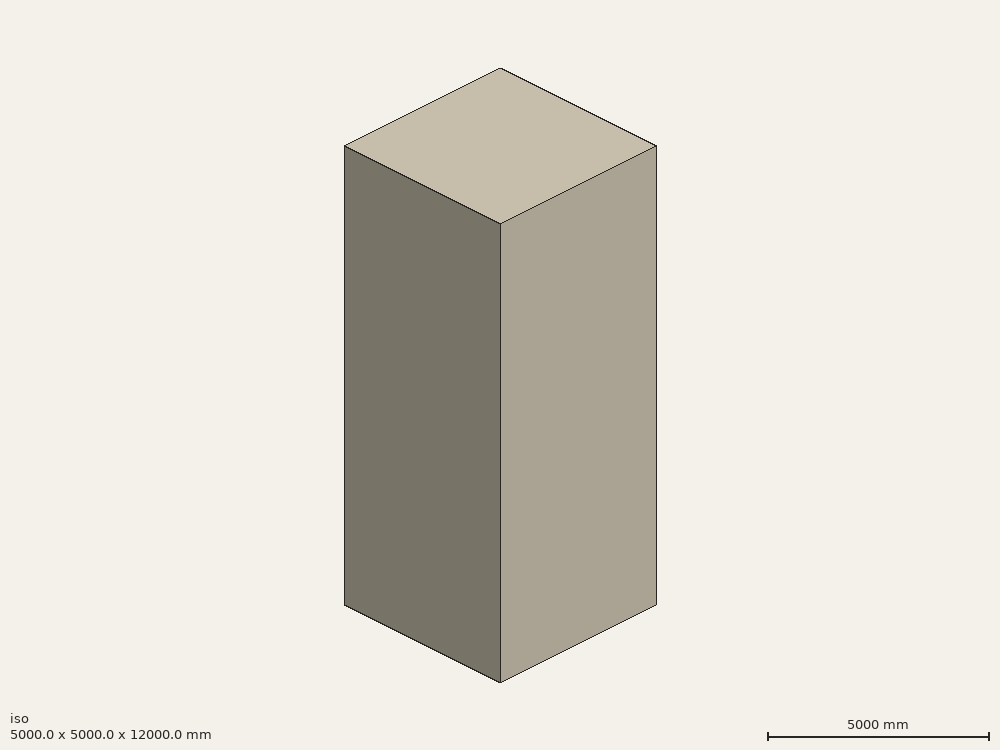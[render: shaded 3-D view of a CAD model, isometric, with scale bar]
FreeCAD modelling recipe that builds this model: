
FCSTD DOCUMENT  (FreeCAD 1.0R39109 (Git))
Label: revolveTester-7_scaled
License: All rights reserved
LicenseURL: http://en.wikipedia.org/wiki/All_rights_reserved
objects: App::DocumentObjectGroupPython×1248, Part::FeaturePython×2, App::Part×2, Sketcher::SketchObject×1, Part::Revolution×1, Part::Cylinder×1, Part::Cut×1
note: 7 computed .brp shape members not serialized (recipe doc carries the construction recipe); baked Part::Feature solids carry a one-line shape summary decoded from their .brp

FEATURE [App::DocumentObjectGroupPython] HALFPI  # scripted group (container) (typed FeaturePython)
  name = HALFPI
  value = pi/2.
FEATURE [App::DocumentObjectGroupPython] PI  # scripted group (container) (typed FeaturePython)
  name = PI
  value = 1.*pi
FEATURE [App::DocumentObjectGroupPython] TWOPI  # scripted group (container) (typed FeaturePython)
  name = TWOPI
  value = 2.*pi
FEATURE [App::DocumentObjectGroupPython] Constants  # scripted group (container) (typed FeaturePython)
  Group = -> [HALFPI,PI,TWOPI]
FEATURE [App::DocumentObjectGroupPython] Variables  # scripted group (container) (typed FeaturePython)
FEATURE [App::DocumentObjectGroupPython] Quantities  # scripted group (container) (typed FeaturePython)
FEATURE [App::DocumentObjectGroupPython] Isotopes  # scripted group (container) (typed FeaturePython)
FEATURE [App::DocumentObjectGroupPython] Elements  # scripted group (container) (typed FeaturePython)
FEATURE [App::DocumentObjectGroupPython] G4Isotopes  # scripted group (container) (typed FeaturePython)
FEATURE [App::DocumentObjectGroupPython] H_element  # scripted group (container) (typed FeaturePython)
  Z = 1
  atom_value = 1.008
  formula = H
  name = H_element
FEATURE [App::DocumentObjectGroupPython] He_element  # scripted group (container) (typed FeaturePython)
  Z = 2
  atom_value = 4.0026
  formula = He
  name = He_element
FEATURE [App::DocumentObjectGroupPython] Li_element  # scripted group (container) (typed FeaturePython)
  Z = 3
  atom_value = 6.94
  formula = Li
  name = Li_element
FEATURE [App::DocumentObjectGroupPython] Be_element  # scripted group (container) (typed FeaturePython)
  Z = 4
  atom_value = 9.01218
  formula = Be
  name = Be_element
FEATURE [App::DocumentObjectGroupPython] B_element  # scripted group (container) (typed FeaturePython)
  Z = 5
  atom_value = 10.81
  formula = B
  name = B_element
FEATURE [App::DocumentObjectGroupPython] C_element  # scripted group (container) (typed FeaturePython)
  Z = 6
  atom_value = 12.011
  formula = C
  name = C_element
FEATURE [App::DocumentObjectGroupPython] N_element  # scripted group (container) (typed FeaturePython)
  Z = 7
  atom_value = 14.007
  formula = N
  name = N_element
FEATURE [App::DocumentObjectGroupPython] O_element  # scripted group (container) (typed FeaturePython)
  Z = 8
  atom_value = 15.999
  formula = O
  name = O_element
FEATURE [App::DocumentObjectGroupPython] F_element  # scripted group (container) (typed FeaturePython)
  Z = 9
  atom_value = 18.9984
  formula = F
  name = F_element
FEATURE [App::DocumentObjectGroupPython] Ne_element  # scripted group (container) (typed FeaturePython)
  Z = 10
  atom_value = 20.1797
  formula = Ne
  name = Ne_element
FEATURE [App::DocumentObjectGroupPython] Na_element  # scripted group (container) (typed FeaturePython)
  Z = 11
  atom_value = 22.9898
  formula = Na
  name = Na_element
FEATURE [App::DocumentObjectGroupPython] Mg_element  # scripted group (container) (typed FeaturePython)
  Z = 12
  atom_value = 24.305
  formula = Mg
  name = Mg_element
FEATURE [App::DocumentObjectGroupPython] Al_element  # scripted group (container) (typed FeaturePython)
  Z = 13
  atom_value = 26.9815
  formula = Al
  name = Al_element
FEATURE [App::DocumentObjectGroupPython] Si_element  # scripted group (container) (typed FeaturePython)
  Z = 14
  atom_value = 28.085
  formula = Si
  name = Si_element
FEATURE [App::DocumentObjectGroupPython] P_element  # scripted group (container) (typed FeaturePython)
  Z = 15
  atom_value = 30.9738
  formula = P
  name = P_element
FEATURE [App::DocumentObjectGroupPython] S_element  # scripted group (container) (typed FeaturePython)
  Z = 16
  atom_value = 32.06
  formula = S
  name = S_element
FEATURE [App::DocumentObjectGroupPython] Cl_element  # scripted group (container) (typed FeaturePython)
  Z = 17
  atom_value = 35.45
  formula = Cl
  name = Cl_element
FEATURE [App::DocumentObjectGroupPython] Ar_element  # scripted group (container) (typed FeaturePython)
  Z = 18
  atom_value = 39.95
  formula = Ar
  name = Ar_element
FEATURE [App::DocumentObjectGroupPython] K_element  # scripted group (container) (typed FeaturePython)
  Z = 19
  atom_value = 39.0983
  formula = K
  name = K_element
FEATURE [App::DocumentObjectGroupPython] Ca_element  # scripted group (container) (typed FeaturePython)
  Z = 20
  atom_value = 40.078
  formula = Ca
  name = Ca_element
FEATURE [App::DocumentObjectGroupPython] Sc_element  # scripted group (container) (typed FeaturePython)
  Z = 21
  atom_value = 44.9559
  formula = Sc
  name = Sc_element
FEATURE [App::DocumentObjectGroupPython] Ti_element  # scripted group (container) (typed FeaturePython)
  Z = 22
  atom_value = 47.867
  formula = Ti
  name = Ti_element
FEATURE [App::DocumentObjectGroupPython] V_element  # scripted group (container) (typed FeaturePython)
  Z = 23
  atom_value = 50.9415
  formula = V
  name = V_element
FEATURE [App::DocumentObjectGroupPython] Cr_element  # scripted group (container) (typed FeaturePython)
  Z = 24
  atom_value = 51.9961
  formula = Cr
  name = Cr_element
FEATURE [App::DocumentObjectGroupPython] Mn_element  # scripted group (container) (typed FeaturePython)
  Z = 25
  atom_value = 54.938
  formula = Mn
  name = Mn_element
FEATURE [App::DocumentObjectGroupPython] Fe_element  # scripted group (container) (typed FeaturePython)
  Z = 26
  atom_value = 55.845
  formula = Fe
  name = Fe_element
FEATURE [App::DocumentObjectGroupPython] Co_element  # scripted group (container) (typed FeaturePython)
  Z = 27
  atom_value = 58.9332
  formula = Co
  name = Co_element
FEATURE [App::DocumentObjectGroupPython] Ni_element  # scripted group (container) (typed FeaturePython)
  Z = 28
  atom_value = 58.6934
  formula = Ni
  name = Ni_element
FEATURE [App::DocumentObjectGroupPython] Cu_element  # scripted group (container) (typed FeaturePython)
  Z = 29
  atom_value = 63.546
  formula = Cu
  name = Cu_element
FEATURE [App::DocumentObjectGroupPython] Zn_element  # scripted group (container) (typed FeaturePython)
  Z = 30
  atom_value = 65.38
  formula = Zn
  name = Zn_element
FEATURE [App::DocumentObjectGroupPython] Ga_element  # scripted group (container) (typed FeaturePython)
  Z = 31
  atom_value = 69.723
  formula = Ga
  name = Ga_element
FEATURE [App::DocumentObjectGroupPython] Ge_element  # scripted group (container) (typed FeaturePython)
  Z = 32
  atom_value = 72.63
  formula = Ge
  name = Ge_element
FEATURE [App::DocumentObjectGroupPython] As_element  # scripted group (container) (typed FeaturePython)
  Z = 33
  atom_value = 74.9216
  formula = As
  name = As_element
FEATURE [App::DocumentObjectGroupPython] Se_element  # scripted group (container) (typed FeaturePython)
  Z = 34
  atom_value = 78.971
  formula = Se
  name = Se_element
FEATURE [App::DocumentObjectGroupPython] Br_element  # scripted group (container) (typed FeaturePython)
  Z = 35
  atom_value = 79.904
  formula = Br
  name = Br_element
FEATURE [App::DocumentObjectGroupPython] Kr_element  # scripted group (container) (typed FeaturePython)
  Z = 36
  atom_value = 83.798
  formula = Kr
  name = Kr_element
FEATURE [App::DocumentObjectGroupPython] Rb_element  # scripted group (container) (typed FeaturePython)
  Z = 37
  atom_value = 85.4678
  formula = Rb
  name = Rb_element
FEATURE [App::DocumentObjectGroupPython] Sr_element  # scripted group (container) (typed FeaturePython)
  Z = 38
  atom_value = 87.62
  formula = Sr
  name = Sr_element
FEATURE [App::DocumentObjectGroupPython] Y_element  # scripted group (container) (typed FeaturePython)
  Z = 39
  atom_value = 88.9058
  formula = Y
  name = Y_element
FEATURE [App::DocumentObjectGroupPython] Zr_element  # scripted group (container) (typed FeaturePython)
  Z = 40
  atom_value = 91.224
  formula = Zr
  name = Zr_element
FEATURE [App::DocumentObjectGroupPython] Nb_element  # scripted group (container) (typed FeaturePython)
  Z = 41
  atom_value = 92.9064
  formula = Nb
  name = Nb_element
FEATURE [App::DocumentObjectGroupPython] Mo_element  # scripted group (container) (typed FeaturePython)
  Z = 42
  atom_value = 95.95
  formula = Mo
  name = Mo_element
FEATURE [App::DocumentObjectGroupPython] Tc_element  # scripted group (container) (typed FeaturePython)
  Z = 43
  atom_value = 97
  formula = Tc
  name = Tc_element
FEATURE [App::DocumentObjectGroupPython] Ru_element  # scripted group (container) (typed FeaturePython)
  Z = 44
  atom_value = 101.07
  formula = Ru
  name = Ru_element
FEATURE [App::DocumentObjectGroupPython] Rh_element  # scripted group (container) (typed FeaturePython)
  Z = 45
  atom_value = 102.905
  formula = Rh
  name = Rh_element
FEATURE [App::DocumentObjectGroupPython] Pd_element  # scripted group (container) (typed FeaturePython)
  Z = 46
  atom_value = 106.42
  formula = Pd
  name = Pd_element
FEATURE [App::DocumentObjectGroupPython] Ag_element  # scripted group (container) (typed FeaturePython)
  Z = 47
  atom_value = 107.868
  formula = Ag
  name = Ag_element
FEATURE [App::DocumentObjectGroupPython] Cd_element  # scripted group (container) (typed FeaturePython)
  Z = 48
  atom_value = 112.414
  formula = Cd
  name = Cd_element
FEATURE [App::DocumentObjectGroupPython] In_element  # scripted group (container) (typed FeaturePython)
  Z = 49
  atom_value = 114.818
  formula = In
  name = In_element
FEATURE [App::DocumentObjectGroupPython] Sn_element  # scripted group (container) (typed FeaturePython)
  Z = 50
  atom_value = 118.71
  formula = Sn
  name = Sn_element
FEATURE [App::DocumentObjectGroupPython] Sb_element  # scripted group (container) (typed FeaturePython)
  Z = 51
  atom_value = 121.76
  formula = Sb
  name = Sb_element
FEATURE [App::DocumentObjectGroupPython] Te_element  # scripted group (container) (typed FeaturePython)
  Z = 52
  atom_value = 127.6
  formula = Te
  name = Te_element
FEATURE [App::DocumentObjectGroupPython] I_element  # scripted group (container) (typed FeaturePython)
  Z = 53
  atom_value = 126.904
  formula = I
  name = I_element
FEATURE [App::DocumentObjectGroupPython] Xe_element  # scripted group (container) (typed FeaturePython)
  Z = 54
  atom_value = 131.293
  formula = Xe
  name = Xe_element
FEATURE [App::DocumentObjectGroupPython] Cs_element  # scripted group (container) (typed FeaturePython)
  Z = 55
  atom_value = 132.905
  formula = Cs
  name = Cs_element
FEATURE [App::DocumentObjectGroupPython] Ba_element  # scripted group (container) (typed FeaturePython)
  Z = 56
  atom_value = 137.327
  formula = Ba
  name = Ba_element
FEATURE [App::DocumentObjectGroupPython] La_element  # scripted group (container) (typed FeaturePython)
  Z = 57
  atom_value = 138.905
  formula = La
  name = La_element
FEATURE [App::DocumentObjectGroupPython] Ce_element  # scripted group (container) (typed FeaturePython)
  Z = 58
  atom_value = 140.116
  formula = Ce
  name = Ce_element
FEATURE [App::DocumentObjectGroupPython] Pr_element  # scripted group (container) (typed FeaturePython)
  Z = 59
  atom_value = 140.908
  formula = Pr
  name = Pr_element
FEATURE [App::DocumentObjectGroupPython] Nd_element  # scripted group (container) (typed FeaturePython)
  Z = 60
  atom_value = 144.242
  formula = Nd
  name = Nd_element
FEATURE [App::DocumentObjectGroupPython] Pm_element  # scripted group (container) (typed FeaturePython)
  Z = 61
  atom_value = 145
  formula = Pm
  name = Pm_element
FEATURE [App::DocumentObjectGroupPython] Sm_element  # scripted group (container) (typed FeaturePython)
  Z = 62
  atom_value = 150.36
  formula = Sm
  name = Sm_element
FEATURE [App::DocumentObjectGroupPython] Eu_element  # scripted group (container) (typed FeaturePython)
  Z = 63
  atom_value = 151.964
  formula = Eu
  name = Eu_element
FEATURE [App::DocumentObjectGroupPython] Gd_element  # scripted group (container) (typed FeaturePython)
  Z = 64
  atom_value = 157.25
  formula = Gd
  name = Gd_element
FEATURE [App::DocumentObjectGroupPython] Tb_element  # scripted group (container) (typed FeaturePython)
  Z = 65
  atom_value = 158.925
  formula = Tb
  name = Tb_element
FEATURE [App::DocumentObjectGroupPython] Dy_element  # scripted group (container) (typed FeaturePython)
  Z = 66
  atom_value = 162.5
  formula = Dy
  name = Dy_element
FEATURE [App::DocumentObjectGroupPython] Ho_element  # scripted group (container) (typed FeaturePython)
  Z = 67
  atom_value = 164.93
  formula = Ho
  name = Ho_element
FEATURE [App::DocumentObjectGroupPython] Er_element  # scripted group (container) (typed FeaturePython)
  Z = 68
  atom_value = 167.259
  formula = Er
  name = Er_element
FEATURE [App::DocumentObjectGroupPython] Tm_element  # scripted group (container) (typed FeaturePython)
  Z = 69
  atom_value = 168.934
  formula = Tm
  name = Tm_element
FEATURE [App::DocumentObjectGroupPython] Yb_element  # scripted group (container) (typed FeaturePython)
  Z = 70
  atom_value = 173.045
  formula = Yb
  name = Yb_element
FEATURE [App::DocumentObjectGroupPython] Lu_element  # scripted group (container) (typed FeaturePython)
  Z = 71
  atom_value = 174.967
  formula = Lu
  name = Lu_element
FEATURE [App::DocumentObjectGroupPython] Hf_element  # scripted group (container) (typed FeaturePython)
  Z = 72
  atom_value = 178.49
  formula = Hf
  name = Hf_element
FEATURE [App::DocumentObjectGroupPython] Ta_element  # scripted group (container) (typed FeaturePython)
  Z = 73
  atom_value = 180.948
  formula = Ta
  name = Ta_element
FEATURE [App::DocumentObjectGroupPython] W_element  # scripted group (container) (typed FeaturePython)
  Z = 74
  atom_value = 183.84
  formula = W
  name = W_element
FEATURE [App::DocumentObjectGroupPython] Re_element  # scripted group (container) (typed FeaturePython)
  Z = 75
  atom_value = 186.207
  formula = Re
  name = Re_element
FEATURE [App::DocumentObjectGroupPython] Os_element  # scripted group (container) (typed FeaturePython)
  Z = 76
  atom_value = 190.23
  formula = Os
  name = Os_element
FEATURE [App::DocumentObjectGroupPython] Ir_element  # scripted group (container) (typed FeaturePython)
  Z = 77
  atom_value = 192.217
  formula = Ir
  name = Ir_element
FEATURE [App::DocumentObjectGroupPython] Pt_element  # scripted group (container) (typed FeaturePython)
  Z = 78
  atom_value = 195.084
  formula = Pt
  name = Pt_element
FEATURE [App::DocumentObjectGroupPython] Au_element  # scripted group (container) (typed FeaturePython)
  Z = 79
  atom_value = 196.967
  formula = Au
  name = Au_element
FEATURE [App::DocumentObjectGroupPython] Hg_element  # scripted group (container) (typed FeaturePython)
  Z = 80
  atom_value = 200.592
  formula = Hg
  name = Hg_element
FEATURE [App::DocumentObjectGroupPython] Tl_element  # scripted group (container) (typed FeaturePython)
  Z = 81
  atom_value = 204.38
  formula = Tl
  name = Tl_element
FEATURE [App::DocumentObjectGroupPython] Pb_element  # scripted group (container) (typed FeaturePython)
  Z = 82
  atom_value = 207.2
  formula = Pb
  name = Pb_element
FEATURE [App::DocumentObjectGroupPython] Bi_element  # scripted group (container) (typed FeaturePython)
  Z = 83
  atom_value = 208.98
  formula = Bi
  name = Bi_element
FEATURE [App::DocumentObjectGroupPython] Po_element  # scripted group (container) (typed FeaturePython)
  Z = 84
  atom_value = 209
  formula = Po
  name = Po_element
FEATURE [App::DocumentObjectGroupPython] At_element  # scripted group (container) (typed FeaturePython)
  Z = 85
  atom_value = 210
  formula = At
  name = At_element
FEATURE [App::DocumentObjectGroupPython] Rn_element  # scripted group (container) (typed FeaturePython)
  Z = 86
  atom_value = 222
  formula = Rn
  name = Rn_element
FEATURE [App::DocumentObjectGroupPython] Fr_element  # scripted group (container) (typed FeaturePython)
  Z = 87
  atom_value = 223
  formula = Fr
  name = Fr_element
FEATURE [App::DocumentObjectGroupPython] Ra_element  # scripted group (container) (typed FeaturePython)
  Z = 88
  atom_value = 226
  formula = Ra
  name = Ra_element
FEATURE [App::DocumentObjectGroupPython] Ac_element  # scripted group (container) (typed FeaturePython)
  Z = 89
  atom_value = 227
  formula = Ac
  name = Ac_element
FEATURE [App::DocumentObjectGroupPython] Th_element  # scripted group (container) (typed FeaturePython)
  Z = 90
  atom_value = 232.038
  formula = Th
  name = Th_element
FEATURE [App::DocumentObjectGroupPython] Pa_element  # scripted group (container) (typed FeaturePython)
  Z = 91
  atom_value = 231.036
  formula = Pa
  name = Pa_element
FEATURE [App::DocumentObjectGroupPython] U_element  # scripted group (container) (typed FeaturePython)
  Z = 92
  atom_value = 238.029
  formula = U
  name = U_element
FEATURE [App::DocumentObjectGroupPython] Np_element  # scripted group (container) (typed FeaturePython)
  Z = 93
  atom_value = 237
  formula = Np
  name = Np_element
FEATURE [App::DocumentObjectGroupPython] Pu_element  # scripted group (container) (typed FeaturePython)
  Z = 94
  atom_value = 244
  formula = Pu
  name = Pu_element
FEATURE [App::DocumentObjectGroupPython] Am_element  # scripted group (container) (typed FeaturePython)
  Z = 95
  atom_value = 243
  formula = Am
  name = Am_element
FEATURE [App::DocumentObjectGroupPython] Cm_element  # scripted group (container) (typed FeaturePython)
  Z = 96
  atom_value = 247
  formula = Cm
  name = Cm_element
FEATURE [App::DocumentObjectGroupPython] Bk_element  # scripted group (container) (typed FeaturePython)
  Z = 97
  atom_value = 247
  formula = Bk
  name = Bk_element
FEATURE [App::DocumentObjectGroupPython] Cf_element  # scripted group (container) (typed FeaturePython)
  Z = 98
  atom_value = 251
  formula = Cf
  name = Cf_element
FEATURE [App::DocumentObjectGroupPython] G4Elements  # scripted group (container) (typed FeaturePython)
  Group = -> [H_element,He_element,Li_element,Be_element,B_element,C_element,N_element,O_element,F_element,Ne_element,Na_element,Mg_element,Al_element,Si_element,P_element,S_element,Cl_element,Ar_element,K_element,Ca_element,Sc_element,Ti_element,V_element,Cr_element,Mn_element,Fe_element,Co_element,Ni_element,Cu_element,Zn_element,Ga_element,Ge_element,As_element,Se_element,Br_element,Kr_element,Rb_element,+61 more]
FEATURE [App::DocumentObjectGroupPython] H_element001  label="H_element : 0.101"  # scripted group (container) (typed FeaturePython)
  n = 0.101327
FEATURE [App::DocumentObjectGroupPython] C_element001  label="C_element : 0.775"  # scripted group (container) (typed FeaturePython)
  n = 0.7755
FEATURE [App::DocumentObjectGroupPython] N_element001  label="N_element : 0.035"  # scripted group (container) (typed FeaturePython)
  n = 0.035057
FEATURE [App::DocumentObjectGroupPython] O_element001  label="O_element : 0.052"  # scripted group (container) (typed FeaturePython)
  n = 0.0523159
FEATURE [App::DocumentObjectGroupPython] F_element001  label="F_element : 0.017"  # scripted group (container) (typed FeaturePython)
  n = 0.017422
FEATURE [App::DocumentObjectGroupPython] Ca_element001  label="Ca_element : 0.018"  # scripted group (container) (typed FeaturePython)
  n = 0.018378
FEATURE [App::DocumentObjectGroupPython] G4_A_150_TISSUE  label="G4_A-150_TISSUE"  # scripted group (container) (typed FeaturePython)
  Dunit = g/cm3
  Dvalue = 1.127
  Group = -> [H_element001,C_element001,N_element001,O_element001,F_element001,Ca_element001]
  conduct = 2
  density = 1
  expand = 3
  formula = G4_A-150_TISSUE
  name = G4_A-150_TISSUE
  specific = 4
FEATURE [App::DocumentObjectGroupPython] C_element002  label="C_element : 3"  # scripted group (container) (typed FeaturePython)
  n = 3
  ref = C_element
FEATURE [App::DocumentObjectGroupPython] H_element002  label="H_element : 6"  # scripted group (container) (typed FeaturePython)
  n = 6
  ref = H_element
FEATURE [App::DocumentObjectGroupPython] O_element002  label="O_element : 1"  # scripted group (container) (typed FeaturePython)
  n = 1
  ref = O_element
FEATURE [App::DocumentObjectGroupPython] G4_ACETONE  # scripted group (container) (typed FeaturePython)
  Dunit = g/cm3
  Dvalue = 0.7899
  Group = -> [C_element002,H_element002,O_element002]
  conduct = 2
  density = 1
  expand = 3
  formula = G4_ACETONE
  name = G4_ACETONE
  specific = 4
FEATURE [App::DocumentObjectGroupPython] C_element003  label="C_element : 2"  # scripted group (container) (typed FeaturePython)
  n = 2
  ref = C_element
FEATURE [App::DocumentObjectGroupPython] H_element003  label="H_element : 2"  # scripted group (container) (typed FeaturePython)
  n = 2
  ref = H_element
FEATURE [App::DocumentObjectGroupPython] G4_ACETYLENE  # scripted group (container) (typed FeaturePython)
  Dunit = g/cm3
  Dvalue = 0.0010967
  Group = -> [C_element003,H_element003]
  conduct = 2
  density = 1
  expand = 3
  formula = G4_ACETYLENE
  name = G4_ACETYLENE
  specific = 4
FEATURE [App::DocumentObjectGroupPython] C_element004  label="C_element : 5"  # scripted group (container) (typed FeaturePython)
  n = 5
  ref = C_element
FEATURE [App::DocumentObjectGroupPython] H_element004  label="H_element : 5"  # scripted group (container) (typed FeaturePython)
  n = 5
  ref = H_element
FEATURE [App::DocumentObjectGroupPython] N_element002  label="N_element : 5"  # scripted group (container) (typed FeaturePython)
  n = 5
  ref = N_element
FEATURE [App::DocumentObjectGroupPython] G4_ADENINE  # scripted group (container) (typed FeaturePython)
  Dunit = g/cm3
  Dvalue = 1.6
  Group = -> [C_element004,H_element004,N_element002]
  conduct = 2
  density = 1
  expand = 3
  formula = G4_ADENINE
  name = G4_ADENINE
  specific = 4
FEATURE [App::DocumentObjectGroupPython] H_element005  label="H_element : 0.114"  # scripted group (container) (typed FeaturePython)
  n = 0.114
FEATURE [App::DocumentObjectGroupPython] C_element005  label="C_element : 0.598"  # scripted group (container) (typed FeaturePython)
  n = 0.598
FEATURE [App::DocumentObjectGroupPython] N_element003  label="N_element : 0.007"  # scripted group (container) (typed FeaturePython)
  n = 0.007
FEATURE [App::DocumentObjectGroupPython] O_element003  label="O_element : 0.278"  # scripted group (container) (typed FeaturePython)
  n = 0.278
FEATURE [App::DocumentObjectGroupPython] Na_element001  label="Na_element : 0.001"  # scripted group (container) (typed FeaturePython)
  n = 0.001
FEATURE [App::DocumentObjectGroupPython] S_element001  label="S_element : 0.001"  # scripted group (container) (typed FeaturePython)
  n = 0.001
FEATURE [App::DocumentObjectGroupPython] Cl_element001  label="Cl_element : 0.001"  # scripted group (container) (typed FeaturePython)
  n = 0.001
FEATURE [App::DocumentObjectGroupPython] G4_ADIPOSE_TISSUE_ICRP  # scripted group (container) (typed FeaturePython)
  Dunit = g/cm3
  Dvalue = 0.95
  Group = -> [H_element005,C_element005,N_element003,O_element003,Na_element001,S_element001,Cl_element001]
  conduct = 2
  density = 1
  expand = 3
  formula = G4_ADIPOSE_TISSUE_ICRP
  name = G4_ADIPOSE_TISSUE_ICRP
  specific = 4
FEATURE [App::DocumentObjectGroupPython] C_element006  label="C_element : 0.000"  # scripted group (container) (typed FeaturePython)
  n = 0.000124
FEATURE [App::DocumentObjectGroupPython] N_element004  label="N_element : 0.755"  # scripted group (container) (typed FeaturePython)
  n = 0.755268
FEATURE [App::DocumentObjectGroupPython] O_element004  label="O_element : 0.232"  # scripted group (container) (typed FeaturePython)
  n = 0.231781
FEATURE [App::DocumentObjectGroupPython] Ar_element001  label="Ar_element : 0.013"  # scripted group (container) (typed FeaturePython)
  n = 0.012827
FEATURE [App::DocumentObjectGroupPython] G4_AIR  # scripted group (container) (typed FeaturePython)
  Dunit = g/cm3
  Dvalue = 0.00120479
  Group = -> [C_element006,N_element004,O_element004,Ar_element001]
  conduct = 2
  density = 1
  expand = 3
  formula = G4_AIR
  name = G4_AIR
  specific = 4
FEATURE [App::DocumentObjectGroupPython] C_element007  label="C_element : 006"  # scripted group (container) (typed FeaturePython)
  n = 3
  ref = C_element
FEATURE [App::DocumentObjectGroupPython] H_element006  label="H_element : 7"  # scripted group (container) (typed FeaturePython)
  n = 7
  ref = H_element
FEATURE [App::DocumentObjectGroupPython] N_element005  label="N_element : 1"  # scripted group (container) (typed FeaturePython)
  n = 1
  ref = N_element
FEATURE [App::DocumentObjectGroupPython] O_element005  label="O_element : 2"  # scripted group (container) (typed FeaturePython)
  n = 2
  ref = O_element
FEATURE [App::DocumentObjectGroupPython] G4_ALANINE  # scripted group (container) (typed FeaturePython)
  Dunit = g/cm3
  Dvalue = 1.42
  Group = -> [C_element007,H_element006,N_element005,O_element005]
  conduct = 2
  density = 1
  expand = 3
  formula = G4_ALANINE
  name = G4_ALANINE
  specific = 4
FEATURE [App::DocumentObjectGroupPython] Al_element001  label="Al_element : 2"  # scripted group (container) (typed FeaturePython)
  n = 2
  ref = Al_element
FEATURE [App::DocumentObjectGroupPython] O_element006  label="O_element : 3"  # scripted group (container) (typed FeaturePython)
  n = 3
  ref = O_element
FEATURE [App::DocumentObjectGroupPython] G4_ALUMINUM_OXIDE  # scripted group (container) (typed FeaturePython)
  Dunit = g/cm3
  Dvalue = 3.97
  Group = -> [Al_element001,O_element006]
  conduct = 2
  density = 1
  expand = 3
  formula = G4_ALUMINUM_OXIDE
  name = G4_ALUMINUM_OXIDE
  specific = 4
FEATURE [App::DocumentObjectGroupPython] H_element007  label="H_element : 0.106"  # scripted group (container) (typed FeaturePython)
  n = 0.10593
FEATURE [App::DocumentObjectGroupPython] C_element008  label="C_element : 0.789"  # scripted group (container) (typed FeaturePython)
  n = 0.788974
FEATURE [App::DocumentObjectGroupPython] O_element007  label="O_element : 0.105"  # scripted group (container) (typed FeaturePython)
  n = 0.105096
FEATURE [App::DocumentObjectGroupPython] G4_AMBER  # scripted group (container) (typed FeaturePython)
  Dunit = g/cm3
  Dvalue = 1.1
  Group = -> [H_element007,C_element008,O_element007]
  conduct = 2
  density = 1
  expand = 3
  formula = G4_AMBER
  name = G4_AMBER
  specific = 4
FEATURE [App::DocumentObjectGroupPython] N_element006  label="N_element : 006"  # scripted group (container) (typed FeaturePython)
  n = 1
  ref = N_element
FEATURE [App::DocumentObjectGroupPython] H_element008  label="H_element : 3"  # scripted group (container) (typed FeaturePython)
  n = 3
  ref = H_element
FEATURE [App::DocumentObjectGroupPython] G4_AMMONIA  # scripted group (container) (typed FeaturePython)
  Dunit = g/cm3
  Dvalue = 0.000826019
  Group = -> [N_element006,H_element008]
  conduct = 2
  density = 1
  expand = 3
  formula = G4_AMMONIA
  name = G4_AMMONIA
  specific = 4
FEATURE [App::DocumentObjectGroupPython] C_element009  label="C_element : 6"  # scripted group (container) (typed FeaturePython)
  n = 6
  ref = C_element
FEATURE [App::DocumentObjectGroupPython] H_element009  label="H_element : 008"  # scripted group (container) (typed FeaturePython)
  n = 7
  ref = H_element
FEATURE [App::DocumentObjectGroupPython] N_element007  label="N_element : 007"  # scripted group (container) (typed FeaturePython)
  n = 1
  ref = N_element
FEATURE [App::DocumentObjectGroupPython] G4_ANILINE  # scripted group (container) (typed FeaturePython)
  Dunit = g/cm3
  Dvalue = 1.0235
  Group = -> [C_element009,H_element009,N_element007]
  conduct = 2
  density = 1
  expand = 3
  formula = G4_ANILINE
  name = G4_ANILINE
  specific = 4
FEATURE [App::DocumentObjectGroupPython] C_element010  label="C_element : 14"  # scripted group (container) (typed FeaturePython)
  n = 14
  ref = C_element
FEATURE [App::DocumentObjectGroupPython] H_element010  label="H_element : 10"  # scripted group (container) (typed FeaturePython)
  n = 10
  ref = H_element
FEATURE [App::DocumentObjectGroupPython] G4_ANTHRACENE  # scripted group (container) (typed FeaturePython)
  Dunit = g/cm3
  Dvalue = 1.283
  Group = -> [C_element010,H_element010]
  conduct = 2
  density = 1
  expand = 3
  formula = G4_ANTHRACENE
  name = G4_ANTHRACENE
  specific = 4
FEATURE [App::DocumentObjectGroupPython] H_element011  label="H_element : 0.065"  # scripted group (container) (typed FeaturePython)
  n = 0.0654709
FEATURE [App::DocumentObjectGroupPython] C_element011  label="C_element : 0.537"  # scripted group (container) (typed FeaturePython)
  n = 0.536944
FEATURE [App::DocumentObjectGroupPython] N_element008  label="N_element : 0.021"  # scripted group (container) (typed FeaturePython)
  n = 0.0215
FEATURE [App::DocumentObjectGroupPython] O_element008  label="O_element : 0.032"  # scripted group (container) (typed FeaturePython)
  n = 0.032085
FEATURE [App::DocumentObjectGroupPython] F_element002  label="F_element : 0.167"  # scripted group (container) (typed FeaturePython)
  n = 0.167411
FEATURE [App::DocumentObjectGroupPython] Ca_element002  label="Ca_element : 0.177"  # scripted group (container) (typed FeaturePython)
  n = 0.176589
FEATURE [App::DocumentObjectGroupPython] G4_B_100_BONE  label="G4_B-100_BONE"  # scripted group (container) (typed FeaturePython)
  Dunit = g/cm3
  Dvalue = 1.45
  Group = -> [H_element011,C_element011,N_element008,O_element008,F_element002,Ca_element002]
  conduct = 2
  density = 1
  expand = 3
  formula = G4_B-100_BONE
  name = G4_B-100_BONE
  specific = 4
FEATURE [App::DocumentObjectGroupPython] H_element012  label="H_element : 0.057"  # scripted group (container) (typed FeaturePython)
  n = 0.057441
FEATURE [App::DocumentObjectGroupPython] C_element012  label="C_element : 0.790"  # scripted group (container) (typed FeaturePython)
  n = 0.774591
FEATURE [App::DocumentObjectGroupPython] O_element009  label="O_element : 0.168"  # scripted group (container) (typed FeaturePython)
  n = 0.167968
FEATURE [App::DocumentObjectGroupPython] G4_BAKELITE  # scripted group (container) (typed FeaturePython)
  Dunit = g/cm3
  Dvalue = 1.25
  Group = -> [H_element012,C_element012,O_element009]
  conduct = 2
  density = 1
  expand = 3
  formula = G4_BAKELITE
  name = G4_BAKELITE
  specific = 4
FEATURE [App::DocumentObjectGroupPython] Ba_element001  label="Ba_element : 1"  # scripted group (container) (typed FeaturePython)
  n = 1
  ref = Ba_element
FEATURE [App::DocumentObjectGroupPython] F_element003  label="F_element : 2"  # scripted group (container) (typed FeaturePython)
  n = 2
  ref = F_element
FEATURE [App::DocumentObjectGroupPython] G4_BARIUM_FLUORIDE  # scripted group (container) (typed FeaturePython)
  Dunit = g/cm3
  Dvalue = 4.89
  Group = -> [Ba_element001,F_element003]
  conduct = 2
  density = 1
  expand = 3
  formula = G4_BARIUM_FLUORIDE
  name = G4_BARIUM_FLUORIDE
  specific = 4
FEATURE [App::DocumentObjectGroupPython] Ba_element002  label="Ba_element : 002"  # scripted group (container) (typed FeaturePython)
  n = 1
  ref = Ba_element
FEATURE [App::DocumentObjectGroupPython] S_element002  label="S_element : 1"  # scripted group (container) (typed FeaturePython)
  n = 1
  ref = S_element
FEATURE [App::DocumentObjectGroupPython] O_element010  label="O_element : 4"  # scripted group (container) (typed FeaturePython)
  n = 4
  ref = O_element
FEATURE [App::DocumentObjectGroupPython] G4_BARIUM_SULFATE  # scripted group (container) (typed FeaturePython)
  Dunit = g/cm3
  Dvalue = 4.5
  Group = -> [Ba_element002,S_element002,O_element010]
  conduct = 2
  density = 1
  expand = 3
  formula = G4_BARIUM_SULFATE
  name = G4_BARIUM_SULFATE
  specific = 4
FEATURE [App::DocumentObjectGroupPython] C_element013  label="C_element : 007"  # scripted group (container) (typed FeaturePython)
  n = 6
  ref = C_element
FEATURE [App::DocumentObjectGroupPython] H_element013  label="H_element : 009"  # scripted group (container) (typed FeaturePython)
  n = 6
  ref = H_element
FEATURE [App::DocumentObjectGroupPython] G4_BENZENE  # scripted group (container) (typed FeaturePython)
  Dunit = g/cm3
  Dvalue = 0.87865
  Group = -> [C_element013,H_element013]
  conduct = 2
  density = 1
  expand = 3
  formula = G4_BENZENE
  name = G4_BENZENE
  specific = 4
FEATURE [App::DocumentObjectGroupPython] Be_element001  label="Be_element : 1"  # scripted group (container) (typed FeaturePython)
  n = 1
  ref = Be_element
FEATURE [App::DocumentObjectGroupPython] O_element011  label="O_element : 005"  # scripted group (container) (typed FeaturePython)
  n = 1
  ref = O_element
FEATURE [App::DocumentObjectGroupPython] G4_BERYLLIUM_OXIDE  # scripted group (container) (typed FeaturePython)
  Dunit = g/cm3
  Dvalue = 3.01
  Group = -> [Be_element001,O_element011]
  conduct = 2
  density = 1
  expand = 3
  formula = G4_BERYLLIUM_OXIDE
  name = G4_BERYLLIUM_OXIDE
  specific = 4
FEATURE [App::DocumentObjectGroupPython] Bi_element001  label="Bi_element : 4"  # scripted group (container) (typed FeaturePython)
  n = 4
  ref = Bi_element
FEATURE [App::DocumentObjectGroupPython] Ge_element001  label="Ge_element : 3"  # scripted group (container) (typed FeaturePython)
  n = 3
  ref = Ge_element
FEATURE [App::DocumentObjectGroupPython] O_element012  label="O_element : 12"  # scripted group (container) (typed FeaturePython)
  n = 12
  ref = O_element
FEATURE [App::DocumentObjectGroupPython] G4_BGO  # scripted group (container) (typed FeaturePython)
  Dunit = g/cm3
  Dvalue = 7.13
  Group = -> [Bi_element001,Ge_element001,O_element012]
  conduct = 2
  density = 1
  expand = 3
  formula = G4_BGO
  name = G4_BGO
  specific = 4
FEATURE [App::DocumentObjectGroupPython] H_element014  label="H_element : 0.102"  # scripted group (container) (typed FeaturePython)
  n = 0.102
FEATURE [App::DocumentObjectGroupPython] C_element014  label="C_element : 0.110"  # scripted group (container) (typed FeaturePython)
  n = 0.11
FEATURE [App::DocumentObjectGroupPython] N_element009  label="N_element : 0.033"  # scripted group (container) (typed FeaturePython)
  n = 0.033
FEATURE [App::DocumentObjectGroupPython] O_element013  label="O_element : 0.745"  # scripted group (container) (typed FeaturePython)
  n = 0.745
FEATURE [App::DocumentObjectGroupPython] Na_element002  label="Na_element : 0.002"  # scripted group (container) (typed FeaturePython)
  n = 0.001
FEATURE [App::DocumentObjectGroupPython] P_element001  label="P_element : 0.001"  # scripted group (container) (typed FeaturePython)
  n = 0.001
FEATURE [App::DocumentObjectGroupPython] S_element003  label="S_element : 0.002"  # scripted group (container) (typed FeaturePython)
  n = 0.002
FEATURE [App::DocumentObjectGroupPython] Cl_element002  label="Cl_element : 0.003"  # scripted group (container) (typed FeaturePython)
  n = 0.003
FEATURE [App::DocumentObjectGroupPython] K_element001  label="K_element : 0.002"  # scripted group (container) (typed FeaturePython)
  n = 0.002
FEATURE [App::DocumentObjectGroupPython] Fe_element001  label="Fe_element : 0.001"  # scripted group (container) (typed FeaturePython)
  n = 0.001
FEATURE [App::DocumentObjectGroupPython] G4_BLOOD_ICRP  # scripted group (container) (typed FeaturePython)
  Dunit = g/cm3
  Dvalue = 1.06
  Group = -> [H_element014,C_element014,N_element009,O_element013,Na_element002,P_element001,S_element003,Cl_element002,K_element001,Fe_element001]
  conduct = 2
  density = 1
  expand = 3
  formula = G4_BLOOD_ICRP
  name = G4_BLOOD_ICRP
  specific = 4
FEATURE [App::DocumentObjectGroupPython] H_element015  label="H_element : 0.064"  # scripted group (container) (typed FeaturePython)
  n = 0.064
FEATURE [App::DocumentObjectGroupPython] C_element015  label="C_element : 0.278"  # scripted group (container) (typed FeaturePython)
  n = 0.278
FEATURE [App::DocumentObjectGroupPython] N_element010  label="N_element : 0.027"  # scripted group (container) (typed FeaturePython)
  n = 0.027
FEATURE [App::DocumentObjectGroupPython] O_element014  label="O_element : 0.410"  # scripted group (container) (typed FeaturePython)
  n = 0.41
FEATURE [App::DocumentObjectGroupPython] Mg_element001  label="Mg_element : 0.002"  # scripted group (container) (typed FeaturePython)
  n = 0.002
FEATURE [App::DocumentObjectGroupPython] P_element002  label="P_element : 0.070"  # scripted group (container) (typed FeaturePython)
  n = 0.07
FEATURE [App::DocumentObjectGroupPython] S_element004  label="S_element : 0.003"  # scripted group (container) (typed FeaturePython)
  n = 0.002
FEATURE [App::DocumentObjectGroupPython] Ca_element003  label="Ca_element : 0.147"  # scripted group (container) (typed FeaturePython)
  n = 0.147
FEATURE [App::DocumentObjectGroupPython] G4_BONE_COMPACT_ICRU  # scripted group (container) (typed FeaturePython)
  Dunit = g/cm3
  Dvalue = 1.85
  Group = -> [H_element015,C_element015,N_element010,O_element014,Mg_element001,P_element002,S_element004,Ca_element003]
  conduct = 2
  density = 1
  expand = 3
  formula = G4_BONE_COMPACT_ICRU
  name = G4_BONE_COMPACT_ICRU
  specific = 4
FEATURE [App::DocumentObjectGroupPython] H_element016  label="H_element : 0.034"  # scripted group (container) (typed FeaturePython)
  n = 0.034
FEATURE [App::DocumentObjectGroupPython] C_element016  label="C_element : 0.155"  # scripted group (container) (typed FeaturePython)
  n = 0.155
FEATURE [App::DocumentObjectGroupPython] N_element011  label="N_element : 0.042"  # scripted group (container) (typed FeaturePython)
  n = 0.042
FEATURE [App::DocumentObjectGroupPython] O_element015  label="O_element : 0.435"  # scripted group (container) (typed FeaturePython)
  n = 0.435
FEATURE [App::DocumentObjectGroupPython] Na_element003  label="Na_element : 0.003"  # scripted group (container) (typed FeaturePython)
  n = 0.001
FEATURE [App::DocumentObjectGroupPython] Mg_element002  label="Mg_element : 0.003"  # scripted group (container) (typed FeaturePython)
  n = 0.002
FEATURE [App::DocumentObjectGroupPython] P_element003  label="P_element : 0.103"  # scripted group (container) (typed FeaturePython)
  n = 0.103
FEATURE [App::DocumentObjectGroupPython] S_element005  label="S_element : 0.004"  # scripted group (container) (typed FeaturePython)
  n = 0.003
FEATURE [App::DocumentObjectGroupPython] Ca_element004  label="Ca_element : 0.225"  # scripted group (container) (typed FeaturePython)
  n = 0.225
FEATURE [App::DocumentObjectGroupPython] G4_BONE_CORTICAL_ICRP  # scripted group (container) (typed FeaturePython)
  Dunit = g/cm3
  Dvalue = 1.92
  Group = -> [H_element016,C_element016,N_element011,O_element015,Na_element003,Mg_element002,P_element003,S_element005,Ca_element004]
  conduct = 2
  density = 1
  expand = 3
  formula = G4_BONE_CORTICAL_ICRP
  name = G4_BONE_CORTICAL_ICRP
  specific = 4
FEATURE [App::DocumentObjectGroupPython] B_element001  label="B_element : 4"  # scripted group (container) (typed FeaturePython)
  n = 4
  ref = B_element
FEATURE [App::DocumentObjectGroupPython] C_element017  label="C_element : 1"  # scripted group (container) (typed FeaturePython)
  n = 1
  ref = C_element
FEATURE [App::DocumentObjectGroupPython] G4_BORON_CARBIDE  # scripted group (container) (typed FeaturePython)
  Dunit = g/cm3
  Dvalue = 2.52
  Group = -> [B_element001,C_element017]
  conduct = 2
  density = 1
  expand = 3
  formula = G4_BORON_CARBIDE
  name = G4_BORON_CARBIDE
  specific = 4
FEATURE [App::DocumentObjectGroupPython] B_element002  label="B_element : 2"  # scripted group (container) (typed FeaturePython)
  n = 2
  ref = B_element
FEATURE [App::DocumentObjectGroupPython] O_element016  label="O_element : 006"  # scripted group (container) (typed FeaturePython)
  n = 3
  ref = O_element
FEATURE [App::DocumentObjectGroupPython] G4_BORON_OXIDE  # scripted group (container) (typed FeaturePython)
  Dunit = g/cm3
  Dvalue = 1.812
  Group = -> [B_element002,O_element016]
  conduct = 2
  density = 1
  expand = 3
  formula = G4_BORON_OXIDE
  name = G4_BORON_OXIDE
  specific = 4
FEATURE [App::DocumentObjectGroupPython] H_element017  label="H_element : 0.107"  # scripted group (container) (typed FeaturePython)
  n = 0.107
FEATURE [App::DocumentObjectGroupPython] C_element018  label="C_element : 0.145"  # scripted group (container) (typed FeaturePython)
  n = 0.145
FEATURE [App::DocumentObjectGroupPython] N_element012  label="N_element : 0.022"  # scripted group (container) (typed FeaturePython)
  n = 0.022
FEATURE [App::DocumentObjectGroupPython] O_element017  label="O_element : 0.712"  # scripted group (container) (typed FeaturePython)
  n = 0.712
FEATURE [App::DocumentObjectGroupPython] Na_element004  label="Na_element : 0.004"  # scripted group (container) (typed FeaturePython)
  n = 0.002
FEATURE [App::DocumentObjectGroupPython] P_element004  label="P_element : 0.004"  # scripted group (container) (typed FeaturePython)
  n = 0.004
FEATURE [App::DocumentObjectGroupPython] S_element006  label="S_element : 0.005"  # scripted group (container) (typed FeaturePython)
  n = 0.002
FEATURE [App::DocumentObjectGroupPython] Cl_element003  label="Cl_element : 0.004"  # scripted group (container) (typed FeaturePython)
  n = 0.003
FEATURE [App::DocumentObjectGroupPython] K_element002  label="K_element : 0.003"  # scripted group (container) (typed FeaturePython)
  n = 0.003
FEATURE [App::DocumentObjectGroupPython] G4_BRAIN_ICRP  # scripted group (container) (typed FeaturePython)
  Dunit = g/cm3
  Dvalue = 1.04
  Group = -> [H_element017,C_element018,N_element012,O_element017,Na_element004,P_element004,S_element006,Cl_element003,K_element002]
  conduct = 2
  density = 1
  expand = 3
  formula = G4_BRAIN_ICRP
  name = G4_BRAIN_ICRP
  specific = 4
FEATURE [App::DocumentObjectGroupPython] C_element019  label="C_element : 4"  # scripted group (container) (typed FeaturePython)
  n = 4
  ref = C_element
FEATURE [App::DocumentObjectGroupPython] H_element018  label="H_element : 010"  # scripted group (container) (typed FeaturePython)
  n = 10
  ref = H_element
FEATURE [App::DocumentObjectGroupPython] G4_BUTANE  # scripted group (container) (typed FeaturePython)
  Dunit = g/cm3
  Dvalue = 0.00249343
  Group = -> [C_element019,H_element018]
  conduct = 2
  density = 1
  expand = 3
  formula = G4_BUTANE
  name = G4_BUTANE
  specific = 4
FEATURE [App::DocumentObjectGroupPython] C_element020  label="C_element : 008"  # scripted group (container) (typed FeaturePython)
  n = 4
  ref = C_element
FEATURE [App::DocumentObjectGroupPython] H_element019  label="H_element : 011"  # scripted group (container) (typed FeaturePython)
  n = 10
  ref = H_element
FEATURE [App::DocumentObjectGroupPython] O_element018  label="O_element : 007"  # scripted group (container) (typed FeaturePython)
  n = 1
  ref = O_element
FEATURE [App::DocumentObjectGroupPython] G4_N_BUTYL_ALCOHOL  label="G4_N-BUTYL_ALCOHOL"  # scripted group (container) (typed FeaturePython)
  Dunit = g/cm3
  Dvalue = 0.8098
  Group = -> [C_element020,H_element019,O_element018]
  conduct = 2
  density = 1
  expand = 3
  formula = G4_N-BUTYL_ALCOHOL
  name = G4_N-BUTYL_ALCOHOL
  specific = 4
FEATURE [App::DocumentObjectGroupPython] H_element020  label="H_element : 0.025"  # scripted group (container) (typed FeaturePython)
  n = 0.02468
FEATURE [App::DocumentObjectGroupPython] C_element021  label="C_element : 0.502"  # scripted group (container) (typed FeaturePython)
  n = 0.501611
FEATURE [App::DocumentObjectGroupPython] O_element019  label="O_element : 0.005"  # scripted group (container) (typed FeaturePython)
  n = 0.004527
FEATURE [App::DocumentObjectGroupPython] F_element004  label="F_element : 0.465"  # scripted group (container) (typed FeaturePython)
  n = 0.465209
FEATURE [App::DocumentObjectGroupPython] Si_element001  label="Si_element : 0.004"  # scripted group (container) (typed FeaturePython)
  n = 0.003973
FEATURE [App::DocumentObjectGroupPython] G4_C_552  label="G4_C-552"  # scripted group (container) (typed FeaturePython)
  Dunit = g/cm3
  Dvalue = 1.76
  Group = -> [H_element020,C_element021,O_element019,F_element004,Si_element001]
  conduct = 2
  density = 1
  expand = 3
  formula = G4_C-552
  name = G4_C-552
  specific = 4
FEATURE [App::DocumentObjectGroupPython] Cd_element001  label="Cd_element : 1"  # scripted group (container) (typed FeaturePython)
  n = 1
  ref = Cd_element
FEATURE [App::DocumentObjectGroupPython] Te_element001  label="Te_element : 1"  # scripted group (container) (typed FeaturePython)
  n = 1
  ref = Te_element
FEATURE [App::DocumentObjectGroupPython] G4_CADMIUM_TELLURIDE  # scripted group (container) (typed FeaturePython)
  Dunit = g/cm3
  Dvalue = 6.2
  Group = -> [Cd_element001,Te_element001]
  conduct = 2
  density = 1
  expand = 3
  formula = G4_CADMIUM_TELLURIDE
  name = G4_CADMIUM_TELLURIDE
  specific = 4
FEATURE [App::DocumentObjectGroupPython] Cd_element002  label="Cd_element : 002"  # scripted group (container) (typed FeaturePython)
  n = 1
  ref = Cd_element
FEATURE [App::DocumentObjectGroupPython] W_element001  label="W_element : 1"  # scripted group (container) (typed FeaturePython)
  n = 1
  ref = W_element
FEATURE [App::DocumentObjectGroupPython] O_element020  label="O_element : 008"  # scripted group (container) (typed FeaturePython)
  n = 4
  ref = O_element
FEATURE [App::DocumentObjectGroupPython] G4_CADMIUM_TUNGSTATE  # scripted group (container) (typed FeaturePython)
  Dunit = g/cm3
  Dvalue = 7.9
  Group = -> [Cd_element002,W_element001,O_element020]
  conduct = 2
  density = 1
  expand = 3
  formula = G4_CADMIUM_TUNGSTATE
  name = G4_CADMIUM_TUNGSTATE
  specific = 4
FEATURE [App::DocumentObjectGroupPython] Ca_element005  label="Ca_element : 1"  # scripted group (container) (typed FeaturePython)
  n = 1
  ref = Ca_element
FEATURE [App::DocumentObjectGroupPython] C_element022  label="C_element : 009"  # scripted group (container) (typed FeaturePython)
  n = 1
  ref = C_element
FEATURE [App::DocumentObjectGroupPython] O_element021  label="O_element : 009"  # scripted group (container) (typed FeaturePython)
  n = 3
  ref = O_element
FEATURE [App::DocumentObjectGroupPython] G4_CALCIUM_CARBONATE  # scripted group (container) (typed FeaturePython)
  Dunit = g/cm3
  Dvalue = 2.8
  Group = -> [Ca_element005,C_element022,O_element021]
  conduct = 2
  density = 1
  expand = 3
  formula = G4_CALCIUM_CARBONATE
  name = G4_CALCIUM_CARBONATE
  specific = 4
FEATURE [App::DocumentObjectGroupPython] Ca_element006  label="Ca_element : 002"  # scripted group (container) (typed FeaturePython)
  n = 1
  ref = Ca_element
FEATURE [App::DocumentObjectGroupPython] F_element005  label="F_element : 003"  # scripted group (container) (typed FeaturePython)
  n = 2
  ref = F_element
FEATURE [App::DocumentObjectGroupPython] G4_CALCIUM_FLUORIDE  # scripted group (container) (typed FeaturePython)
  Dunit = g/cm3
  Dvalue = 3.18
  Group = -> [Ca_element006,F_element005]
  conduct = 2
  density = 1
  expand = 3
  formula = G4_CALCIUM_FLUORIDE
  name = G4_CALCIUM_FLUORIDE
  specific = 4
FEATURE [App::DocumentObjectGroupPython] Ca_element007  label="Ca_element : 003"  # scripted group (container) (typed FeaturePython)
  n = 1
  ref = Ca_element
FEATURE [App::DocumentObjectGroupPython] O_element022  label="O_element : 010"  # scripted group (container) (typed FeaturePython)
  n = 1
  ref = O_element
FEATURE [App::DocumentObjectGroupPython] G4_CALCIUM_OXIDE  # scripted group (container) (typed FeaturePython)
  Dunit = g/cm3
  Dvalue = 3.3
  Group = -> [Ca_element007,O_element022]
  conduct = 2
  density = 1
  expand = 3
  formula = G4_CALCIUM_OXIDE
  name = G4_CALCIUM_OXIDE
  specific = 4
FEATURE [App::DocumentObjectGroupPython] Ca_element008  label="Ca_element : 004"  # scripted group (container) (typed FeaturePython)
  n = 1
  ref = Ca_element
FEATURE [App::DocumentObjectGroupPython] S_element007  label="S_element : 002"  # scripted group (container) (typed FeaturePython)
  n = 1
  ref = S_element
FEATURE [App::DocumentObjectGroupPython] O_element023  label="O_element : 011"  # scripted group (container) (typed FeaturePython)
  n = 4
  ref = O_element
FEATURE [App::DocumentObjectGroupPython] G4_CALCIUM_SULFATE  # scripted group (container) (typed FeaturePython)
  Dunit = g/cm3
  Dvalue = 2.96
  Group = -> [Ca_element008,S_element007,O_element023]
  conduct = 2
  density = 1
  expand = 3
  formula = G4_CALCIUM_SULFATE
  name = G4_CALCIUM_SULFATE
  specific = 4
FEATURE [App::DocumentObjectGroupPython] Ca_element009  label="Ca_element : 005"  # scripted group (container) (typed FeaturePython)
  n = 1
  ref = Ca_element
FEATURE [App::DocumentObjectGroupPython] W_element002  label="W_element : 002"  # scripted group (container) (typed FeaturePython)
  n = 1
  ref = W_element
FEATURE [App::DocumentObjectGroupPython] O_element024  label="O_element : 012"  # scripted group (container) (typed FeaturePython)
  n = 4
  ref = O_element
FEATURE [App::DocumentObjectGroupPython] G4_CALCIUM_TUNGSTATE  # scripted group (container) (typed FeaturePython)
  Dunit = g/cm3
  Dvalue = 6.062
  Group = -> [Ca_element009,W_element002,O_element024]
  conduct = 2
  density = 1
  expand = 3
  formula = G4_CALCIUM_TUNGSTATE
  name = G4_CALCIUM_TUNGSTATE
  specific = 4
FEATURE [App::DocumentObjectGroupPython] C_element023  label="C_element : 010"  # scripted group (container) (typed FeaturePython)
  n = 1
  ref = C_element
FEATURE [App::DocumentObjectGroupPython] O_element025  label="O_element : 013"  # scripted group (container) (typed FeaturePython)
  n = 2
  ref = O_element
FEATURE [App::DocumentObjectGroupPython] G4_CARBON_DIOXIDE  # scripted group (container) (typed FeaturePython)
  Dunit = g/cm3
  Dvalue = 0.00184212
  Group = -> [C_element023,O_element025]
  conduct = 2
  density = 1
  expand = 3
  formula = G4_CARBON_DIOXIDE
  name = G4_CARBON_DIOXIDE
  specific = 4
FEATURE [App::DocumentObjectGroupPython] C_element024  label="C_element : 011"  # scripted group (container) (typed FeaturePython)
  n = 1
  ref = C_element
FEATURE [App::DocumentObjectGroupPython] Cl_element004  label="Cl_element : 4"  # scripted group (container) (typed FeaturePython)
  n = 4
  ref = Cl_element
FEATURE [App::DocumentObjectGroupPython] G4_CARBON_TETRACHLORIDE  # scripted group (container) (typed FeaturePython)
  Dunit = g/cm3
  Dvalue = 1.594
  Group = -> [C_element024,Cl_element004]
  conduct = 2
  density = 1
  expand = 3
  formula = G4_CARBON_TETRACHLORIDE
  name = G4_CARBON_TETRACHLORIDE
  specific = 4
FEATURE [App::DocumentObjectGroupPython] C_element025  label="C_element : 012"  # scripted group (container) (typed FeaturePython)
  n = 6
  ref = C_element
FEATURE [App::DocumentObjectGroupPython] H_element021  label="H_element : 012"  # scripted group (container) (typed FeaturePython)
  n = 10
  ref = H_element
FEATURE [App::DocumentObjectGroupPython] O_element026  label="O_element : 5"  # scripted group (container) (typed FeaturePython)
  n = 5
  ref = O_element
FEATURE [App::DocumentObjectGroupPython] G4_CELLULOSE_CELLOPHANE  # scripted group (container) (typed FeaturePython)
  Dunit = g/cm3
  Dvalue = 1.42
  Group = -> [C_element025,H_element021,O_element026]
  conduct = 2
  density = 1
  expand = 3
  formula = G4_CELLULOSE_CELLOPHANE
  name = G4_CELLULOSE_CELLOPHANE
  specific = 4
FEATURE [App::DocumentObjectGroupPython] H_element022  label="H_element : 0.067"  # scripted group (container) (typed FeaturePython)
  n = 0.067125
FEATURE [App::DocumentObjectGroupPython] C_element026  label="C_element : 0.545"  # scripted group (container) (typed FeaturePython)
  n = 0.545403
FEATURE [App::DocumentObjectGroupPython] O_element027  label="O_element : 0.387"  # scripted group (container) (typed FeaturePython)
  n = 0.387472
FEATURE [App::DocumentObjectGroupPython] G4_CELLULOSE_BUTYRATE  # scripted group (container) (typed FeaturePython)
  Dunit = g/cm3
  Dvalue = 1.2
  Group = -> [H_element022,C_element026,O_element027]
  conduct = 2
  density = 1
  expand = 3
  formula = G4_CELLULOSE_BUTYRATE
  name = G4_CELLULOSE_BUTYRATE
  specific = 4
FEATURE [App::DocumentObjectGroupPython] H_element023  label="H_element : 0.029"  # scripted group (container) (typed FeaturePython)
  n = 0.029216
FEATURE [App::DocumentObjectGroupPython] C_element027  label="C_element : 0.271"  # scripted group (container) (typed FeaturePython)
  n = 0.271296
FEATURE [App::DocumentObjectGroupPython] N_element013  label="N_element : 0.121"  # scripted group (container) (typed FeaturePython)
  n = 0.121276
FEATURE [App::DocumentObjectGroupPython] O_element028  label="O_element : 0.578"  # scripted group (container) (typed FeaturePython)
  n = 0.578212
FEATURE [App::DocumentObjectGroupPython] G4_CELLULOSE_NITRATE  # scripted group (container) (typed FeaturePython)
  Dunit = g/cm3
  Dvalue = 1.49
  Group = -> [H_element023,C_element027,N_element013,O_element028]
  conduct = 2
  density = 1
  expand = 3
  formula = G4_CELLULOSE_NITRATE
  name = G4_CELLULOSE_NITRATE
  specific = 4
FEATURE [App::DocumentObjectGroupPython] H_element024  label="H_element : 0.108"  # scripted group (container) (typed FeaturePython)
  n = 0.107596
FEATURE [App::DocumentObjectGroupPython] N_element014  label="N_element : 0.001"  # scripted group (container) (typed FeaturePython)
  n = 0.0008
FEATURE [App::DocumentObjectGroupPython] O_element029  label="O_element : 0.875"  # scripted group (container) (typed FeaturePython)
  n = 0.874976
FEATURE [App::DocumentObjectGroupPython] S_element008  label="S_element : 0.015"  # scripted group (container) (typed FeaturePython)
  n = 0.014627
FEATURE [App::DocumentObjectGroupPython] Ce_element001  label="Ce_element : 0.002"  # scripted group (container) (typed FeaturePython)
  n = 0.002001
FEATURE [App::DocumentObjectGroupPython] G4_CERIC_SULFATE  # scripted group (container) (typed FeaturePython)
  Dunit = g/cm3
  Dvalue = 1.03
  Group = -> [H_element024,N_element014,O_element029,S_element008,Ce_element001]
  conduct = 2
  density = 1
  expand = 3
  formula = G4_CERIC_SULFATE
  name = G4_CERIC_SULFATE
  specific = 4
FEATURE [App::DocumentObjectGroupPython] Cs_element001  label="Cs_element : 1"  # scripted group (container) (typed FeaturePython)
  n = 1
  ref = Cs_element
FEATURE [App::DocumentObjectGroupPython] F_element006  label="F_element : 1"  # scripted group (container) (typed FeaturePython)
  n = 1
  ref = F_element
FEATURE [App::DocumentObjectGroupPython] G4_CESIUM_FLUORIDE  # scripted group (container) (typed FeaturePython)
  Dunit = g/cm3
  Dvalue = 4.115
  Group = -> [Cs_element001,F_element006]
  conduct = 2
  density = 1
  expand = 3
  formula = G4_CESIUM_FLUORIDE
  name = G4_CESIUM_FLUORIDE
  specific = 4
FEATURE [App::DocumentObjectGroupPython] Cs_element002  label="Cs_element : 002"  # scripted group (container) (typed FeaturePython)
  n = 1
  ref = Cs_element
FEATURE [App::DocumentObjectGroupPython] I_element001  label="I_element : 1"  # scripted group (container) (typed FeaturePython)
  n = 1
  ref = I_element
FEATURE [App::DocumentObjectGroupPython] G4_CESIUM_IODIDE  # scripted group (container) (typed FeaturePython)
  Dunit = g/cm3
  Dvalue = 4.51
  Group = -> [Cs_element002,I_element001]
  conduct = 2
  density = 1
  expand = 3
  formula = G4_CESIUM_IODIDE
  name = G4_CESIUM_IODIDE
  specific = 4
FEATURE [App::DocumentObjectGroupPython] C_element028  label="C_element : 013"  # scripted group (container) (typed FeaturePython)
  n = 6
  ref = C_element
FEATURE [App::DocumentObjectGroupPython] H_element025  label="H_element : 013"  # scripted group (container) (typed FeaturePython)
  n = 5
  ref = H_element
FEATURE [App::DocumentObjectGroupPython] Cl_element005  label="Cl_element : 1"  # scripted group (container) (typed FeaturePython)
  n = 1
  ref = Cl_element
FEATURE [App::DocumentObjectGroupPython] G4_CHLOROBENZENE  # scripted group (container) (typed FeaturePython)
  Dunit = g/cm3
  Dvalue = 1.1058
  Group = -> [C_element028,H_element025,Cl_element005]
  conduct = 2
  density = 1
  expand = 3
  formula = G4_CHLOROBENZENE
  name = G4_CHLOROBENZENE
  specific = 4
FEATURE [App::DocumentObjectGroupPython] C_element029  label="C_element : 014"  # scripted group (container) (typed FeaturePython)
  n = 1
  ref = C_element
FEATURE [App::DocumentObjectGroupPython] H_element026  label="H_element : 1"  # scripted group (container) (typed FeaturePython)
  n = 1
  ref = H_element
FEATURE [App::DocumentObjectGroupPython] Cl_element006  label="Cl_element : 3"  # scripted group (container) (typed FeaturePython)
  n = 3
  ref = Cl_element
FEATURE [App::DocumentObjectGroupPython] G4_CHLOROFORM  # scripted group (container) (typed FeaturePython)
  Dunit = g/cm3
  Dvalue = 1.4832
  Group = -> [C_element029,H_element026,Cl_element006]
  conduct = 2
  density = 1
  expand = 3
  formula = G4_CHLOROFORM
  name = G4_CHLOROFORM
  specific = 4
FEATURE [App::DocumentObjectGroupPython] H_element027  label="H_element : 0.010"  # scripted group (container) (typed FeaturePython)
  n = 0.01
FEATURE [App::DocumentObjectGroupPython] C_element030  label="C_element : 0.001"  # scripted group (container) (typed FeaturePython)
  n = 0.001
FEATURE [App::DocumentObjectGroupPython] O_element030  label="O_element : 0.529"  # scripted group (container) (typed FeaturePython)
  n = 0.529107
FEATURE [App::DocumentObjectGroupPython] Na_element005  label="Na_element : 0.016"  # scripted group (container) (typed FeaturePython)
  n = 0.016
FEATURE [App::DocumentObjectGroupPython] Mg_element003  label="Mg_element : 0.004"  # scripted group (container) (typed FeaturePython)
  n = 0.002
FEATURE [App::DocumentObjectGroupPython] Al_element002  label="Al_element : 0.034"  # scripted group (container) (typed FeaturePython)
  n = 0.033872
FEATURE [App::DocumentObjectGroupPython] Si_element002  label="Si_element : 0.337"  # scripted group (container) (typed FeaturePython)
  n = 0.337021
FEATURE [App::DocumentObjectGroupPython] K_element003  label="K_element : 0.013"  # scripted group (container) (typed FeaturePython)
  n = 0.013
FEATURE [App::DocumentObjectGroupPython] Ca_element010  label="Ca_element : 0.044"  # scripted group (container) (typed FeaturePython)
  n = 0.044
FEATURE [App::DocumentObjectGroupPython] Fe_element002  label="Fe_element : 0.014"  # scripted group (container) (typed FeaturePython)
  n = 0.014
FEATURE [App::DocumentObjectGroupPython] G4_CONCRETE  # scripted group (container) (typed FeaturePython)
  Dunit = g/cm3
  Dvalue = 2.3
  Group = -> [H_element027,C_element030,O_element030,Na_element005,Mg_element003,Al_element002,Si_element002,K_element003,Ca_element010,Fe_element002]
  conduct = 2
  density = 1
  expand = 3
  formula = G4_CONCRETE
  name = G4_CONCRETE
  specific = 4
FEATURE [App::DocumentObjectGroupPython] C_element031  label="C_element : 015"  # scripted group (container) (typed FeaturePython)
  n = 6
  ref = C_element
FEATURE [App::DocumentObjectGroupPython] H_element028  label="H_element : 12"  # scripted group (container) (typed FeaturePython)
  n = 12
  ref = H_element
FEATURE [App::DocumentObjectGroupPython] G4_CYCLOHEXANE  # scripted group (container) (typed FeaturePython)
  Dunit = g/cm3
  Dvalue = 0.779
  Group = -> [C_element031,H_element028]
  conduct = 2
  density = 1
  expand = 3
  formula = G4_CYCLOHEXANE
  name = G4_CYCLOHEXANE
  specific = 4
FEATURE [App::DocumentObjectGroupPython] C_element032  label="C_element : 016"  # scripted group (container) (typed FeaturePython)
  n = 6
  ref = C_element
FEATURE [App::DocumentObjectGroupPython] H_element029  label="H_element : 4"  # scripted group (container) (typed FeaturePython)
  n = 4
  ref = H_element
FEATURE [App::DocumentObjectGroupPython] Cl_element007  label="Cl_element : 2"  # scripted group (container) (typed FeaturePython)
  n = 2
  ref = Cl_element
FEATURE [App::DocumentObjectGroupPython] G4_1_2_DICHLOROBENZENE  label="G4_1.2-DICHLOROBENZENE"  # scripted group (container) (typed FeaturePython)
  Dunit = g/cm3
  Dvalue = 1.3048
  Group = -> [C_element032,H_element029,Cl_element007]
  conduct = 2
  density = 1
  expand = 3
  formula = G4_1.2-DICHLOROBENZENE
  name = G4_1.2-DICHLOROBENZENE
  specific = 4
FEATURE [App::DocumentObjectGroupPython] C_element033  label="C_element : 017"  # scripted group (container) (typed FeaturePython)
  n = 4
  ref = C_element
FEATURE [App::DocumentObjectGroupPython] H_element030  label="H_element : 8"  # scripted group (container) (typed FeaturePython)
  n = 8
  ref = H_element
FEATURE [App::DocumentObjectGroupPython] O_element031  label="O_element : 014"  # scripted group (container) (typed FeaturePython)
  n = 1
  ref = O_element
FEATURE [App::DocumentObjectGroupPython] Cl_element008  label="Cl_element : 005"  # scripted group (container) (typed FeaturePython)
  n = 2
  ref = Cl_element
FEATURE [App::DocumentObjectGroupPython] G4_DICHLORODIETHYL_ETHER  # scripted group (container) (typed FeaturePython)
  Dunit = g/cm3
  Dvalue = 1.2199
  Group = -> [C_element033,H_element030,O_element031,Cl_element008]
  conduct = 2
  density = 1
  expand = 3
  formula = G4_DICHLORODIETHYL_ETHER
  name = G4_DICHLORODIETHYL_ETHER
  specific = 4
FEATURE [App::DocumentObjectGroupPython] C_element034  label="C_element : 018"  # scripted group (container) (typed FeaturePython)
  n = 2
  ref = C_element
FEATURE [App::DocumentObjectGroupPython] H_element031  label="H_element : 014"  # scripted group (container) (typed FeaturePython)
  n = 4
  ref = H_element
FEATURE [App::DocumentObjectGroupPython] Cl_element009  label="Cl_element : 006"  # scripted group (container) (typed FeaturePython)
  n = 2
  ref = Cl_element
FEATURE [App::DocumentObjectGroupPython] G4_1_2_DICHLOROETHANE  label="G4_1.2-DICHLOROETHANE"  # scripted group (container) (typed FeaturePython)
  Dunit = g/cm3
  Dvalue = 1.2351
  Group = -> [C_element034,H_element031,Cl_element009]
  conduct = 2
  density = 1
  expand = 3
  formula = G4_1.2-DICHLOROETHANE
  name = G4_1.2-DICHLOROETHANE
  specific = 4
FEATURE [App::DocumentObjectGroupPython] C_element035  label="C_element : 019"  # scripted group (container) (typed FeaturePython)
  n = 4
  ref = C_element
FEATURE [App::DocumentObjectGroupPython] H_element032  label="H_element : 015"  # scripted group (container) (typed FeaturePython)
  n = 10
  ref = H_element
FEATURE [App::DocumentObjectGroupPython] O_element032  label="O_element : 015"  # scripted group (container) (typed FeaturePython)
  n = 1
  ref = O_element
FEATURE [App::DocumentObjectGroupPython] G4_DIETHYL_ETHER  # scripted group (container) (typed FeaturePython)
  Dunit = g/cm3
  Dvalue = 0.71378
  Group = -> [C_element035,H_element032,O_element032]
  conduct = 2
  density = 1
  expand = 3
  formula = G4_DIETHYL_ETHER
  name = G4_DIETHYL_ETHER
  specific = 4
FEATURE [App::DocumentObjectGroupPython] C_element036  label="C_element : 020"  # scripted group (container) (typed FeaturePython)
  n = 3
  ref = C_element
FEATURE [App::DocumentObjectGroupPython] H_element033  label="H_element : 016"  # scripted group (container) (typed FeaturePython)
  n = 7
  ref = H_element
FEATURE [App::DocumentObjectGroupPython] N_element015  label="N_element : 008"  # scripted group (container) (typed FeaturePython)
  n = 1
  ref = N_element
FEATURE [App::DocumentObjectGroupPython] O_element033  label="O_element : 016"  # scripted group (container) (typed FeaturePython)
  n = 1
  ref = O_element
FEATURE [App::DocumentObjectGroupPython] G4_N_N_DIMETHYL_FORMAMIDE  label="G4_N.N-DIMETHYL_FORMAMIDE"  # scripted group (container) (typed FeaturePython)
  Dunit = g/cm3
  Dvalue = 0.9487
  Group = -> [C_element036,H_element033,N_element015,O_element033]
  conduct = 2
  density = 1
  expand = 3
  formula = G4_N.N-DIMETHYL_FORMAMIDE
  name = G4_N.N-DIMETHYL_FORMAMIDE
  specific = 4
FEATURE [App::DocumentObjectGroupPython] C_element037  label="C_element : 021"  # scripted group (container) (typed FeaturePython)
  n = 2
  ref = C_element
FEATURE [App::DocumentObjectGroupPython] H_element034  label="H_element : 017"  # scripted group (container) (typed FeaturePython)
  n = 6
  ref = H_element
FEATURE [App::DocumentObjectGroupPython] O_element034  label="O_element : 017"  # scripted group (container) (typed FeaturePython)
  n = 1
  ref = O_element
FEATURE [App::DocumentObjectGroupPython] S_element009  label="S_element : 003"  # scripted group (container) (typed FeaturePython)
  n = 1
  ref = S_element
FEATURE [App::DocumentObjectGroupPython] G4_DIMETHYL_SULFOXIDE  # scripted group (container) (typed FeaturePython)
  Dunit = g/cm3
  Dvalue = 1.1014
  Group = -> [C_element037,H_element034,O_element034,S_element009]
  conduct = 2
  density = 1
  expand = 3
  formula = G4_DIMETHYL_SULFOXIDE
  name = G4_DIMETHYL_SULFOXIDE
  specific = 4
FEATURE [App::DocumentObjectGroupPython] C_element038  label="C_element : 022"  # scripted group (container) (typed FeaturePython)
  n = 2
  ref = C_element
FEATURE [App::DocumentObjectGroupPython] H_element035  label="H_element : 018"  # scripted group (container) (typed FeaturePython)
  n = 6
  ref = H_element
FEATURE [App::DocumentObjectGroupPython] G4_ETHANE  # scripted group (container) (typed FeaturePython)
  Dunit = g/cm3
  Dvalue = 0.00125324
  Group = -> [C_element038,H_element035]
  conduct = 2
  density = 1
  expand = 3
  formula = G4_ETHANE
  name = G4_ETHANE
  specific = 4
FEATURE [App::DocumentObjectGroupPython] C_element039  label="C_element : 023"  # scripted group (container) (typed FeaturePython)
  n = 2
  ref = C_element
FEATURE [App::DocumentObjectGroupPython] H_element036  label="H_element : 019"  # scripted group (container) (typed FeaturePython)
  n = 6
  ref = H_element
FEATURE [App::DocumentObjectGroupPython] O_element035  label="O_element : 018"  # scripted group (container) (typed FeaturePython)
  n = 1
  ref = O_element
FEATURE [App::DocumentObjectGroupPython] G4_ETHYL_ALCOHOL  # scripted group (container) (typed FeaturePython)
  Dunit = g/cm3
  Dvalue = 0.7893
  Group = -> [C_element039,H_element036,O_element035]
  conduct = 2
  density = 1
  expand = 3
  formula = G4_ETHYL_ALCOHOL
  name = G4_ETHYL_ALCOHOL
  specific = 4
FEATURE [App::DocumentObjectGroupPython] H_element037  label="H_element : 0.090"  # scripted group (container) (typed FeaturePython)
  n = 0.090027
FEATURE [App::DocumentObjectGroupPython] C_element040  label="C_element : 0.585"  # scripted group (container) (typed FeaturePython)
  n = 0.585182
FEATURE [App::DocumentObjectGroupPython] O_element036  label="O_element : 0.325"  # scripted group (container) (typed FeaturePython)
  n = 0.324791
FEATURE [App::DocumentObjectGroupPython] G4_ETHYL_CELLULOSE  # scripted group (container) (typed FeaturePython)
  Dunit = g/cm3
  Dvalue = 1.13
  Group = -> [H_element037,C_element040,O_element036]
  conduct = 2
  density = 1
  expand = 3
  formula = G4_ETHYL_CELLULOSE
  name = G4_ETHYL_CELLULOSE
  specific = 4
FEATURE [App::DocumentObjectGroupPython] C_element041  label="C_element : 024"  # scripted group (container) (typed FeaturePython)
  n = 2
  ref = C_element
FEATURE [App::DocumentObjectGroupPython] H_element038  label="H_element : 020"  # scripted group (container) (typed FeaturePython)
  n = 4
  ref = H_element
FEATURE [App::DocumentObjectGroupPython] G4_ETHYLENE  # scripted group (container) (typed FeaturePython)
  Dunit = g/cm3
  Dvalue = 0.00117497
  Group = -> [C_element041,H_element038]
  conduct = 2
  density = 1
  expand = 3
  formula = G4_ETHYLENE
  name = G4_ETHYLENE
  specific = 4
FEATURE [App::DocumentObjectGroupPython] H_element039  label="H_element : 0.096"  # scripted group (container) (typed FeaturePython)
  n = 0.096
FEATURE [App::DocumentObjectGroupPython] C_element042  label="C_element : 0.195"  # scripted group (container) (typed FeaturePython)
  n = 0.195
FEATURE [App::DocumentObjectGroupPython] N_element016  label="N_element : 0.057"  # scripted group (container) (typed FeaturePython)
  n = 0.057
FEATURE [App::DocumentObjectGroupPython] O_element037  label="O_element : 0.646"  # scripted group (container) (typed FeaturePython)
  n = 0.646
FEATURE [App::DocumentObjectGroupPython] Na_element006  label="Na_element : 0.017"  # scripted group (container) (typed FeaturePython)
  n = 0.001
FEATURE [App::DocumentObjectGroupPython] P_element005  label="P_element : 0.104"  # scripted group (container) (typed FeaturePython)
  n = 0.001
FEATURE [App::DocumentObjectGroupPython] S_element010  label="S_element : 0.016"  # scripted group (container) (typed FeaturePython)
  n = 0.003
FEATURE [App::DocumentObjectGroupPython] Cl_element010  label="Cl_element : 0.005"  # scripted group (container) (typed FeaturePython)
  n = 0.001
FEATURE [App::DocumentObjectGroupPython] G4_EYE_LENS_ICRP  # scripted group (container) (typed FeaturePython)
  Dunit = g/cm3
  Dvalue = 1.07
  Group = -> [H_element039,C_element042,N_element016,O_element037,Na_element006,P_element005,S_element010,Cl_element010]
  conduct = 2
  density = 1
  expand = 3
  formula = G4_EYE_LENS_ICRP
  name = G4_EYE_LENS_ICRP
  specific = 4
FEATURE [App::DocumentObjectGroupPython] Fe_element003  label="Fe_element : 2"  # scripted group (container) (typed FeaturePython)
  n = 2
  ref = Fe_element
FEATURE [App::DocumentObjectGroupPython] O_element038  label="O_element : 019"  # scripted group (container) (typed FeaturePython)
  n = 3
  ref = O_element
FEATURE [App::DocumentObjectGroupPython] G4_FERRIC_OXIDE  # scripted group (container) (typed FeaturePython)
  Dunit = g/cm3
  Dvalue = 5.2
  Group = -> [Fe_element003,O_element038]
  conduct = 2
  density = 1
  expand = 3
  formula = G4_FERRIC_OXIDE
  name = G4_FERRIC_OXIDE
  specific = 4
FEATURE [App::DocumentObjectGroupPython] Fe_element004  label="Fe_element : 1"  # scripted group (container) (typed FeaturePython)
  n = 1
  ref = Fe_element
FEATURE [App::DocumentObjectGroupPython] B_element003  label="B_element : 1"  # scripted group (container) (typed FeaturePython)
  n = 1
  ref = B_element
FEATURE [App::DocumentObjectGroupPython] G4_FERROBORIDE  # scripted group (container) (typed FeaturePython)
  Dunit = g/cm3
  Dvalue = 7.15
  Group = -> [Fe_element004,B_element003]
  conduct = 2
  density = 1
  expand = 3
  formula = G4_FERROBORIDE
  name = G4_FERROBORIDE
  specific = 4
FEATURE [App::DocumentObjectGroupPython] Fe_element005  label="Fe_element : 003"  # scripted group (container) (typed FeaturePython)
  n = 1
  ref = Fe_element
FEATURE [App::DocumentObjectGroupPython] O_element039  label="O_element : 020"  # scripted group (container) (typed FeaturePython)
  n = 1
  ref = O_element
FEATURE [App::DocumentObjectGroupPython] G4_FERROUS_OXIDE  # scripted group (container) (typed FeaturePython)
  Dunit = g/cm3
  Dvalue = 5.7
  Group = -> [Fe_element005,O_element039]
  conduct = 2
  density = 1
  expand = 3
  formula = G4_FERROUS_OXIDE
  name = G4_FERROUS_OXIDE
  specific = 4
FEATURE [App::DocumentObjectGroupPython] H_element040  label="H_element : 0.115"  # scripted group (container) (typed FeaturePython)
  n = 0.108259
FEATURE [App::DocumentObjectGroupPython] N_element017  label="N_element : 0.000"  # scripted group (container) (typed FeaturePython)
  n = 2.7e-05
FEATURE [App::DocumentObjectGroupPython] O_element040  label="O_element : 0.879"  # scripted group (container) (typed FeaturePython)
  n = 0.878636
FEATURE [App::DocumentObjectGroupPython] Na_element007  label="Na_element : 0.000"  # scripted group (container) (typed FeaturePython)
  n = 2.2e-05
FEATURE [App::DocumentObjectGroupPython] S_element011  label="S_element : 0.013"  # scripted group (container) (typed FeaturePython)
  n = 0.012968
FEATURE [App::DocumentObjectGroupPython] Cl_element011  label="Cl_element : 0.000"  # scripted group (container) (typed FeaturePython)
  n = 3.4e-05
FEATURE [App::DocumentObjectGroupPython] Fe_element006  label="Fe_element : 0.000"  # scripted group (container) (typed FeaturePython)
  n = 5.4e-05
FEATURE [App::DocumentObjectGroupPython] G4_FERROUS_SULFATE  # scripted group (container) (typed FeaturePython)
  Dunit = g/cm3
  Dvalue = 1.024
  Group = -> [H_element040,N_element017,O_element040,Na_element007,S_element011,Cl_element011,Fe_element006]
  conduct = 2
  density = 1
  expand = 3
  formula = G4_FERROUS_SULFATE
  name = G4_FERROUS_SULFATE
  specific = 4
FEATURE [App::DocumentObjectGroupPython] C_element043  label="C_element : 0.099"  # scripted group (container) (typed FeaturePython)
  n = 0.099335
FEATURE [App::DocumentObjectGroupPython] F_element007  label="F_element : 0.314"  # scripted group (container) (typed FeaturePython)
  n = 0.314247
FEATURE [App::DocumentObjectGroupPython] Cl_element012  label="Cl_element : 0.586"  # scripted group (container) (typed FeaturePython)
  n = 0.586418
FEATURE [App::DocumentObjectGroupPython] G4_FREON_12  label="G4_FREON-12"  # scripted group (container) (typed FeaturePython)
  Dunit = g/cm3
  Dvalue = 1.12
  Group = -> [C_element043,F_element007,Cl_element012]
  conduct = 2
  density = 1
  expand = 3
  formula = G4_FREON-12
  name = G4_FREON-12
  specific = 4
FEATURE [App::DocumentObjectGroupPython] C_element044  label="C_element : 0.057"  # scripted group (container) (typed FeaturePython)
  n = 0.057245
FEATURE [App::DocumentObjectGroupPython] F_element008  label="F_element : 0.181"  # scripted group (container) (typed FeaturePython)
  n = 0.181096
FEATURE [App::DocumentObjectGroupPython] Br_element001  label="Br_element : 0.762"  # scripted group (container) (typed FeaturePython)
  n = 0.761659
FEATURE [App::DocumentObjectGroupPython] G4_FREON_12B2  label="G4_FREON-12B2"  # scripted group (container) (typed FeaturePython)
  Dunit = g/cm3
  Dvalue = 1.8
  Group = -> [C_element044,F_element008,Br_element001]
  conduct = 2
  density = 1
  expand = 3
  formula = G4_FREON-12B2
  name = G4_FREON-12B2
  specific = 4
FEATURE [App::DocumentObjectGroupPython] C_element045  label="C_element : 0.115"  # scripted group (container) (typed FeaturePython)
  n = 0.114983
FEATURE [App::DocumentObjectGroupPython] F_element009  label="F_element : 0.546"  # scripted group (container) (typed FeaturePython)
  n = 0.545621
FEATURE [App::DocumentObjectGroupPython] Cl_element013  label="Cl_element : 0.339"  # scripted group (container) (typed FeaturePython)
  n = 0.339396
FEATURE [App::DocumentObjectGroupPython] G4_FREON_13  label="G4_FREON-13"  # scripted group (container) (typed FeaturePython)
  Dunit = g/cm3
  Dvalue = 0.95
  Group = -> [C_element045,F_element009,Cl_element013]
  conduct = 2
  density = 1
  expand = 3
  formula = G4_FREON-13
  name = G4_FREON-13
  specific = 4
FEATURE [App::DocumentObjectGroupPython] C_element046  label="C_element : 025"  # scripted group (container) (typed FeaturePython)
  n = 1
  ref = C_element
FEATURE [App::DocumentObjectGroupPython] F_element010  label="F_element : 3"  # scripted group (container) (typed FeaturePython)
  n = 3
  ref = F_element
FEATURE [App::DocumentObjectGroupPython] Br_element002  label="Br_element : 1"  # scripted group (container) (typed FeaturePython)
  n = 1
  ref = Br_element
FEATURE [App::DocumentObjectGroupPython] G4_FREON_13B1  label="G4_FREON-13B1"  # scripted group (container) (typed FeaturePython)
  Dunit = g/cm3
  Dvalue = 1.5
  Group = -> [C_element046,F_element010,Br_element002]
  conduct = 2
  density = 1
  expand = 3
  formula = G4_FREON-13B1
  name = G4_FREON-13B1
  specific = 4
FEATURE [App::DocumentObjectGroupPython] C_element047  label="C_element : 0.061"  # scripted group (container) (typed FeaturePython)
  n = 0.061309
FEATURE [App::DocumentObjectGroupPython] F_element011  label="F_element : 0.291"  # scripted group (container) (typed FeaturePython)
  n = 0.290924
FEATURE [App::DocumentObjectGroupPython] I_element002  label="I_element : 0.648"  # scripted group (container) (typed FeaturePython)
  n = 0.647767
FEATURE [App::DocumentObjectGroupPython] G4_FREON_13I1  label="G4_FREON-13I1"  # scripted group (container) (typed FeaturePython)
  Dunit = g/cm3
  Dvalue = 1.8
  Group = -> [C_element047,F_element011,I_element002]
  conduct = 2
  density = 1
  expand = 3
  formula = G4_FREON-13I1
  name = G4_FREON-13I1
  specific = 4
FEATURE [App::DocumentObjectGroupPython] Gd_element001  label="Gd_element : 2"  # scripted group (container) (typed FeaturePython)
  n = 2
  ref = Gd_element
FEATURE [App::DocumentObjectGroupPython] O_element041  label="O_element : 021"  # scripted group (container) (typed FeaturePython)
  n = 2
  ref = O_element
FEATURE [App::DocumentObjectGroupPython] S_element012  label="S_element : 004"  # scripted group (container) (typed FeaturePython)
  n = 1
  ref = S_element
FEATURE [App::DocumentObjectGroupPython] G4_GADOLINIUM_OXYSULFIDE  # scripted group (container) (typed FeaturePython)
  Dunit = g/cm3
  Dvalue = 7.44
  Group = -> [Gd_element001,O_element041,S_element012]
  conduct = 2
  density = 1
  expand = 3
  formula = G4_GADOLINIUM_OXYSULFIDE
  name = G4_GADOLINIUM_OXYSULFIDE
  specific = 4
FEATURE [App::DocumentObjectGroupPython] Ga_element001  label="Ga_element : 1"  # scripted group (container) (typed FeaturePython)
  n = 1
  ref = Ga_element
FEATURE [App::DocumentObjectGroupPython] As_element001  label="As_element : 1"  # scripted group (container) (typed FeaturePython)
  n = 1
  ref = As_element
FEATURE [App::DocumentObjectGroupPython] G4_GALLIUM_ARSENIDE  # scripted group (container) (typed FeaturePython)
  Dunit = g/cm3
  Dvalue = 5.31
  Group = -> [Ga_element001,As_element001]
  conduct = 2
  density = 1
  expand = 3
  formula = G4_GALLIUM_ARSENIDE
  name = G4_GALLIUM_ARSENIDE
  specific = 4
FEATURE [App::DocumentObjectGroupPython] H_element041  label="H_element : 0.081"  # scripted group (container) (typed FeaturePython)
  n = 0.08118
FEATURE [App::DocumentObjectGroupPython] C_element048  label="C_element : 0.416"  # scripted group (container) (typed FeaturePython)
  n = 0.41606
FEATURE [App::DocumentObjectGroupPython] N_element018  label="N_element : 0.111"  # scripted group (container) (typed FeaturePython)
  n = 0.11124
FEATURE [App::DocumentObjectGroupPython] O_element042  label="O_element : 0.381"  # scripted group (container) (typed FeaturePython)
  n = 0.38064
FEATURE [App::DocumentObjectGroupPython] S_element013  label="S_element : 0.011"  # scripted group (container) (typed FeaturePython)
  n = 0.01088
FEATURE [App::DocumentObjectGroupPython] G4_GEL_PHOTO_EMULSION  # scripted group (container) (typed FeaturePython)
  Dunit = g/cm3
  Dvalue = 1.2914
  Group = -> [H_element041,C_element048,N_element018,O_element042,S_element013]
  conduct = 2
  density = 1
  expand = 3
  formula = G4_GEL_PHOTO_EMULSION
  name = G4_GEL_PHOTO_EMULSION
  specific = 4
FEATURE [App::DocumentObjectGroupPython] B_element004  label="B_element : 0.040"  # scripted group (container) (typed FeaturePython)
  n = 0.0400639
FEATURE [App::DocumentObjectGroupPython] O_element043  label="O_element : 0.540"  # scripted group (container) (typed FeaturePython)
  n = 0.539561
FEATURE [App::DocumentObjectGroupPython] Na_element008  label="Na_element : 0.028"  # scripted group (container) (typed FeaturePython)
  n = 0.0281909
FEATURE [App::DocumentObjectGroupPython] Al_element003  label="Al_element : 0.012"  # scripted group (container) (typed FeaturePython)
  n = 0.011644
FEATURE [App::DocumentObjectGroupPython] Si_element003  label="Si_element : 0.377"  # scripted group (container) (typed FeaturePython)
  n = 0.377219
FEATURE [App::DocumentObjectGroupPython] K_element004  label="K_element : 0.014"  # scripted group (container) (typed FeaturePython)
  n = 0.00332099
FEATURE [App::DocumentObjectGroupPython] G4_Pyrex_Glass  # scripted group (container) (typed FeaturePython)
  Dunit = g/cm3
  Dvalue = 2.23
  Group = -> [B_element004,O_element043,Na_element008,Al_element003,Si_element003,K_element004]
  conduct = 2
  density = 1
  expand = 3
  formula = G4_Pyrex_Glass
  name = G4_Pyrex_Glass
  specific = 4
FEATURE [App::DocumentObjectGroupPython] O_element044  label="O_element : 0.156"  # scripted group (container) (typed FeaturePython)
  n = 0.156453
FEATURE [App::DocumentObjectGroupPython] Si_element004  label="Si_element : 0.081"  # scripted group (container) (typed FeaturePython)
  n = 0.080866
FEATURE [App::DocumentObjectGroupPython] Ti_element001  label="Ti_element : 0.008"  # scripted group (container) (typed FeaturePython)
  n = 0.008092
FEATURE [App::DocumentObjectGroupPython] As_element002  label="As_element : 0.003"  # scripted group (container) (typed FeaturePython)
  n = 0.002651
FEATURE [App::DocumentObjectGroupPython] Pb_element001  label="Pb_element : 0.752"  # scripted group (container) (typed FeaturePython)
  n = 0.751938
FEATURE [App::DocumentObjectGroupPython] G4_GLASS_LEAD  # scripted group (container) (typed FeaturePython)
  Dunit = g/cm3
  Dvalue = 6.22
  Group = -> [O_element044,Si_element004,Ti_element001,As_element002,Pb_element001]
  conduct = 2
  density = 1
  expand = 3
  formula = G4_GLASS_LEAD
  name = G4_GLASS_LEAD
  specific = 4
FEATURE [App::DocumentObjectGroupPython] O_element045  label="O_element : 0.460"  # scripted group (container) (typed FeaturePython)
  n = 0.4598
FEATURE [App::DocumentObjectGroupPython] Na_element009  label="Na_element : 0.096"  # scripted group (container) (typed FeaturePython)
  n = 0.0964411
FEATURE [App::DocumentObjectGroupPython] Si_element005  label="Si_element : 0.378"  # scripted group (container) (typed FeaturePython)
  n = 0.336553
FEATURE [App::DocumentObjectGroupPython] Ca_element011  label="Ca_element : 0.107"  # scripted group (container) (typed FeaturePython)
  n = 0.107205
FEATURE [App::DocumentObjectGroupPython] G4_GLASS_PLATE  # scripted group (container) (typed FeaturePython)
  Dunit = g/cm3
  Dvalue = 2.4
  Group = -> [O_element045,Na_element009,Si_element005,Ca_element011]
  conduct = 2
  density = 1
  expand = 3
  formula = G4_GLASS_PLATE
  name = G4_GLASS_PLATE
  specific = 4
FEATURE [App::DocumentObjectGroupPython] C_element049  label="C_element : 026"  # scripted group (container) (typed FeaturePython)
  n = 5
  ref = C_element
FEATURE [App::DocumentObjectGroupPython] H_element042  label="H_element : 021"  # scripted group (container) (typed FeaturePython)
  n = 10
  ref = H_element
FEATURE [App::DocumentObjectGroupPython] N_element019  label="N_element : 2"  # scripted group (container) (typed FeaturePython)
  n = 2
  ref = N_element
FEATURE [App::DocumentObjectGroupPython] O_element046  label="O_element : 022"  # scripted group (container) (typed FeaturePython)
  n = 3
  ref = O_element
FEATURE [App::DocumentObjectGroupPython] G4_GLUTAMINE  # scripted group (container) (typed FeaturePython)
  Dunit = g/cm3
  Dvalue = 1.46
  Group = -> [C_element049,H_element042,N_element019,O_element046]
  conduct = 2
  density = 1
  expand = 3
  formula = G4_GLUTAMINE
  name = G4_GLUTAMINE
  specific = 4
FEATURE [App::DocumentObjectGroupPython] C_element050  label="C_element : 027"  # scripted group (container) (typed FeaturePython)
  n = 3
  ref = C_element
FEATURE [App::DocumentObjectGroupPython] H_element043  label="H_element : 022"  # scripted group (container) (typed FeaturePython)
  n = 8
  ref = H_element
FEATURE [App::DocumentObjectGroupPython] O_element047  label="O_element : 023"  # scripted group (container) (typed FeaturePython)
  n = 3
  ref = O_element
FEATURE [App::DocumentObjectGroupPython] G4_GLYCEROL  # scripted group (container) (typed FeaturePython)
  Dunit = g/cm3
  Dvalue = 1.2613
  Group = -> [C_element050,H_element043,O_element047]
  conduct = 2
  density = 1
  expand = 3
  formula = G4_GLYCEROL
  name = G4_GLYCEROL
  specific = 4
FEATURE [App::DocumentObjectGroupPython] C_element051  label="C_element : 028"  # scripted group (container) (typed FeaturePython)
  n = 5
  ref = C_element
FEATURE [App::DocumentObjectGroupPython] H_element044  label="H_element : 023"  # scripted group (container) (typed FeaturePython)
  n = 5
  ref = H_element
FEATURE [App::DocumentObjectGroupPython] N_element020  label="N_element : 009"  # scripted group (container) (typed FeaturePython)
  n = 5
  ref = N_element
FEATURE [App::DocumentObjectGroupPython] O_element048  label="O_element : 024"  # scripted group (container) (typed FeaturePython)
  n = 1
  ref = O_element
FEATURE [App::DocumentObjectGroupPython] G4_GUANINE  # scripted group (container) (typed FeaturePython)
  Dunit = g/cm3
  Dvalue = 2.2
  Group = -> [C_element051,H_element044,N_element020,O_element048]
  conduct = 2
  density = 1
  expand = 3
  formula = G4_GUANINE
  name = G4_GUANINE
  specific = 4
FEATURE [App::DocumentObjectGroupPython] Ca_element012  label="Ca_element : 006"  # scripted group (container) (typed FeaturePython)
  n = 1
  ref = Ca_element
FEATURE [App::DocumentObjectGroupPython] S_element014  label="S_element : 005"  # scripted group (container) (typed FeaturePython)
  n = 1
  ref = S_element
FEATURE [App::DocumentObjectGroupPython] O_element049  label="O_element : 6"  # scripted group (container) (typed FeaturePython)
  n = 6
  ref = O_element
FEATURE [App::DocumentObjectGroupPython] H_element045  label="H_element : 024"  # scripted group (container) (typed FeaturePython)
  n = 4
  ref = H_element
FEATURE [App::DocumentObjectGroupPython] G4_GYPSUM  # scripted group (container) (typed FeaturePython)
  Dunit = g/cm3
  Dvalue = 2.32
  Group = -> [Ca_element012,S_element014,O_element049,H_element045]
  conduct = 2
  density = 1
  expand = 3
  formula = G4_GYPSUM
  name = G4_GYPSUM
  specific = 4
FEATURE [App::DocumentObjectGroupPython] C_element052  label="C_element : 7"  # scripted group (container) (typed FeaturePython)
  n = 7
  ref = C_element
FEATURE [App::DocumentObjectGroupPython] H_element046  label="H_element : 16"  # scripted group (container) (typed FeaturePython)
  n = 16
  ref = H_element
FEATURE [App::DocumentObjectGroupPython] G4_N_HEPTANE  label="G4_N-HEPTANE"  # scripted group (container) (typed FeaturePython)
  Dunit = g/cm3
  Dvalue = 0.68376
  Group = -> [C_element052,H_element046]
  conduct = 2
  density = 1
  expand = 3
  formula = G4_N-HEPTANE
  name = G4_N-HEPTANE
  specific = 4
FEATURE [App::DocumentObjectGroupPython] C_element053  label="C_element : 029"  # scripted group (container) (typed FeaturePython)
  n = 6
  ref = C_element
FEATURE [App::DocumentObjectGroupPython] H_element047  label="H_element : 14"  # scripted group (container) (typed FeaturePython)
  n = 14
  ref = H_element
FEATURE [App::DocumentObjectGroupPython] G4_N_HEXANE  label="G4_N-HEXANE"  # scripted group (container) (typed FeaturePython)
  Dunit = g/cm3
  Dvalue = 0.6603
  Group = -> [C_element053,H_element047]
  conduct = 2
  density = 1
  expand = 3
  formula = G4_N-HEXANE
  name = G4_N-HEXANE
  specific = 4
FEATURE [App::DocumentObjectGroupPython] C_element054  label="C_element : 22"  # scripted group (container) (typed FeaturePython)
  n = 22
  ref = C_element
FEATURE [App::DocumentObjectGroupPython] H_element048  label="H_element : 025"  # scripted group (container) (typed FeaturePython)
  n = 10
  ref = H_element
FEATURE [App::DocumentObjectGroupPython] N_element021  label="N_element : 010"  # scripted group (container) (typed FeaturePython)
  n = 2
  ref = N_element
FEATURE [App::DocumentObjectGroupPython] O_element050  label="O_element : 025"  # scripted group (container) (typed FeaturePython)
  n = 5
  ref = O_element
FEATURE [App::DocumentObjectGroupPython] G4_KAPTON  # scripted group (container) (typed FeaturePython)
  Dunit = g/cm3
  Dvalue = 1.42
  Group = -> [C_element054,H_element048,N_element021,O_element050]
  conduct = 2
  density = 1
  expand = 3
  formula = G4_KAPTON
  name = G4_KAPTON
  specific = 4
FEATURE [App::DocumentObjectGroupPython] La_element001  label="La_element : 1"  # scripted group (container) (typed FeaturePython)
  n = 1
  ref = La_element
FEATURE [App::DocumentObjectGroupPython] Br_element003  label="Br_element : 002"  # scripted group (container) (typed FeaturePython)
  n = 1
  ref = Br_element
FEATURE [App::DocumentObjectGroupPython] O_element051  label="O_element : 026"  # scripted group (container) (typed FeaturePython)
  n = 1
  ref = O_element
FEATURE [App::DocumentObjectGroupPython] G4_LANTHANUM_OXYBROMIDE  # scripted group (container) (typed FeaturePython)
  Dunit = g/cm3
  Dvalue = 6.28
  Group = -> [La_element001,Br_element003,O_element051]
  conduct = 2
  density = 1
  expand = 3
  formula = G4_LANTHANUM_OXYBROMIDE
  name = G4_LANTHANUM_OXYBROMIDE
  specific = 4
FEATURE [App::DocumentObjectGroupPython] La_element002  label="La_element : 2"  # scripted group (container) (typed FeaturePython)
  n = 2
  ref = La_element
FEATURE [App::DocumentObjectGroupPython] O_element052  label="O_element : 027"  # scripted group (container) (typed FeaturePython)
  n = 2
  ref = O_element
FEATURE [App::DocumentObjectGroupPython] S_element015  label="S_element : 006"  # scripted group (container) (typed FeaturePython)
  n = 1
  ref = S_element
FEATURE [App::DocumentObjectGroupPython] G4_LANTHANUM_OXYSULFIDE  # scripted group (container) (typed FeaturePython)
  Dunit = g/cm3
  Dvalue = 5.86
  Group = -> [La_element002,O_element052,S_element015]
  conduct = 2
  density = 1
  expand = 3
  formula = G4_LANTHANUM_OXYSULFIDE
  name = G4_LANTHANUM_OXYSULFIDE
  specific = 4
FEATURE [App::DocumentObjectGroupPython] O_element053  label="O_element : 0.072"  # scripted group (container) (typed FeaturePython)
  n = 0.071682
FEATURE [App::DocumentObjectGroupPython] Pb_element002  label="Pb_element : 0.928"  # scripted group (container) (typed FeaturePython)
  n = 0.928318
FEATURE [App::DocumentObjectGroupPython] G4_LEAD_OXIDE  # scripted group (container) (typed FeaturePython)
  Dunit = g/cm3
  Dvalue = 9.53
  Group = -> [O_element053,Pb_element002]
  conduct = 2
  density = 1
  expand = 3
  formula = G4_LEAD_OXIDE
  name = G4_LEAD_OXIDE
  specific = 4
FEATURE [App::DocumentObjectGroupPython] Li_element001  label="Li_element : 1"  # scripted group (container) (typed FeaturePython)
  n = 1
  ref = Li_element
FEATURE [App::DocumentObjectGroupPython] N_element022  label="N_element : 011"  # scripted group (container) (typed FeaturePython)
  n = 1
  ref = N_element
FEATURE [App::DocumentObjectGroupPython] H_element049  label="H_element : 026"  # scripted group (container) (typed FeaturePython)
  n = 2
  ref = H_element
FEATURE [App::DocumentObjectGroupPython] G4_LITHIUM_AMIDE  # scripted group (container) (typed FeaturePython)
  Dunit = g/cm3
  Dvalue = 1.178
  Group = -> [Li_element001,N_element022,H_element049]
  conduct = 2
  density = 1
  expand = 3
  formula = G4_LITHIUM_AMIDE
  name = G4_LITHIUM_AMIDE
  specific = 4
FEATURE [App::DocumentObjectGroupPython] Li_element002  label="Li_element : 2"  # scripted group (container) (typed FeaturePython)
  n = 2
  ref = Li_element
FEATURE [App::DocumentObjectGroupPython] C_element055  label="C_element : 030"  # scripted group (container) (typed FeaturePython)
  n = 1
  ref = C_element
FEATURE [App::DocumentObjectGroupPython] O_element054  label="O_element : 028"  # scripted group (container) (typed FeaturePython)
  n = 3
  ref = O_element
FEATURE [App::DocumentObjectGroupPython] G4_LITHIUM_CARBONATE  # scripted group (container) (typed FeaturePython)
  Dunit = g/cm3
  Dvalue = 2.11
  Group = -> [Li_element002,C_element055,O_element054]
  conduct = 2
  density = 1
  expand = 3
  formula = G4_LITHIUM_CARBONATE
  name = G4_LITHIUM_CARBONATE
  specific = 4
FEATURE [App::DocumentObjectGroupPython] Li_element003  label="Li_element : 003"  # scripted group (container) (typed FeaturePython)
  n = 1
  ref = Li_element
FEATURE [App::DocumentObjectGroupPython] F_element012  label="F_element : 004"  # scripted group (container) (typed FeaturePython)
  n = 1
  ref = F_element
FEATURE [App::DocumentObjectGroupPython] G4_LITHIUM_FLUORIDE  # scripted group (container) (typed FeaturePython)
  Dunit = g/cm3
  Dvalue = 2.635
  Group = -> [Li_element003,F_element012]
  conduct = 2
  density = 1
  expand = 3
  formula = G4_LITHIUM_FLUORIDE
  name = G4_LITHIUM_FLUORIDE
  specific = 4
FEATURE [App::DocumentObjectGroupPython] Li_element004  label="Li_element : 004"  # scripted group (container) (typed FeaturePython)
  n = 1
  ref = Li_element
FEATURE [App::DocumentObjectGroupPython] H_element050  label="H_element : 027"  # scripted group (container) (typed FeaturePython)
  n = 1
  ref = H_element
FEATURE [App::DocumentObjectGroupPython] G4_LITHIUM_HYDRIDE  # scripted group (container) (typed FeaturePython)
  Dunit = g/cm3
  Dvalue = 0.82
  Group = -> [Li_element004,H_element050]
  conduct = 2
  density = 1
  expand = 3
  formula = G4_LITHIUM_HYDRIDE
  name = G4_LITHIUM_HYDRIDE
  specific = 4
FEATURE [App::DocumentObjectGroupPython] Li_element005  label="Li_element : 005"  # scripted group (container) (typed FeaturePython)
  n = 1
  ref = Li_element
FEATURE [App::DocumentObjectGroupPython] I_element003  label="I_element : 002"  # scripted group (container) (typed FeaturePython)
  n = 1
  ref = I_element
FEATURE [App::DocumentObjectGroupPython] G4_LITHIUM_IODIDE  # scripted group (container) (typed FeaturePython)
  Dunit = g/cm3
  Dvalue = 3.494
  Group = -> [Li_element005,I_element003]
  conduct = 2
  density = 1
  expand = 3
  formula = G4_LITHIUM_IODIDE
  name = G4_LITHIUM_IODIDE
  specific = 4
FEATURE [App::DocumentObjectGroupPython] Li_element006  label="Li_element : 006"  # scripted group (container) (typed FeaturePython)
  n = 2
  ref = Li_element
FEATURE [App::DocumentObjectGroupPython] O_element055  label="O_element : 029"  # scripted group (container) (typed FeaturePython)
  n = 1
  ref = O_element
FEATURE [App::DocumentObjectGroupPython] G4_LITHIUM_OXIDE  # scripted group (container) (typed FeaturePython)
  Dunit = g/cm3
  Dvalue = 2.013
  Group = -> [Li_element006,O_element055]
  conduct = 2
  density = 1
  expand = 3
  formula = G4_LITHIUM_OXIDE
  name = G4_LITHIUM_OXIDE
  specific = 4
FEATURE [App::DocumentObjectGroupPython] Li_element007  label="Li_element : 007"  # scripted group (container) (typed FeaturePython)
  n = 2
  ref = Li_element
FEATURE [App::DocumentObjectGroupPython] B_element005  label="B_element : 005"  # scripted group (container) (typed FeaturePython)
  n = 4
  ref = B_element
FEATURE [App::DocumentObjectGroupPython] O_element056  label="O_element : 7"  # scripted group (container) (typed FeaturePython)
  n = 7
  ref = O_element
FEATURE [App::DocumentObjectGroupPython] G4_LITHIUM_TETRABORATE  # scripted group (container) (typed FeaturePython)
  Dunit = g/cm3
  Dvalue = 2.44
  Group = -> [Li_element007,B_element005,O_element056]
  conduct = 2
  density = 1
  expand = 3
  formula = G4_LITHIUM_TETRABORATE
  name = G4_LITHIUM_TETRABORATE
  specific = 4
FEATURE [App::DocumentObjectGroupPython] H_element051  label="H_element : 0.105"  # scripted group (container) (typed FeaturePython)
  n = 0.105
FEATURE [App::DocumentObjectGroupPython] C_element056  label="C_element : 0.083"  # scripted group (container) (typed FeaturePython)
  n = 0.083
FEATURE [App::DocumentObjectGroupPython] N_element023  label="N_element : 0.023"  # scripted group (container) (typed FeaturePython)
  n = 0.023
FEATURE [App::DocumentObjectGroupPython] O_element057  label="O_element : 0.779"  # scripted group (container) (typed FeaturePython)
  n = 0.779
FEATURE [App::DocumentObjectGroupPython] Na_element010  label="Na_element : 0.097"  # scripted group (container) (typed FeaturePython)
  n = 0.002
FEATURE [App::DocumentObjectGroupPython] P_element006  label="P_element : 0.105"  # scripted group (container) (typed FeaturePython)
  n = 0.001
FEATURE [App::DocumentObjectGroupPython] S_element016  label="S_element : 0.017"  # scripted group (container) (typed FeaturePython)
  n = 0.002
FEATURE [App::DocumentObjectGroupPython] Cl_element014  label="Cl_element : 0.587"  # scripted group (container) (typed FeaturePython)
  n = 0.003
FEATURE [App::DocumentObjectGroupPython] K_element005  label="K_element : 0.015"  # scripted group (container) (typed FeaturePython)
  n = 0.002
FEATURE [App::DocumentObjectGroupPython] G4_LUNG_ICRP  # scripted group (container) (typed FeaturePython)
  Dunit = g/cm3
  Dvalue = 1.04
  Group = -> [H_element051,C_element056,N_element023,O_element057,Na_element010,P_element006,S_element016,Cl_element014,K_element005]
  conduct = 2
  density = 1
  expand = 3
  formula = G4_LUNG_ICRP
  name = G4_LUNG_ICRP
  specific = 4
FEATURE [App::DocumentObjectGroupPython] H_element052  label="H_element : 0.116"  # scripted group (container) (typed FeaturePython)
  n = 0.114318
FEATURE [App::DocumentObjectGroupPython] C_element057  label="C_element : 0.656"  # scripted group (container) (typed FeaturePython)
  n = 0.655824
FEATURE [App::DocumentObjectGroupPython] O_element058  label="O_element : 0.092"  # scripted group (container) (typed FeaturePython)
  n = 0.0921831
FEATURE [App::DocumentObjectGroupPython] Mg_element004  label="Mg_element : 0.135"  # scripted group (container) (typed FeaturePython)
  n = 0.134792
FEATURE [App::DocumentObjectGroupPython] Ca_element013  label="Ca_element : 0.003"  # scripted group (container) (typed FeaturePython)
  n = 0.002883
FEATURE [App::DocumentObjectGroupPython] G4_M3_WAX  # scripted group (container) (typed FeaturePython)
  Dunit = g/cm3
  Dvalue = 1.05
  Group = -> [H_element052,C_element057,O_element058,Mg_element004,Ca_element013]
  conduct = 2
  density = 1
  expand = 3
  formula = G4_M3_WAX
  name = G4_M3_WAX
  specific = 4
FEATURE [App::DocumentObjectGroupPython] Mg_element005  label="Mg_element : 1"  # scripted group (container) (typed FeaturePython)
  n = 1
  ref = Mg_element
FEATURE [App::DocumentObjectGroupPython] C_element058  label="C_element : 031"  # scripted group (container) (typed FeaturePython)
  n = 1
  ref = C_element
FEATURE [App::DocumentObjectGroupPython] O_element059  label="O_element : 030"  # scripted group (container) (typed FeaturePython)
  n = 3
  ref = O_element
FEATURE [App::DocumentObjectGroupPython] G4_MAGNESIUM_CARBONATE  # scripted group (container) (typed FeaturePython)
  Dunit = g/cm3
  Dvalue = 2.958
  Group = -> [Mg_element005,C_element058,O_element059]
  conduct = 2
  density = 1
  expand = 3
  formula = G4_MAGNESIUM_CARBONATE
  name = G4_MAGNESIUM_CARBONATE
  specific = 4
FEATURE [App::DocumentObjectGroupPython] Mg_element006  label="Mg_element : 002"  # scripted group (container) (typed FeaturePython)
  n = 1
  ref = Mg_element
FEATURE [App::DocumentObjectGroupPython] F_element013  label="F_element : 005"  # scripted group (container) (typed FeaturePython)
  n = 2
  ref = F_element
FEATURE [App::DocumentObjectGroupPython] G4_MAGNESIUM_FLUORIDE  # scripted group (container) (typed FeaturePython)
  Dunit = g/cm3
  Dvalue = 3
  Group = -> [Mg_element006,F_element013]
  conduct = 2
  density = 1
  expand = 3
  formula = G4_MAGNESIUM_FLUORIDE
  name = G4_MAGNESIUM_FLUORIDE
  specific = 4
FEATURE [App::DocumentObjectGroupPython] Mg_element007  label="Mg_element : 003"  # scripted group (container) (typed FeaturePython)
  n = 1
  ref = Mg_element
FEATURE [App::DocumentObjectGroupPython] O_element060  label="O_element : 031"  # scripted group (container) (typed FeaturePython)
  n = 1
  ref = O_element
FEATURE [App::DocumentObjectGroupPython] G4_MAGNESIUM_OXIDE  # scripted group (container) (typed FeaturePython)
  Dunit = g/cm3
  Dvalue = 3.58
  Group = -> [Mg_element007,O_element060]
  conduct = 2
  density = 1
  expand = 3
  formula = G4_MAGNESIUM_OXIDE
  name = G4_MAGNESIUM_OXIDE
  specific = 4
FEATURE [App::DocumentObjectGroupPython] Mg_element008  label="Mg_element : 004"  # scripted group (container) (typed FeaturePython)
  n = 1
  ref = Mg_element
FEATURE [App::DocumentObjectGroupPython] B_element006  label="B_element : 006"  # scripted group (container) (typed FeaturePython)
  n = 4
  ref = B_element
FEATURE [App::DocumentObjectGroupPython] O_element061  label="O_element : 032"  # scripted group (container) (typed FeaturePython)
  n = 7
  ref = O_element
FEATURE [App::DocumentObjectGroupPython] G4_MAGNESIUM_TETRABORATE  # scripted group (container) (typed FeaturePython)
  Dunit = g/cm3
  Dvalue = 2.53
  Group = -> [Mg_element008,B_element006,O_element061]
  conduct = 2
  density = 1
  expand = 3
  formula = G4_MAGNESIUM_TETRABORATE
  name = G4_MAGNESIUM_TETRABORATE
  specific = 4
FEATURE [App::DocumentObjectGroupPython] Hg_element001  label="Hg_element : 1"  # scripted group (container) (typed FeaturePython)
  n = 1
  ref = Hg_element
FEATURE [App::DocumentObjectGroupPython] I_element004  label="I_element : 2"  # scripted group (container) (typed FeaturePython)
  n = 2
  ref = I_element
FEATURE [App::DocumentObjectGroupPython] G4_MERCURIC_IODIDE  # scripted group (container) (typed FeaturePython)
  Dunit = g/cm3
  Dvalue = 6.36
  Group = -> [Hg_element001,I_element004]
  conduct = 2
  density = 1
  expand = 3
  formula = G4_MERCURIC_IODIDE
  name = G4_MERCURIC_IODIDE
  specific = 4
FEATURE [App::DocumentObjectGroupPython] C_element059  label="C_element : 032"  # scripted group (container) (typed FeaturePython)
  n = 1
  ref = C_element
FEATURE [App::DocumentObjectGroupPython] H_element053  label="H_element : 028"  # scripted group (container) (typed FeaturePython)
  n = 4
  ref = H_element
FEATURE [App::DocumentObjectGroupPython] G4_METHANE  # scripted group (container) (typed FeaturePython)
  Dunit = g/cm3
  Dvalue = 0.000667151
  Group = -> [C_element059,H_element053]
  conduct = 2
  density = 1
  expand = 3
  formula = G4_METHANE
  name = G4_METHANE
  specific = 4
FEATURE [App::DocumentObjectGroupPython] C_element060  label="C_element : 033"  # scripted group (container) (typed FeaturePython)
  n = 1
  ref = C_element
FEATURE [App::DocumentObjectGroupPython] H_element054  label="H_element : 029"  # scripted group (container) (typed FeaturePython)
  n = 4
  ref = H_element
FEATURE [App::DocumentObjectGroupPython] O_element062  label="O_element : 033"  # scripted group (container) (typed FeaturePython)
  n = 1
  ref = O_element
FEATURE [App::DocumentObjectGroupPython] G4_METHANOL  # scripted group (container) (typed FeaturePython)
  Dunit = g/cm3
  Dvalue = 0.7914
  Group = -> [C_element060,H_element054,O_element062]
  conduct = 2
  density = 1
  expand = 3
  formula = G4_METHANOL
  name = G4_METHANOL
  specific = 4
FEATURE [App::DocumentObjectGroupPython] H_element055  label="H_element : 0.134"  # scripted group (container) (typed FeaturePython)
  n = 0.13404
FEATURE [App::DocumentObjectGroupPython] C_element061  label="C_element : 0.778"  # scripted group (container) (typed FeaturePython)
  n = 0.77796
FEATURE [App::DocumentObjectGroupPython] O_element063  label="O_element : 0.035"  # scripted group (container) (typed FeaturePython)
  n = 0.03502
FEATURE [App::DocumentObjectGroupPython] Mg_element009  label="Mg_element : 0.039"  # scripted group (container) (typed FeaturePython)
  n = 0.038594
FEATURE [App::DocumentObjectGroupPython] Ti_element002  label="Ti_element : 0.014"  # scripted group (container) (typed FeaturePython)
  n = 0.014386
FEATURE [App::DocumentObjectGroupPython] G4_MIX_D_WAX  # scripted group (container) (typed FeaturePython)
  Dunit = g/cm3
  Dvalue = 0.99
  Group = -> [H_element055,C_element061,O_element063,Mg_element009,Ti_element002]
  conduct = 2
  density = 1
  expand = 3
  formula = G4_MIX_D_WAX
  name = G4_MIX_D_WAX
  specific = 4
FEATURE [App::DocumentObjectGroupPython] H_element056  label="H_element : 0.135"  # scripted group (container) (typed FeaturePython)
  n = 0.081192
FEATURE [App::DocumentObjectGroupPython] C_element062  label="C_element : 0.583"  # scripted group (container) (typed FeaturePython)
  n = 0.583442
FEATURE [App::DocumentObjectGroupPython] N_element024  label="N_element : 0.018"  # scripted group (container) (typed FeaturePython)
  n = 0.017798
FEATURE [App::DocumentObjectGroupPython] O_element064  label="O_element : 0.186"  # scripted group (container) (typed FeaturePython)
  n = 0.186381
FEATURE [App::DocumentObjectGroupPython] Mg_element010  label="Mg_element : 0.130"  # scripted group (container) (typed FeaturePython)
  n = 0.130287
FEATURE [App::DocumentObjectGroupPython] Cl_element015  label="Cl_element : 0.588"  # scripted group (container) (typed FeaturePython)
  n = 0.0009
FEATURE [App::DocumentObjectGroupPython] G4_MS20_TISSUE  # scripted group (container) (typed FeaturePython)
  Dunit = g/cm3
  Dvalue = 1
  Group = -> [H_element056,C_element062,N_element024,O_element064,Mg_element010,Cl_element015]
  conduct = 2
  density = 1
  expand = 3
  formula = G4_MS20_TISSUE
  name = G4_MS20_TISSUE
  specific = 4
FEATURE [App::DocumentObjectGroupPython] H_element057  label="H_element : 0.136"  # scripted group (container) (typed FeaturePython)
  n = 0.102
FEATURE [App::DocumentObjectGroupPython] C_element063  label="C_element : 0.143"  # scripted group (container) (typed FeaturePython)
  n = 0.143
FEATURE [App::DocumentObjectGroupPython] N_element025  label="N_element : 0.034"  # scripted group (container) (typed FeaturePython)
  n = 0.034
FEATURE [App::DocumentObjectGroupPython] O_element065  label="O_element : 0.710"  # scripted group (container) (typed FeaturePython)
  n = 0.71
FEATURE [App::DocumentObjectGroupPython] Na_element011  label="Na_element : 0.098"  # scripted group (container) (typed FeaturePython)
  n = 0.001
FEATURE [App::DocumentObjectGroupPython] P_element007  label="P_element : 0.002"  # scripted group (container) (typed FeaturePython)
  n = 0.002
FEATURE [App::DocumentObjectGroupPython] S_element017  label="S_element : 0.018"  # scripted group (container) (typed FeaturePython)
  n = 0.003
FEATURE [App::DocumentObjectGroupPython] Cl_element016  label="Cl_element : 0.589"  # scripted group (container) (typed FeaturePython)
  n = 0.001
FEATURE [App::DocumentObjectGroupPython] K_element006  label="K_element : 0.004"  # scripted group (container) (typed FeaturePython)
  n = 0.004
FEATURE [App::DocumentObjectGroupPython] G4_MUSCLE_SKELETAL_ICRP  # scripted group (container) (typed FeaturePython)
  Dunit = g/cm3
  Dvalue = 1.05
  Group = -> [H_element057,C_element063,N_element025,O_element065,Na_element011,P_element007,S_element017,Cl_element016,K_element006]
  conduct = 2
  density = 1
  expand = 3
  formula = G4_MUSCLE_SKELETAL_ICRP
  name = G4_MUSCLE_SKELETAL_ICRP
  specific = 4
FEATURE [App::DocumentObjectGroupPython] H_element058  label="H_element : 0.137"  # scripted group (container) (typed FeaturePython)
  n = 0.102102
FEATURE [App::DocumentObjectGroupPython] C_element064  label="C_element : 0.123"  # scripted group (container) (typed FeaturePython)
  n = 0.123123
FEATURE [App::DocumentObjectGroupPython] N_element026  label="N_element : 0.756"  # scripted group (container) (typed FeaturePython)
  n = 0.035035
FEATURE [App::DocumentObjectGroupPython] O_element066  label="O_element : 0.730"  # scripted group (container) (typed FeaturePython)
  n = 0.72973
FEATURE [App::DocumentObjectGroupPython] Na_element012  label="Na_element : 0.099"  # scripted group (container) (typed FeaturePython)
  n = 0.001001
FEATURE [App::DocumentObjectGroupPython] P_element008  label="P_element : 0.106"  # scripted group (container) (typed FeaturePython)
  n = 0.002002
FEATURE [App::DocumentObjectGroupPython] S_element018  label="S_element : 0.019"  # scripted group (container) (typed FeaturePython)
  n = 0.004004
FEATURE [App::DocumentObjectGroupPython] K_element007  label="K_element : 0.016"  # scripted group (container) (typed FeaturePython)
  n = 0.003003
FEATURE [App::DocumentObjectGroupPython] G4_MUSCLE_STRIATED_ICRU  # scripted group (container) (typed FeaturePython)
  Dunit = g/cm3
  Dvalue = 1.04
  Group = -> [H_element058,C_element064,N_element026,O_element066,Na_element012,P_element008,S_element018,K_element007]
  conduct = 2
  density = 1
  expand = 3
  formula = G4_MUSCLE_STRIATED_ICRU
  name = G4_MUSCLE_STRIATED_ICRU
  specific = 4
FEATURE [App::DocumentObjectGroupPython] H_element059  label="H_element : 0.098"  # scripted group (container) (typed FeaturePython)
  n = 0.0982341
FEATURE [App::DocumentObjectGroupPython] C_element065  label="C_element : 0.156"  # scripted group (container) (typed FeaturePython)
  n = 0.156214
FEATURE [App::DocumentObjectGroupPython] N_element027  label="N_element : 0.757"  # scripted group (container) (typed FeaturePython)
  n = 0.035451
FEATURE [App::DocumentObjectGroupPython] O_element067  label="O_element : 0.880"  # scripted group (container) (typed FeaturePython)
  n = 0.710101
FEATURE [App::DocumentObjectGroupPython] G4_MUSCLE_WITH_SUCROSE  # scripted group (container) (typed FeaturePython)
  Dunit = g/cm3
  Dvalue = 1.11
  Group = -> [H_element059,C_element065,N_element027,O_element067]
  conduct = 2
  density = 1
  expand = 3
  formula = G4_MUSCLE_WITH_SUCROSE
  name = G4_MUSCLE_WITH_SUCROSE
  specific = 4
FEATURE [App::DocumentObjectGroupPython] H_element060  label="H_element : 0.138"  # scripted group (container) (typed FeaturePython)
  n = 0.101969
FEATURE [App::DocumentObjectGroupPython] C_element066  label="C_element : 0.120"  # scripted group (container) (typed FeaturePython)
  n = 0.120058
FEATURE [App::DocumentObjectGroupPython] N_element028  label="N_element : 0.758"  # scripted group (container) (typed FeaturePython)
  n = 0.035451
FEATURE [App::DocumentObjectGroupPython] O_element068  label="O_element : 0.743"  # scripted group (container) (typed FeaturePython)
  n = 0.742522
FEATURE [App::DocumentObjectGroupPython] G4_MUSCLE_WITHOUT_SUCROSE  # scripted group (container) (typed FeaturePython)
  Dunit = g/cm3
  Dvalue = 1.07
  Group = -> [H_element060,C_element066,N_element028,O_element068]
  conduct = 2
  density = 1
  expand = 3
  formula = G4_MUSCLE_WITHOUT_SUCROSE
  name = G4_MUSCLE_WITHOUT_SUCROSE
  specific = 4
FEATURE [App::DocumentObjectGroupPython] C_element067  label="C_element : 10"  # scripted group (container) (typed FeaturePython)
  n = 10
  ref = C_element
FEATURE [App::DocumentObjectGroupPython] H_element061  label="H_element : 030"  # scripted group (container) (typed FeaturePython)
  n = 8
  ref = H_element
FEATURE [App::DocumentObjectGroupPython] G4_NAPHTHALENE  # scripted group (container) (typed FeaturePython)
  Dunit = g/cm3
  Dvalue = 1.145
  Group = -> [C_element067,H_element061]
  conduct = 2
  density = 1
  expand = 3
  formula = G4_NAPHTHALENE
  name = G4_NAPHTHALENE
  specific = 4
FEATURE [App::DocumentObjectGroupPython] C_element068  label="C_element : 034"  # scripted group (container) (typed FeaturePython)
  n = 6
  ref = C_element
FEATURE [App::DocumentObjectGroupPython] H_element062  label="H_element : 031"  # scripted group (container) (typed FeaturePython)
  n = 5
  ref = H_element
FEATURE [App::DocumentObjectGroupPython] N_element029  label="N_element : 012"  # scripted group (container) (typed FeaturePython)
  n = 1
  ref = N_element
FEATURE [App::DocumentObjectGroupPython] O_element069  label="O_element : 034"  # scripted group (container) (typed FeaturePython)
  n = 2
  ref = O_element
FEATURE [App::DocumentObjectGroupPython] G4_NITROBENZENE  # scripted group (container) (typed FeaturePython)
  Dunit = g/cm3
  Dvalue = 1.19867
  Group = -> [C_element068,H_element062,N_element029,O_element069]
  conduct = 2
  density = 1
  expand = 3
  formula = G4_NITROBENZENE
  name = G4_NITROBENZENE
  specific = 4
FEATURE [App::DocumentObjectGroupPython] N_element030  label="N_element : 013"  # scripted group (container) (typed FeaturePython)
  n = 2
  ref = N_element
FEATURE [App::DocumentObjectGroupPython] O_element070  label="O_element : 035"  # scripted group (container) (typed FeaturePython)
  n = 1
  ref = O_element
FEATURE [App::DocumentObjectGroupPython] G4_NITROUS_OXIDE  # scripted group (container) (typed FeaturePython)
  Dunit = g/cm3
  Dvalue = 0.00183094
  Group = -> [N_element030,O_element070]
  conduct = 2
  density = 1
  expand = 3
  formula = G4_NITROUS_OXIDE
  name = G4_NITROUS_OXIDE
  specific = 4
FEATURE [App::DocumentObjectGroupPython] H_element063  label="H_element : 0.104"  # scripted group (container) (typed FeaturePython)
  n = 0.103509
FEATURE [App::DocumentObjectGroupPython] C_element069  label="C_element : 0.648"  # scripted group (container) (typed FeaturePython)
  n = 0.648416
FEATURE [App::DocumentObjectGroupPython] N_element031  label="N_element : 0.100"  # scripted group (container) (typed FeaturePython)
  n = 0.0995361
FEATURE [App::DocumentObjectGroupPython] O_element071  label="O_element : 0.149"  # scripted group (container) (typed FeaturePython)
  n = 0.148539
FEATURE [App::DocumentObjectGroupPython] G4_NYLON_8062  label="G4_NYLON-8062"  # scripted group (container) (typed FeaturePython)
  Dunit = g/cm3
  Dvalue = 1.08
  Group = -> [H_element063,C_element069,N_element031,O_element071]
  conduct = 2
  density = 1
  expand = 3
  formula = G4_NYLON-8062
  name = G4_NYLON-8062
  specific = 4
FEATURE [App::DocumentObjectGroupPython] C_element070  label="C_element : 035"  # scripted group (container) (typed FeaturePython)
  n = 6
  ref = C_element
FEATURE [App::DocumentObjectGroupPython] H_element064  label="H_element : 11"  # scripted group (container) (typed FeaturePython)
  n = 11
  ref = H_element
FEATURE [App::DocumentObjectGroupPython] N_element032  label="N_element : 014"  # scripted group (container) (typed FeaturePython)
  n = 1
  ref = N_element
FEATURE [App::DocumentObjectGroupPython] O_element072  label="O_element : 036"  # scripted group (container) (typed FeaturePython)
  n = 1
  ref = O_element
FEATURE [App::DocumentObjectGroupPython] G4_NYLON_6_6  label="G4_NYLON-6-6"  # scripted group (container) (typed FeaturePython)
  Dunit = g/cm3
  Dvalue = 1.14
  Group = -> [C_element070,H_element064,N_element032,O_element072]
  conduct = 2
  density = 1
  expand = 3
  formula = G4_NYLON-6-6
  name = G4_NYLON-6-6
  specific = 4
FEATURE [App::DocumentObjectGroupPython] H_element065  label="H_element : 0.139"  # scripted group (container) (typed FeaturePython)
  n = 0.107062
FEATURE [App::DocumentObjectGroupPython] C_element071  label="C_element : 0.680"  # scripted group (container) (typed FeaturePython)
  n = 0.680449
FEATURE [App::DocumentObjectGroupPython] N_element033  label="N_element : 0.099"  # scripted group (container) (typed FeaturePython)
  n = 0.099189
FEATURE [App::DocumentObjectGroupPython] O_element073  label="O_element : 0.113"  # scripted group (container) (typed FeaturePython)
  n = 0.1133
FEATURE [App::DocumentObjectGroupPython] G4_NYLON_6_10  label="G4_NYLON-6-10"  # scripted group (container) (typed FeaturePython)
  Dunit = g/cm3
  Dvalue = 1.14
  Group = -> [H_element065,C_element071,N_element033,O_element073]
  conduct = 2
  density = 1
  expand = 3
  formula = G4_NYLON-6-10
  name = G4_NYLON-6-10
  specific = 4
FEATURE [App::DocumentObjectGroupPython] H_element066  label="H_element : 0.140"  # scripted group (container) (typed FeaturePython)
  n = 0.115476
FEATURE [App::DocumentObjectGroupPython] C_element072  label="C_element : 0.721"  # scripted group (container) (typed FeaturePython)
  n = 0.720818
FEATURE [App::DocumentObjectGroupPython] N_element034  label="N_element : 0.076"  # scripted group (container) (typed FeaturePython)
  n = 0.0764169
FEATURE [App::DocumentObjectGroupPython] O_element074  label="O_element : 0.087"  # scripted group (container) (typed FeaturePython)
  n = 0.0872889
FEATURE [App::DocumentObjectGroupPython] G4_NYLON_11_RILSAN  label="G4_NYLON-11_RILSAN"  # scripted group (container) (typed FeaturePython)
  Dunit = g/cm3
  Dvalue = 1.425
  Group = -> [H_element066,C_element072,N_element034,O_element074]
  conduct = 2
  density = 1
  expand = 3
  formula = G4_NYLON-11_RILSAN
  name = G4_NYLON-11_RILSAN
  specific = 4
FEATURE [App::DocumentObjectGroupPython] C_element073  label="C_element : 8"  # scripted group (container) (typed FeaturePython)
  n = 8
  ref = C_element
FEATURE [App::DocumentObjectGroupPython] H_element067  label="H_element : 18"  # scripted group (container) (typed FeaturePython)
  n = 18
  ref = H_element
FEATURE [App::DocumentObjectGroupPython] G4_OCTANE  # scripted group (container) (typed FeaturePython)
  Dunit = g/cm3
  Dvalue = 0.7026
  Group = -> [C_element073,H_element067]
  conduct = 2
  density = 1
  expand = 3
  formula = G4_OCTANE
  name = G4_OCTANE
  specific = 4
FEATURE [App::DocumentObjectGroupPython] C_element074  label="C_element : 25"  # scripted group (container) (typed FeaturePython)
  n = 25
  ref = C_element
FEATURE [App::DocumentObjectGroupPython] H_element068  label="H_element : 52"  # scripted group (container) (typed FeaturePython)
  n = 52
  ref = H_element
FEATURE [App::DocumentObjectGroupPython] G4_PARAFFIN  # scripted group (container) (typed FeaturePython)
  Dunit = g/cm3
  Dvalue = 0.93
  Group = -> [C_element074,H_element068]
  conduct = 2
  density = 1
  expand = 3
  formula = G4_PARAFFIN
  name = G4_PARAFFIN
  specific = 4
FEATURE [App::DocumentObjectGroupPython] C_element075  label="C_element : 036"  # scripted group (container) (typed FeaturePython)
  n = 5
  ref = C_element
FEATURE [App::DocumentObjectGroupPython] H_element069  label="H_element : 032"  # scripted group (container) (typed FeaturePython)
  n = 12
  ref = H_element
FEATURE [App::DocumentObjectGroupPython] G4_N_PENTANE  label="G4_N-PENTANE"  # scripted group (container) (typed FeaturePython)
  Dunit = g/cm3
  Dvalue = 0.6262
  Group = -> [C_element075,H_element069]
  conduct = 2
  density = 1
  expand = 3
  formula = G4_N-PENTANE
  name = G4_N-PENTANE
  specific = 4
FEATURE [App::DocumentObjectGroupPython] H_element070  label="H_element : 0.014"  # scripted group (container) (typed FeaturePython)
  n = 0.0141
FEATURE [App::DocumentObjectGroupPython] C_element076  label="C_element : 0.072"  # scripted group (container) (typed FeaturePython)
  n = 0.072261
FEATURE [App::DocumentObjectGroupPython] N_element035  label="N_element : 0.019"  # scripted group (container) (typed FeaturePython)
  n = 0.01932
FEATURE [App::DocumentObjectGroupPython] O_element075  label="O_element : 0.066"  # scripted group (container) (typed FeaturePython)
  n = 0.066101
FEATURE [App::DocumentObjectGroupPython] S_element019  label="S_element : 0.020"  # scripted group (container) (typed FeaturePython)
  n = 0.00189
FEATURE [App::DocumentObjectGroupPython] Br_element004  label="Br_element : 0.349"  # scripted group (container) (typed FeaturePython)
  n = 0.349103
FEATURE [App::DocumentObjectGroupPython] Ag_element001  label="Ag_element : 0.474"  # scripted group (container) (typed FeaturePython)
  n = 0.474105
FEATURE [App::DocumentObjectGroupPython] I_element005  label="I_element : 0.003"  # scripted group (container) (typed FeaturePython)
  n = 0.00312
FEATURE [App::DocumentObjectGroupPython] G4_PHOTO_EMULSION  # scripted group (container) (typed FeaturePython)
  Dunit = g/cm3
  Dvalue = 3.815
  Group = -> [H_element070,C_element076,N_element035,O_element075,S_element019,Br_element004,Ag_element001,I_element005]
  conduct = 2
  density = 1
  expand = 3
  formula = G4_PHOTO_EMULSION
  name = G4_PHOTO_EMULSION
  specific = 4
FEATURE [App::DocumentObjectGroupPython] C_element077  label="C_element : 9"  # scripted group (container) (typed FeaturePython)
  n = 9
  ref = C_element
FEATURE [App::DocumentObjectGroupPython] H_element071  label="H_element : 033"  # scripted group (container) (typed FeaturePython)
  n = 10
  ref = H_element
FEATURE [App::DocumentObjectGroupPython] G4_PLASTIC_SC_VINYLTOLUENE  # scripted group (container) (typed FeaturePython)
  Dunit = g/cm3
  Dvalue = 1.032
  Group = -> [C_element077,H_element071]
  conduct = 2
  density = 1
  expand = 3
  formula = G4_PLASTIC_SC_VINYLTOLUENE
  name = G4_PLASTIC_SC_VINYLTOLUENE
  specific = 4
FEATURE [App::DocumentObjectGroupPython] Pu_element001  label="Pu_element : 1"  # scripted group (container) (typed FeaturePython)
  n = 1
  ref = Pu_element
FEATURE [App::DocumentObjectGroupPython] O_element076  label="O_element : 037"  # scripted group (container) (typed FeaturePython)
  n = 2
  ref = O_element
FEATURE [App::DocumentObjectGroupPython] G4_PLUTONIUM_DIOXIDE  # scripted group (container) (typed FeaturePython)
  Dunit = g/cm3
  Dvalue = 11.46
  Group = -> [Pu_element001,O_element076]
  conduct = 2
  density = 1
  expand = 3
  formula = G4_PLUTONIUM_DIOXIDE
  name = G4_PLUTONIUM_DIOXIDE
  specific = 4
FEATURE [App::DocumentObjectGroupPython] C_element078  label="C_element : 037"  # scripted group (container) (typed FeaturePython)
  n = 3
  ref = C_element
FEATURE [App::DocumentObjectGroupPython] H_element072  label="H_element : 034"  # scripted group (container) (typed FeaturePython)
  n = 3
  ref = H_element
FEATURE [App::DocumentObjectGroupPython] N_element036  label="N_element : 015"  # scripted group (container) (typed FeaturePython)
  n = 1
  ref = N_element
FEATURE [App::DocumentObjectGroupPython] G4_POLYACRYLONITRILE  # scripted group (container) (typed FeaturePython)
  Dunit = g/cm3
  Dvalue = 1.17
  Group = -> [C_element078,H_element072,N_element036]
  conduct = 2
  density = 1
  expand = 3
  formula = G4_POLYACRYLONITRILE
  name = G4_POLYACRYLONITRILE
  specific = 4
FEATURE [App::DocumentObjectGroupPython] C_element079  label="C_element : 16"  # scripted group (container) (typed FeaturePython)
  n = 16
  ref = C_element
FEATURE [App::DocumentObjectGroupPython] H_element073  label="H_element : 035"  # scripted group (container) (typed FeaturePython)
  n = 14
  ref = H_element
FEATURE [App::DocumentObjectGroupPython] O_element077  label="O_element : 038"  # scripted group (container) (typed FeaturePython)
  n = 3
  ref = O_element
FEATURE [App::DocumentObjectGroupPython] G4_POLYCARBONATE  # scripted group (container) (typed FeaturePython)
  Dunit = g/cm3
  Dvalue = 1.2
  Group = -> [C_element079,H_element073,O_element077]
  conduct = 2
  density = 1
  expand = 3
  formula = G4_POLYCARBONATE
  name = G4_POLYCARBONATE
  specific = 4
FEATURE [App::DocumentObjectGroupPython] C_element080  label="C_element : 038"  # scripted group (container) (typed FeaturePython)
  n = 8
  ref = C_element
FEATURE [App::DocumentObjectGroupPython] H_element074  label="H_element : 036"  # scripted group (container) (typed FeaturePython)
  n = 7
  ref = H_element
FEATURE [App::DocumentObjectGroupPython] Cl_element017  label="Cl_element : 007"  # scripted group (container) (typed FeaturePython)
  n = 1
  ref = Cl_element
FEATURE [App::DocumentObjectGroupPython] G4_POLYCHLOROSTYRENE  # scripted group (container) (typed FeaturePython)
  Dunit = g/cm3
  Dvalue = 1.3
  Group = -> [C_element080,H_element074,Cl_element017]
  conduct = 2
  density = 1
  expand = 3
  formula = G4_POLYCHLOROSTYRENE
  name = G4_POLYCHLOROSTYRENE
  specific = 4
FEATURE [App::DocumentObjectGroupPython] C_element081  label="C_element : 039"  # scripted group (container) (typed FeaturePython)
  n = 1
  ref = C_element
FEATURE [App::DocumentObjectGroupPython] H_element075  label="H_element : 037"  # scripted group (container) (typed FeaturePython)
  n = 2
  ref = H_element
FEATURE [App::DocumentObjectGroupPython] G4_POLYETHYLENE  # scripted group (container) (typed FeaturePython)
  Dunit = g/cm3
  Dvalue = 0.94
  Group = -> [C_element081,H_element075]
  conduct = 2
  density = 1
  expand = 3
  formula = G4_POLYETHYLENE
  name = G4_POLYETHYLENE
  specific = 4
FEATURE [App::DocumentObjectGroupPython] C_element082  label="C_element : 040"  # scripted group (container) (typed FeaturePython)
  n = 10
  ref = C_element
FEATURE [App::DocumentObjectGroupPython] H_element076  label="H_element : 038"  # scripted group (container) (typed FeaturePython)
  n = 8
  ref = H_element
FEATURE [App::DocumentObjectGroupPython] O_element078  label="O_element : 039"  # scripted group (container) (typed FeaturePython)
  n = 4
  ref = O_element
FEATURE [App::DocumentObjectGroupPython] G4_MYLAR  # scripted group (container) (typed FeaturePython)
  Dunit = g/cm3
  Dvalue = 1.4
  Group = -> [C_element082,H_element076,O_element078]
  conduct = 2
  density = 1
  expand = 3
  formula = G4_MYLAR
  name = G4_MYLAR
  specific = 4
FEATURE [App::DocumentObjectGroupPython] C_element083  label="C_element : 041"  # scripted group (container) (typed FeaturePython)
  n = 5
  ref = C_element
FEATURE [App::DocumentObjectGroupPython] H_element077  label="H_element : 039"  # scripted group (container) (typed FeaturePython)
  n = 8
  ref = H_element
FEATURE [App::DocumentObjectGroupPython] O_element079  label="O_element : 040"  # scripted group (container) (typed FeaturePython)
  n = 2
  ref = O_element
FEATURE [App::DocumentObjectGroupPython] G4_PLEXIGLASS  # scripted group (container) (typed FeaturePython)
  Dunit = g/cm3
  Dvalue = 1.19
  Group = -> [C_element083,H_element077,O_element079]
  conduct = 2
  density = 1
  expand = 3
  formula = G4_PLEXIGLASS
  name = G4_PLEXIGLASS
  specific = 4
FEATURE [App::DocumentObjectGroupPython] C_element084  label="C_element : 042"  # scripted group (container) (typed FeaturePython)
  n = 1
  ref = C_element
FEATURE [App::DocumentObjectGroupPython] H_element078  label="H_element : 040"  # scripted group (container) (typed FeaturePython)
  n = 2
  ref = H_element
FEATURE [App::DocumentObjectGroupPython] O_element080  label="O_element : 041"  # scripted group (container) (typed FeaturePython)
  n = 1
  ref = O_element
FEATURE [App::DocumentObjectGroupPython] G4_POLYOXYMETHYLENE  # scripted group (container) (typed FeaturePython)
  Dunit = g/cm3
  Dvalue = 1.425
  Group = -> [C_element084,H_element078,O_element080]
  conduct = 2
  density = 1
  expand = 3
  formula = G4_POLYOXYMETHYLENE
  name = G4_POLYOXYMETHYLENE
  specific = 4
FEATURE [App::DocumentObjectGroupPython] C_element085  label="C_element : 043"  # scripted group (container) (typed FeaturePython)
  n = 2
  ref = C_element
FEATURE [App::DocumentObjectGroupPython] H_element079  label="H_element : 041"  # scripted group (container) (typed FeaturePython)
  n = 4
  ref = H_element
FEATURE [App::DocumentObjectGroupPython] G4_POLYPROPYLENE  # scripted group (container) (typed FeaturePython)
  Dunit = g/cm3
  Dvalue = 0.9
  Group = -> [C_element085,H_element079]
  conduct = 2
  density = 1
  expand = 3
  formula = G4_POLYPROPYLENE
  name = G4_POLYPROPYLENE
  specific = 4
FEATURE [App::DocumentObjectGroupPython] C_element086  label="C_element : 044"  # scripted group (container) (typed FeaturePython)
  n = 8
  ref = C_element
FEATURE [App::DocumentObjectGroupPython] H_element080  label="H_element : 042"  # scripted group (container) (typed FeaturePython)
  n = 8
  ref = H_element
FEATURE [App::DocumentObjectGroupPython] G4_POLYSTYRENE  # scripted group (container) (typed FeaturePython)
  Dunit = g/cm3
  Dvalue = 1.06
  Group = -> [C_element086,H_element080]
  conduct = 2
  density = 1
  expand = 3
  formula = G4_POLYSTYRENE
  name = G4_POLYSTYRENE
  specific = 4
FEATURE [App::DocumentObjectGroupPython] C_element087  label="C_element : 045"  # scripted group (container) (typed FeaturePython)
  n = 2
  ref = C_element
FEATURE [App::DocumentObjectGroupPython] F_element014  label="F_element : 4"  # scripted group (container) (typed FeaturePython)
  n = 4
  ref = F_element
FEATURE [App::DocumentObjectGroupPython] G4_TEFLON  # scripted group (container) (typed FeaturePython)
  Dunit = g/cm3
  Dvalue = 2.2
  Group = -> [C_element087,F_element014]
  conduct = 2
  density = 1
  expand = 3
  formula = G4_TEFLON
  name = G4_TEFLON
  specific = 4
FEATURE [App::DocumentObjectGroupPython] C_element088  label="C_element : 046"  # scripted group (container) (typed FeaturePython)
  n = 2
  ref = C_element
FEATURE [App::DocumentObjectGroupPython] F_element015  label="F_element : 006"  # scripted group (container) (typed FeaturePython)
  n = 3
  ref = F_element
FEATURE [App::DocumentObjectGroupPython] Cl_element018  label="Cl_element : 008"  # scripted group (container) (typed FeaturePython)
  n = 1
  ref = Cl_element
FEATURE [App::DocumentObjectGroupPython] G4_POLYTRIFLUOROCHLOROETHYLENE  # scripted group (container) (typed FeaturePython)
  Dunit = g/cm3
  Dvalue = 2.1
  Group = -> [C_element088,F_element015,Cl_element018]
  conduct = 2
  density = 1
  expand = 3
  formula = G4_POLYTRIFLUOROCHLOROETHYLENE
  name = G4_POLYTRIFLUOROCHLOROETHYLENE
  specific = 4
FEATURE [App::DocumentObjectGroupPython] C_element089  label="C_element : 047"  # scripted group (container) (typed FeaturePython)
  n = 4
  ref = C_element
FEATURE [App::DocumentObjectGroupPython] H_element081  label="H_element : 043"  # scripted group (container) (typed FeaturePython)
  n = 6
  ref = H_element
FEATURE [App::DocumentObjectGroupPython] O_element081  label="O_element : 042"  # scripted group (container) (typed FeaturePython)
  n = 2
  ref = O_element
FEATURE [App::DocumentObjectGroupPython] G4_POLYVINYL_ACETATE  # scripted group (container) (typed FeaturePython)
  Dunit = g/cm3
  Dvalue = 1.19
  Group = -> [C_element089,H_element081,O_element081]
  conduct = 2
  density = 1
  expand = 3
  formula = G4_POLYVINYL_ACETATE
  name = G4_POLYVINYL_ACETATE
  specific = 4
FEATURE [App::DocumentObjectGroupPython] C_element090  label="C_element : 048"  # scripted group (container) (typed FeaturePython)
  n = 2
  ref = C_element
FEATURE [App::DocumentObjectGroupPython] H_element082  label="H_element : 044"  # scripted group (container) (typed FeaturePython)
  n = 4
  ref = H_element
FEATURE [App::DocumentObjectGroupPython] O_element082  label="O_element : 043"  # scripted group (container) (typed FeaturePython)
  n = 1
  ref = O_element
FEATURE [App::DocumentObjectGroupPython] G4_POLYVINYL_ALCOHOL  # scripted group (container) (typed FeaturePython)
  Dunit = g/cm3
  Dvalue = 1.3
  Group = -> [C_element090,H_element082,O_element082]
  conduct = 2
  density = 1
  expand = 3
  formula = G4_POLYVINYL_ALCOHOL
  name = G4_POLYVINYL_ALCOHOL
  specific = 4
FEATURE [App::DocumentObjectGroupPython] C_element091  label="C_element : 049"  # scripted group (container) (typed FeaturePython)
  n = 8
  ref = C_element
FEATURE [App::DocumentObjectGroupPython] H_element083  label="H_element : 045"  # scripted group (container) (typed FeaturePython)
  n = 14
  ref = H_element
FEATURE [App::DocumentObjectGroupPython] O_element083  label="O_element : 044"  # scripted group (container) (typed FeaturePython)
  n = 2
  ref = O_element
FEATURE [App::DocumentObjectGroupPython] G4_POLYVINYL_BUTYRAL  # scripted group (container) (typed FeaturePython)
  Dunit = g/cm3
  Dvalue = 1.12
  Group = -> [C_element091,H_element083,O_element083]
  conduct = 2
  density = 1
  expand = 3
  formula = G4_POLYVINYL_BUTYRAL
  name = G4_POLYVINYL_BUTYRAL
  specific = 4
FEATURE [App::DocumentObjectGroupPython] C_element092  label="C_element : 050"  # scripted group (container) (typed FeaturePython)
  n = 2
  ref = C_element
FEATURE [App::DocumentObjectGroupPython] H_element084  label="H_element : 046"  # scripted group (container) (typed FeaturePython)
  n = 3
  ref = H_element
FEATURE [App::DocumentObjectGroupPython] Cl_element019  label="Cl_element : 009"  # scripted group (container) (typed FeaturePython)
  n = 1
  ref = Cl_element
FEATURE [App::DocumentObjectGroupPython] G4_POLYVINYL_CHLORIDE  # scripted group (container) (typed FeaturePython)
  Dunit = g/cm3
  Dvalue = 1.3
  Group = -> [C_element092,H_element084,Cl_element019]
  conduct = 2
  density = 1
  expand = 3
  formula = G4_POLYVINYL_CHLORIDE
  name = G4_POLYVINYL_CHLORIDE
  specific = 4
FEATURE [App::DocumentObjectGroupPython] C_element093  label="C_element : 051"  # scripted group (container) (typed FeaturePython)
  n = 2
  ref = C_element
FEATURE [App::DocumentObjectGroupPython] H_element085  label="H_element : 047"  # scripted group (container) (typed FeaturePython)
  n = 2
  ref = H_element
FEATURE [App::DocumentObjectGroupPython] Cl_element020  label="Cl_element : 010"  # scripted group (container) (typed FeaturePython)
  n = 2
  ref = Cl_element
FEATURE [App::DocumentObjectGroupPython] G4_POLYVINYLIDENE_CHLORIDE  # scripted group (container) (typed FeaturePython)
  Dunit = g/cm3
  Dvalue = 1.7
  Group = -> [C_element093,H_element085,Cl_element020]
  conduct = 2
  density = 1
  expand = 3
  formula = G4_POLYVINYLIDENE_CHLORIDE
  name = G4_POLYVINYLIDENE_CHLORIDE
  specific = 4
FEATURE [App::DocumentObjectGroupPython] C_element094  label="C_element : 052"  # scripted group (container) (typed FeaturePython)
  n = 2
  ref = C_element
FEATURE [App::DocumentObjectGroupPython] H_element086  label="H_element : 048"  # scripted group (container) (typed FeaturePython)
  n = 2
  ref = H_element
FEATURE [App::DocumentObjectGroupPython] F_element016  label="F_element : 007"  # scripted group (container) (typed FeaturePython)
  n = 2
  ref = F_element
FEATURE [App::DocumentObjectGroupPython] G4_POLYVINYLIDENE_FLUORIDE  # scripted group (container) (typed FeaturePython)
  Dunit = g/cm3
  Dvalue = 1.76
  Group = -> [C_element094,H_element086,F_element016]
  conduct = 2
  density = 1
  expand = 3
  formula = G4_POLYVINYLIDENE_FLUORIDE
  name = G4_POLYVINYLIDENE_FLUORIDE
  specific = 4
FEATURE [App::DocumentObjectGroupPython] C_element095  label="C_element : 053"  # scripted group (container) (typed FeaturePython)
  n = 6
  ref = C_element
FEATURE [App::DocumentObjectGroupPython] H_element087  label="H_element : 9"  # scripted group (container) (typed FeaturePython)
  n = 9
  ref = H_element
FEATURE [App::DocumentObjectGroupPython] N_element037  label="N_element : 016"  # scripted group (container) (typed FeaturePython)
  n = 1
  ref = N_element
FEATURE [App::DocumentObjectGroupPython] O_element084  label="O_element : 045"  # scripted group (container) (typed FeaturePython)
  n = 1
  ref = O_element
FEATURE [App::DocumentObjectGroupPython] G4_POLYVINYL_PYRROLIDONE  # scripted group (container) (typed FeaturePython)
  Dunit = g/cm3
  Dvalue = 1.25
  Group = -> [C_element095,H_element087,N_element037,O_element084]
  conduct = 2
  density = 1
  expand = 3
  formula = G4_POLYVINYL_PYRROLIDONE
  name = G4_POLYVINYL_PYRROLIDONE
  specific = 4
FEATURE [App::DocumentObjectGroupPython] K_element008  label="K_element : 1"  # scripted group (container) (typed FeaturePython)
  n = 1
  ref = K_element
FEATURE [App::DocumentObjectGroupPython] I_element006  label="I_element : 003"  # scripted group (container) (typed FeaturePython)
  n = 1
  ref = I_element
FEATURE [App::DocumentObjectGroupPython] G4_POTASSIUM_IODIDE  # scripted group (container) (typed FeaturePython)
  Dunit = g/cm3
  Dvalue = 3.13
  Group = -> [K_element008,I_element006]
  conduct = 2
  density = 1
  expand = 3
  formula = G4_POTASSIUM_IODIDE
  name = G4_POTASSIUM_IODIDE
  specific = 4
FEATURE [App::DocumentObjectGroupPython] K_element009  label="K_element : 2"  # scripted group (container) (typed FeaturePython)
  n = 2
  ref = K_element
FEATURE [App::DocumentObjectGroupPython] O_element085  label="O_element : 046"  # scripted group (container) (typed FeaturePython)
  n = 1
  ref = O_element
FEATURE [App::DocumentObjectGroupPython] G4_POTASSIUM_OXIDE  # scripted group (container) (typed FeaturePython)
  Dunit = g/cm3
  Dvalue = 2.32
  Group = -> [K_element009,O_element085]
  conduct = 2
  density = 1
  expand = 3
  formula = G4_POTASSIUM_OXIDE
  name = G4_POTASSIUM_OXIDE
  specific = 4
FEATURE [App::DocumentObjectGroupPython] C_element096  label="C_element : 054"  # scripted group (container) (typed FeaturePython)
  n = 3
  ref = C_element
FEATURE [App::DocumentObjectGroupPython] H_element088  label="H_element : 049"  # scripted group (container) (typed FeaturePython)
  n = 8
  ref = H_element
FEATURE [App::DocumentObjectGroupPython] G4_PROPANE  # scripted group (container) (typed FeaturePython)
  Dunit = g/cm3
  Dvalue = 0.00187939
  Group = -> [C_element096,H_element088]
  conduct = 2
  density = 1
  expand = 3
  formula = G4_PROPANE
  name = G4_PROPANE
  specific = 4
FEATURE [App::DocumentObjectGroupPython] C_element097  label="C_element : 055"  # scripted group (container) (typed FeaturePython)
  n = 3
  ref = C_element
FEATURE [App::DocumentObjectGroupPython] H_element089  label="H_element : 050"  # scripted group (container) (typed FeaturePython)
  n = 8
  ref = H_element
FEATURE [App::DocumentObjectGroupPython] G4_lPROPANE  # scripted group (container) (typed FeaturePython)
  Dunit = g/cm3
  Dvalue = 0.43
  Group = -> [C_element097,H_element089]
  conduct = 2
  density = 1
  expand = 3
  formula = G4_lPROPANE
  name = G4_lPROPANE
  specific = 4
FEATURE [App::DocumentObjectGroupPython] C_element098  label="C_element : 056"  # scripted group (container) (typed FeaturePython)
  n = 3
  ref = C_element
FEATURE [App::DocumentObjectGroupPython] H_element090  label="H_element : 051"  # scripted group (container) (typed FeaturePython)
  n = 8
  ref = H_element
FEATURE [App::DocumentObjectGroupPython] O_element086  label="O_element : 047"  # scripted group (container) (typed FeaturePython)
  n = 1
  ref = O_element
FEATURE [App::DocumentObjectGroupPython] G4_N_PROPYL_ALCOHOL  label="G4_N-PROPYL_ALCOHOL"  # scripted group (container) (typed FeaturePython)
  Dunit = g/cm3
  Dvalue = 0.8035
  Group = -> [C_element098,H_element090,O_element086]
  conduct = 2
  density = 1
  expand = 3
  formula = G4_N-PROPYL_ALCOHOL
  name = G4_N-PROPYL_ALCOHOL
  specific = 4
FEATURE [App::DocumentObjectGroupPython] C_element099  label="C_element : 057"  # scripted group (container) (typed FeaturePython)
  n = 5
  ref = C_element
FEATURE [App::DocumentObjectGroupPython] H_element091  label="H_element : 052"  # scripted group (container) (typed FeaturePython)
  n = 5
  ref = H_element
FEATURE [App::DocumentObjectGroupPython] N_element038  label="N_element : 017"  # scripted group (container) (typed FeaturePython)
  n = 1
  ref = N_element
FEATURE [App::DocumentObjectGroupPython] G4_PYRIDINE  # scripted group (container) (typed FeaturePython)
  Dunit = g/cm3
  Dvalue = 0.9819
  Group = -> [C_element099,H_element091,N_element038]
  conduct = 2
  density = 1
  expand = 3
  formula = G4_PYRIDINE
  name = G4_PYRIDINE
  specific = 4
FEATURE [App::DocumentObjectGroupPython] H_element092  label="H_element : 0.144"  # scripted group (container) (typed FeaturePython)
  n = 0.143711
FEATURE [App::DocumentObjectGroupPython] C_element100  label="C_element : 0.856"  # scripted group (container) (typed FeaturePython)
  n = 0.856289
FEATURE [App::DocumentObjectGroupPython] G4_RUBBER_BUTYL  # scripted group (container) (typed FeaturePython)
  Dunit = g/cm3
  Dvalue = 0.92
  Group = -> [H_element092,C_element100]
  conduct = 2
  density = 1
  expand = 3
  formula = G4_RUBBER_BUTYL
  name = G4_RUBBER_BUTYL
  specific = 4
FEATURE [App::DocumentObjectGroupPython] H_element093  label="H_element : 0.118"  # scripted group (container) (typed FeaturePython)
  n = 0.118371
FEATURE [App::DocumentObjectGroupPython] C_element101  label="C_element : 0.882"  # scripted group (container) (typed FeaturePython)
  n = 0.881629
FEATURE [App::DocumentObjectGroupPython] G4_RUBBER_NATURAL  # scripted group (container) (typed FeaturePython)
  Dunit = g/cm3
  Dvalue = 0.92
  Group = -> [H_element093,C_element101]
  conduct = 2
  density = 1
  expand = 3
  formula = G4_RUBBER_NATURAL
  name = G4_RUBBER_NATURAL
  specific = 4
FEATURE [App::DocumentObjectGroupPython] H_element094  label="H_element : 0.145"  # scripted group (container) (typed FeaturePython)
  n = 0.05692
FEATURE [App::DocumentObjectGroupPython] C_element102  label="C_element : 0.543"  # scripted group (container) (typed FeaturePython)
  n = 0.542646
FEATURE [App::DocumentObjectGroupPython] Cl_element021  label="Cl_element : 0.400"  # scripted group (container) (typed FeaturePython)
  n = 0.400434
FEATURE [App::DocumentObjectGroupPython] G4_RUBBER_NEOPRENE  # scripted group (container) (typed FeaturePython)
  Dunit = g/cm3
  Dvalue = 1.23
  Group = -> [H_element094,C_element102,Cl_element021]
  conduct = 2
  density = 1
  expand = 3
  formula = G4_RUBBER_NEOPRENE
  name = G4_RUBBER_NEOPRENE
  specific = 4
FEATURE [App::DocumentObjectGroupPython] Si_element006  label="Si_element : 1"  # scripted group (container) (typed FeaturePython)
  n = 1
  ref = Si_element
FEATURE [App::DocumentObjectGroupPython] O_element087  label="O_element : 048"  # scripted group (container) (typed FeaturePython)
  n = 2
  ref = O_element
FEATURE [App::DocumentObjectGroupPython] G4_SILICON_DIOXIDE  # scripted group (container) (typed FeaturePython)
  Dunit = g/cm3
  Dvalue = 2.32
  Group = -> [Si_element006,O_element087]
  conduct = 2
  density = 1
  expand = 3
  formula = G4_SILICON_DIOXIDE
  name = G4_SILICON_DIOXIDE
  specific = 4
FEATURE [App::DocumentObjectGroupPython] Ag_element002  label="Ag_element : 1"  # scripted group (container) (typed FeaturePython)
  n = 1
  ref = Ag_element
FEATURE [App::DocumentObjectGroupPython] Br_element005  label="Br_element : 003"  # scripted group (container) (typed FeaturePython)
  n = 1
  ref = Br_element
FEATURE [App::DocumentObjectGroupPython] G4_SILVER_BROMIDE  # scripted group (container) (typed FeaturePython)
  Dunit = g/cm3
  Dvalue = 6.473
  Group = -> [Ag_element002,Br_element005]
  conduct = 2
  density = 1
  expand = 3
  formula = G4_SILVER_BROMIDE
  name = G4_SILVER_BROMIDE
  specific = 4
FEATURE [App::DocumentObjectGroupPython] Ag_element003  label="Ag_element : 002"  # scripted group (container) (typed FeaturePython)
  n = 1
  ref = Ag_element
FEATURE [App::DocumentObjectGroupPython] Cl_element022  label="Cl_element : 011"  # scripted group (container) (typed FeaturePython)
  n = 1
  ref = Cl_element
FEATURE [App::DocumentObjectGroupPython] G4_SILVER_CHLORIDE  # scripted group (container) (typed FeaturePython)
  Dunit = g/cm3
  Dvalue = 5.56
  Group = -> [Ag_element003,Cl_element022]
  conduct = 2
  density = 1
  expand = 3
  formula = G4_SILVER_CHLORIDE
  name = G4_SILVER_CHLORIDE
  specific = 4
FEATURE [App::DocumentObjectGroupPython] Br_element006  label="Br_element : 0.423"  # scripted group (container) (typed FeaturePython)
  n = 0.422895
FEATURE [App::DocumentObjectGroupPython] Ag_element004  label="Ag_element : 0.574"  # scripted group (container) (typed FeaturePython)
  n = 0.573748
FEATURE [App::DocumentObjectGroupPython] I_element007  label="I_element : 0.649"  # scripted group (container) (typed FeaturePython)
  n = 0.003357
FEATURE [App::DocumentObjectGroupPython] G4_SILVER_HALIDES  # scripted group (container) (typed FeaturePython)
  Dunit = g/cm3
  Dvalue = 6.47
  Group = -> [Br_element006,Ag_element004,I_element007]
  conduct = 2
  density = 1
  expand = 3
  formula = G4_SILVER_HALIDES
  name = G4_SILVER_HALIDES
  specific = 4
FEATURE [App::DocumentObjectGroupPython] Ag_element005  label="Ag_element : 003"  # scripted group (container) (typed FeaturePython)
  n = 1
  ref = Ag_element
FEATURE [App::DocumentObjectGroupPython] I_element008  label="I_element : 004"  # scripted group (container) (typed FeaturePython)
  n = 1
  ref = I_element
FEATURE [App::DocumentObjectGroupPython] G4_SILVER_IODIDE  # scripted group (container) (typed FeaturePython)
  Dunit = g/cm3
  Dvalue = 6.01
  Group = -> [Ag_element005,I_element008]
  conduct = 2
  density = 1
  expand = 3
  formula = G4_SILVER_IODIDE
  name = G4_SILVER_IODIDE
  specific = 4
FEATURE [App::DocumentObjectGroupPython] H_element095  label="H_element : 0.100"  # scripted group (container) (typed FeaturePython)
  n = 0.1
FEATURE [App::DocumentObjectGroupPython] C_element103  label="C_element : 0.204"  # scripted group (container) (typed FeaturePython)
  n = 0.204
FEATURE [App::DocumentObjectGroupPython] N_element039  label="N_element : 0.759"  # scripted group (container) (typed FeaturePython)
  n = 0.042
FEATURE [App::DocumentObjectGroupPython] O_element088  label="O_element : 0.645"  # scripted group (container) (typed FeaturePython)
  n = 0.645
FEATURE [App::DocumentObjectGroupPython] Na_element013  label="Na_element : 0.100"  # scripted group (container) (typed FeaturePython)
  n = 0.002
FEATURE [App::DocumentObjectGroupPython] P_element009  label="P_element : 0.107"  # scripted group (container) (typed FeaturePython)
  n = 0.001
FEATURE [App::DocumentObjectGroupPython] S_element020  label="S_element : 0.021"  # scripted group (container) (typed FeaturePython)
  n = 0.002
FEATURE [App::DocumentObjectGroupPython] Cl_element023  label="Cl_element : 0.590"  # scripted group (container) (typed FeaturePython)
  n = 0.003
FEATURE [App::DocumentObjectGroupPython] K_element010  label="K_element : 0.001"  # scripted group (container) (typed FeaturePython)
  n = 0.001
FEATURE [App::DocumentObjectGroupPython] G4_SKIN_ICRP  # scripted group (container) (typed FeaturePython)
  Dunit = g/cm3
  Dvalue = 1.09
  Group = -> [H_element095,C_element103,N_element039,O_element088,Na_element013,P_element009,S_element020,Cl_element023,K_element010]
  conduct = 2
  density = 1
  expand = 3
  formula = G4_SKIN_ICRP
  name = G4_SKIN_ICRP
  specific = 4
FEATURE [App::DocumentObjectGroupPython] Na_element014  label="Na_element : 2"  # scripted group (container) (typed FeaturePython)
  n = 2
  ref = Na_element
FEATURE [App::DocumentObjectGroupPython] C_element104  label="C_element : 058"  # scripted group (container) (typed FeaturePython)
  n = 1
  ref = C_element
FEATURE [App::DocumentObjectGroupPython] O_element089  label="O_element : 049"  # scripted group (container) (typed FeaturePython)
  n = 3
  ref = O_element
FEATURE [App::DocumentObjectGroupPython] G4_SODIUM_CARBONATE  # scripted group (container) (typed FeaturePython)
  Dunit = g/cm3
  Dvalue = 2.532
  Group = -> [Na_element014,C_element104,O_element089]
  conduct = 2
  density = 1
  expand = 3
  formula = G4_SODIUM_CARBONATE
  name = G4_SODIUM_CARBONATE
  specific = 4
FEATURE [App::DocumentObjectGroupPython] Na_element015  label="Na_element : 1"  # scripted group (container) (typed FeaturePython)
  n = 1
  ref = Na_element
FEATURE [App::DocumentObjectGroupPython] I_element009  label="I_element : 005"  # scripted group (container) (typed FeaturePython)
  n = 1
  ref = I_element
FEATURE [App::DocumentObjectGroupPython] G4_SODIUM_IODIDE  # scripted group (container) (typed FeaturePython)
  Dunit = g/cm3
  Dvalue = 3.667
  Group = -> [Na_element015,I_element009]
  conduct = 2
  density = 1
  expand = 3
  formula = G4_SODIUM_IODIDE
  name = G4_SODIUM_IODIDE
  specific = 4
FEATURE [App::DocumentObjectGroupPython] Na_element016  label="Na_element : 003"  # scripted group (container) (typed FeaturePython)
  n = 2
  ref = Na_element
FEATURE [App::DocumentObjectGroupPython] O_element090  label="O_element : 050"  # scripted group (container) (typed FeaturePython)
  n = 1
  ref = O_element
FEATURE [App::DocumentObjectGroupPython] G4_SODIUM_MONOXIDE  # scripted group (container) (typed FeaturePython)
  Dunit = g/cm3
  Dvalue = 2.27
  Group = -> [Na_element016,O_element090]
  conduct = 2
  density = 1
  expand = 3
  formula = G4_SODIUM_MONOXIDE
  name = G4_SODIUM_MONOXIDE
  specific = 4
FEATURE [App::DocumentObjectGroupPython] Na_element017  label="Na_element : 004"  # scripted group (container) (typed FeaturePython)
  n = 1
  ref = Na_element
FEATURE [App::DocumentObjectGroupPython] N_element040  label="N_element : 018"  # scripted group (container) (typed FeaturePython)
  n = 1
  ref = N_element
FEATURE [App::DocumentObjectGroupPython] O_element091  label="O_element : 051"  # scripted group (container) (typed FeaturePython)
  n = 3
  ref = O_element
FEATURE [App::DocumentObjectGroupPython] G4_SODIUM_NITRATE  # scripted group (container) (typed FeaturePython)
  Dunit = g/cm3
  Dvalue = 2.261
  Group = -> [Na_element017,N_element040,O_element091]
  conduct = 2
  density = 1
  expand = 3
  formula = G4_SODIUM_NITRATE
  name = G4_SODIUM_NITRATE
  specific = 4
FEATURE [App::DocumentObjectGroupPython] C_element105  label="C_element : 059"  # scripted group (container) (typed FeaturePython)
  n = 14
  ref = C_element
FEATURE [App::DocumentObjectGroupPython] H_element096  label="H_element : 053"  # scripted group (container) (typed FeaturePython)
  n = 12
  ref = H_element
FEATURE [App::DocumentObjectGroupPython] G4_STILBENE  # scripted group (container) (typed FeaturePython)
  Dunit = g/cm3
  Dvalue = 0.9707
  Group = -> [C_element105,H_element096]
  conduct = 2
  density = 1
  expand = 3
  formula = G4_STILBENE
  name = G4_STILBENE
  specific = 4
FEATURE [App::DocumentObjectGroupPython] C_element106  label="C_element : 12"  # scripted group (container) (typed FeaturePython)
  n = 12
  ref = C_element
FEATURE [App::DocumentObjectGroupPython] H_element097  label="H_element : 22"  # scripted group (container) (typed FeaturePython)
  n = 22
  ref = H_element
FEATURE [App::DocumentObjectGroupPython] O_element092  label="O_element : 11"  # scripted group (container) (typed FeaturePython)
  n = 11
  ref = O_element
FEATURE [App::DocumentObjectGroupPython] G4_SUCROSE  # scripted group (container) (typed FeaturePython)
  Dunit = g/cm3
  Dvalue = 1.5805
  Group = -> [C_element106,H_element097,O_element092]
  conduct = 2
  density = 1
  expand = 3
  formula = G4_SUCROSE
  name = G4_SUCROSE
  specific = 4
FEATURE [App::DocumentObjectGroupPython] C_element107  label="C_element : 18"  # scripted group (container) (typed FeaturePython)
  n = 18
  ref = C_element
FEATURE [App::DocumentObjectGroupPython] H_element098  label="H_element : 054"  # scripted group (container) (typed FeaturePython)
  n = 14
  ref = H_element
FEATURE [App::DocumentObjectGroupPython] G4_TERPHENYL  # scripted group (container) (typed FeaturePython)
  Dunit = g/cm3
  Dvalue = 1.24
  Group = -> [C_element107,H_element098]
  conduct = 2
  density = 1
  expand = 3
  formula = G4_TERPHENYL
  name = G4_TERPHENYL
  specific = 4
FEATURE [App::DocumentObjectGroupPython] H_element099  label="H_element : 0.146"  # scripted group (container) (typed FeaturePython)
  n = 0.106
FEATURE [App::DocumentObjectGroupPython] C_element108  label="C_element : 0.883"  # scripted group (container) (typed FeaturePython)
  n = 0.099
FEATURE [App::DocumentObjectGroupPython] N_element041  label="N_element : 0.020"  # scripted group (container) (typed FeaturePython)
  n = 0.02
FEATURE [App::DocumentObjectGroupPython] O_element093  label="O_element : 0.766"  # scripted group (container) (typed FeaturePython)
  n = 0.766
FEATURE [App::DocumentObjectGroupPython] Na_element018  label="Na_element : 0.101"  # scripted group (container) (typed FeaturePython)
  n = 0.002
FEATURE [App::DocumentObjectGroupPython] P_element010  label="P_element : 0.108"  # scripted group (container) (typed FeaturePython)
  n = 0.001
FEATURE [App::DocumentObjectGroupPython] S_element021  label="S_element : 0.022"  # scripted group (container) (typed FeaturePython)
  n = 0.002
FEATURE [App::DocumentObjectGroupPython] Cl_element024  label="Cl_element : 0.002"  # scripted group (container) (typed FeaturePython)
  n = 0.002
FEATURE [App::DocumentObjectGroupPython] K_element011  label="K_element : 0.017"  # scripted group (container) (typed FeaturePython)
  n = 0.002
FEATURE [App::DocumentObjectGroupPython] G4_TESTIS_ICRP  # scripted group (container) (typed FeaturePython)
  Dunit = g/cm3
  Dvalue = 1.04
  Group = -> [H_element099,C_element108,N_element041,O_element093,Na_element018,P_element010,S_element021,Cl_element024,K_element011]
  conduct = 2
  density = 1
  expand = 3
  formula = G4_TESTIS_ICRP
  name = G4_TESTIS_ICRP
  specific = 4
FEATURE [App::DocumentObjectGroupPython] C_element109  label="C_element : 060"  # scripted group (container) (typed FeaturePython)
  n = 2
  ref = C_element
FEATURE [App::DocumentObjectGroupPython] Cl_element025  label="Cl_element : 012"  # scripted group (container) (typed FeaturePython)
  n = 4
  ref = Cl_element
FEATURE [App::DocumentObjectGroupPython] G4_TETRACHLOROETHYLENE  # scripted group (container) (typed FeaturePython)
  Dunit = g/cm3
  Dvalue = 1.625
  Group = -> [C_element109,Cl_element025]
  conduct = 2
  density = 1
  expand = 3
  formula = G4_TETRACHLOROETHYLENE
  name = G4_TETRACHLOROETHYLENE
  specific = 4
FEATURE [App::DocumentObjectGroupPython] Tl_element001  label="Tl_element : 1"  # scripted group (container) (typed FeaturePython)
  n = 1
  ref = Tl_element
FEATURE [App::DocumentObjectGroupPython] Cl_element026  label="Cl_element : 013"  # scripted group (container) (typed FeaturePython)
  n = 1
  ref = Cl_element
FEATURE [App::DocumentObjectGroupPython] G4_THALLIUM_CHLORIDE  # scripted group (container) (typed FeaturePython)
  Dunit = g/cm3
  Dvalue = 7.004
  Group = -> [Tl_element001,Cl_element026]
  conduct = 2
  density = 1
  expand = 3
  formula = G4_THALLIUM_CHLORIDE
  name = G4_THALLIUM_CHLORIDE
  specific = 4
FEATURE [App::DocumentObjectGroupPython] H_element100  label="H_element : 0.147"  # scripted group (container) (typed FeaturePython)
  n = 0.105
FEATURE [App::DocumentObjectGroupPython] C_element110  label="C_element : 0.256"  # scripted group (container) (typed FeaturePython)
  n = 0.256
FEATURE [App::DocumentObjectGroupPython] N_element042  label="N_element : 0.760"  # scripted group (container) (typed FeaturePython)
  n = 0.027
FEATURE [App::DocumentObjectGroupPython] O_element094  label="O_element : 0.602"  # scripted group (container) (typed FeaturePython)
  n = 0.602
FEATURE [App::DocumentObjectGroupPython] Na_element019  label="Na_element : 0.102"  # scripted group (container) (typed FeaturePython)
  n = 0.001
FEATURE [App::DocumentObjectGroupPython] P_element011  label="P_element : 0.109"  # scripted group (container) (typed FeaturePython)
  n = 0.002
FEATURE [App::DocumentObjectGroupPython] S_element022  label="S_element : 0.023"  # scripted group (container) (typed FeaturePython)
  n = 0.003
FEATURE [App::DocumentObjectGroupPython] Cl_element027  label="Cl_element : 0.591"  # scripted group (container) (typed FeaturePython)
  n = 0.002
FEATURE [App::DocumentObjectGroupPython] K_element012  label="K_element : 0.018"  # scripted group (container) (typed FeaturePython)
  n = 0.002
FEATURE [App::DocumentObjectGroupPython] G4_TISSUE_SOFT_ICRP  # scripted group (container) (typed FeaturePython)
  Dunit = g/cm3
  Dvalue = 1.03
  Group = -> [H_element100,C_element110,N_element042,O_element094,Na_element019,P_element011,S_element022,Cl_element027,K_element012]
  conduct = 2
  density = 1
  expand = 3
  formula = G4_TISSUE_SOFT_ICRP
  name = G4_TISSUE_SOFT_ICRP
  specific = 4
FEATURE [App::DocumentObjectGroupPython] H_element101  label="H_element : 0.148"  # scripted group (container) (typed FeaturePython)
  n = 0.101
FEATURE [App::DocumentObjectGroupPython] C_element111  label="C_element : 0.111"  # scripted group (container) (typed FeaturePython)
  n = 0.111
FEATURE [App::DocumentObjectGroupPython] N_element043  label="N_element : 0.026"  # scripted group (container) (typed FeaturePython)
  n = 0.026
FEATURE [App::DocumentObjectGroupPython] O_element095  label="O_element : 0.762"  # scripted group (container) (typed FeaturePython)
  n = 0.762
FEATURE [App::DocumentObjectGroupPython] G4_TISSUE_SOFT_ICRU_4  label="G4_TISSUE_SOFT_ICRU-4"  # scripted group (container) (typed FeaturePython)
  Dunit = g/cm3
  Dvalue = 1
  Group = -> [H_element101,C_element111,N_element043,O_element095]
  conduct = 2
  density = 1
  expand = 3
  formula = G4_TISSUE_SOFT_ICRU-4
  name = G4_TISSUE_SOFT_ICRU-4
  specific = 4
FEATURE [App::DocumentObjectGroupPython] H_element102  label="H_element : 0.149"  # scripted group (container) (typed FeaturePython)
  n = 0.101869
FEATURE [App::DocumentObjectGroupPython] C_element112  label="C_element : 0.456"  # scripted group (container) (typed FeaturePython)
  n = 0.456179
FEATURE [App::DocumentObjectGroupPython] N_element044  label="N_element : 0.761"  # scripted group (container) (typed FeaturePython)
  n = 0.035172
FEATURE [App::DocumentObjectGroupPython] O_element096  label="O_element : 0.407"  # scripted group (container) (typed FeaturePython)
  n = 0.40678
FEATURE [App::DocumentObjectGroupPython] G4_TISSUE_METHANE  label="G4_TISSUE-METHANE"  # scripted group (container) (typed FeaturePython)
  Dunit = g/cm3
  Dvalue = 0.00106409
  Group = -> [H_element102,C_element112,N_element044,O_element096]
  conduct = 2
  density = 1
  expand = 3
  formula = G4_TISSUE-METHANE
  name = G4_TISSUE-METHANE
  specific = 4
FEATURE [App::DocumentObjectGroupPython] H_element103  label="H_element : 0.103"  # scripted group (container) (typed FeaturePython)
  n = 0.102672
FEATURE [App::DocumentObjectGroupPython] C_element113  label="C_element : 0.569"  # scripted group (container) (typed FeaturePython)
  n = 0.56894
FEATURE [App::DocumentObjectGroupPython] N_element045  label="N_element : 0.762"  # scripted group (container) (typed FeaturePython)
  n = 0.035022
FEATURE [App::DocumentObjectGroupPython] O_element097  label="O_element : 0.293"  # scripted group (container) (typed FeaturePython)
  n = 0.293366
FEATURE [App::DocumentObjectGroupPython] G4_TISSUE_PROPANE  label="G4_TISSUE-PROPANE"  # scripted group (container) (typed FeaturePython)
  Dunit = g/cm3
  Dvalue = 0.00182628
  Group = -> [H_element103,C_element113,N_element045,O_element097]
  conduct = 2
  density = 1
  expand = 3
  formula = G4_TISSUE-PROPANE
  name = G4_TISSUE-PROPANE
  specific = 4
FEATURE [App::DocumentObjectGroupPython] Ti_element003  label="Ti_element : 1"  # scripted group (container) (typed FeaturePython)
  n = 1
  ref = Ti_element
FEATURE [App::DocumentObjectGroupPython] O_element098  label="O_element : 052"  # scripted group (container) (typed FeaturePython)
  n = 2
  ref = O_element
FEATURE [App::DocumentObjectGroupPython] G4_TITANIUM_DIOXIDE  # scripted group (container) (typed FeaturePython)
  Dunit = g/cm3
  Dvalue = 4.26
  Group = -> [Ti_element003,O_element098]
  conduct = 2
  density = 1
  expand = 3
  formula = G4_TITANIUM_DIOXIDE
  name = G4_TITANIUM_DIOXIDE
  specific = 4
FEATURE [App::DocumentObjectGroupPython] C_element114  label="C_element : 061"  # scripted group (container) (typed FeaturePython)
  n = 7
  ref = C_element
FEATURE [App::DocumentObjectGroupPython] H_element104  label="H_element : 055"  # scripted group (container) (typed FeaturePython)
  n = 8
  ref = H_element
FEATURE [App::DocumentObjectGroupPython] G4_TOLUENE  # scripted group (container) (typed FeaturePython)
  Dunit = g/cm3
  Dvalue = 0.8669
  Group = -> [C_element114,H_element104]
  conduct = 2
  density = 1
  expand = 3
  formula = G4_TOLUENE
  name = G4_TOLUENE
  specific = 4
FEATURE [App::DocumentObjectGroupPython] C_element115  label="C_element : 062"  # scripted group (container) (typed FeaturePython)
  n = 2
  ref = C_element
FEATURE [App::DocumentObjectGroupPython] H_element105  label="H_element : 056"  # scripted group (container) (typed FeaturePython)
  n = 1
  ref = H_element
FEATURE [App::DocumentObjectGroupPython] Cl_element028  label="Cl_element : 014"  # scripted group (container) (typed FeaturePython)
  n = 3
  ref = Cl_element
FEATURE [App::DocumentObjectGroupPython] G4_TRICHLOROETHYLENE  # scripted group (container) (typed FeaturePython)
  Dunit = g/cm3
  Dvalue = 1.46
  Group = -> [C_element115,H_element105,Cl_element028]
  conduct = 2
  density = 1
  expand = 3
  formula = G4_TRICHLOROETHYLENE
  name = G4_TRICHLOROETHYLENE
  specific = 4
FEATURE [App::DocumentObjectGroupPython] C_element116  label="C_element : 063"  # scripted group (container) (typed FeaturePython)
  n = 6
  ref = C_element
FEATURE [App::DocumentObjectGroupPython] H_element106  label="H_element : 15"  # scripted group (container) (typed FeaturePython)
  n = 15
  ref = H_element
FEATURE [App::DocumentObjectGroupPython] O_element099  label="O_element : 053"  # scripted group (container) (typed FeaturePython)
  n = 4
  ref = O_element
FEATURE [App::DocumentObjectGroupPython] P_element012  label="P_element : 1"  # scripted group (container) (typed FeaturePython)
  n = 1
  ref = P_element
FEATURE [App::DocumentObjectGroupPython] G4_TRIETHYL_PHOSPHATE  # scripted group (container) (typed FeaturePython)
  Dunit = g/cm3
  Dvalue = 1.07
  Group = -> [C_element116,H_element106,O_element099,P_element012]
  conduct = 2
  density = 1
  expand = 3
  formula = G4_TRIETHYL_PHOSPHATE
  name = G4_TRIETHYL_PHOSPHATE
  specific = 4
FEATURE [App::DocumentObjectGroupPython] W_element003  label="W_element : 003"  # scripted group (container) (typed FeaturePython)
  n = 1
  ref = W_element
FEATURE [App::DocumentObjectGroupPython] F_element017  label="F_element : 6"  # scripted group (container) (typed FeaturePython)
  n = 6
  ref = F_element
FEATURE [App::DocumentObjectGroupPython] G4_TUNGSTEN_HEXAFLUORIDE  # scripted group (container) (typed FeaturePython)
  Dunit = g/cm3
  Dvalue = 2.4
  Group = -> [W_element003,F_element017]
  conduct = 2
  density = 1
  expand = 3
  formula = G4_TUNGSTEN_HEXAFLUORIDE
  name = G4_TUNGSTEN_HEXAFLUORIDE
  specific = 4
FEATURE [App::DocumentObjectGroupPython] U_element001  label="U_element : 1"  # scripted group (container) (typed FeaturePython)
  n = 1
  ref = U_element
FEATURE [App::DocumentObjectGroupPython] C_element117  label="C_element : 064"  # scripted group (container) (typed FeaturePython)
  n = 2
  ref = C_element
FEATURE [App::DocumentObjectGroupPython] G4_URANIUM_DICARBIDE  # scripted group (container) (typed FeaturePython)
  Dunit = g/cm3
  Dvalue = 11.28
  Group = -> [U_element001,C_element117]
  conduct = 2
  density = 1
  expand = 3
  formula = G4_URANIUM_DICARBIDE
  name = G4_URANIUM_DICARBIDE
  specific = 4
FEATURE [App::DocumentObjectGroupPython] U_element002  label="U_element : 002"  # scripted group (container) (typed FeaturePython)
  n = 1
  ref = U_element
FEATURE [App::DocumentObjectGroupPython] C_element118  label="C_element : 065"  # scripted group (container) (typed FeaturePython)
  n = 1
  ref = C_element
FEATURE [App::DocumentObjectGroupPython] G4_URANIUM_MONOCARBIDE  # scripted group (container) (typed FeaturePython)
  Dunit = g/cm3
  Dvalue = 13.63
  Group = -> [U_element002,C_element118]
  conduct = 2
  density = 1
  expand = 3
  formula = G4_URANIUM_MONOCARBIDE
  name = G4_URANIUM_MONOCARBIDE
  specific = 4
FEATURE [App::DocumentObjectGroupPython] U_element003  label="U_element : 003"  # scripted group (container) (typed FeaturePython)
  n = 1
  ref = U_element
FEATURE [App::DocumentObjectGroupPython] O_element100  label="O_element : 054"  # scripted group (container) (typed FeaturePython)
  n = 2
  ref = O_element
FEATURE [App::DocumentObjectGroupPython] G4_URANIUM_OXIDE  # scripted group (container) (typed FeaturePython)
  Dunit = g/cm3
  Dvalue = 10.96
  Group = -> [U_element003,O_element100]
  conduct = 2
  density = 1
  expand = 3
  formula = G4_URANIUM_OXIDE
  name = G4_URANIUM_OXIDE
  specific = 4
FEATURE [App::DocumentObjectGroupPython] C_element119  label="C_element : 066"  # scripted group (container) (typed FeaturePython)
  n = 1
  ref = C_element
FEATURE [App::DocumentObjectGroupPython] H_element107  label="H_element : 057"  # scripted group (container) (typed FeaturePython)
  n = 4
  ref = H_element
FEATURE [App::DocumentObjectGroupPython] N_element046  label="N_element : 019"  # scripted group (container) (typed FeaturePython)
  n = 2
  ref = N_element
FEATURE [App::DocumentObjectGroupPython] O_element101  label="O_element : 055"  # scripted group (container) (typed FeaturePython)
  n = 1
  ref = O_element
FEATURE [App::DocumentObjectGroupPython] G4_UREA  # scripted group (container) (typed FeaturePython)
  Dunit = g/cm3
  Dvalue = 1.323
  Group = -> [C_element119,H_element107,N_element046,O_element101]
  conduct = 2
  density = 1
  expand = 3
  formula = G4_UREA
  name = G4_UREA
  specific = 4
FEATURE [App::DocumentObjectGroupPython] C_element120  label="C_element : 067"  # scripted group (container) (typed FeaturePython)
  n = 5
  ref = C_element
FEATURE [App::DocumentObjectGroupPython] H_element108  label="H_element : 058"  # scripted group (container) (typed FeaturePython)
  n = 11
  ref = H_element
FEATURE [App::DocumentObjectGroupPython] N_element047  label="N_element : 020"  # scripted group (container) (typed FeaturePython)
  n = 1
  ref = N_element
FEATURE [App::DocumentObjectGroupPython] O_element102  label="O_element : 056"  # scripted group (container) (typed FeaturePython)
  n = 2
  ref = O_element
FEATURE [App::DocumentObjectGroupPython] G4_VALINE  # scripted group (container) (typed FeaturePython)
  Dunit = g/cm3
  Dvalue = 1.23
  Group = -> [C_element120,H_element108,N_element047,O_element102]
  conduct = 2
  density = 1
  expand = 3
  formula = G4_VALINE
  name = G4_VALINE
  specific = 4
FEATURE [App::DocumentObjectGroupPython] H_element109  label="H_element : 0.009"  # scripted group (container) (typed FeaturePython)
  n = 0.009417
FEATURE [App::DocumentObjectGroupPython] C_element121  label="C_element : 0.281"  # scripted group (container) (typed FeaturePython)
  n = 0.280555
FEATURE [App::DocumentObjectGroupPython] F_element018  label="F_element : 0.710"  # scripted group (container) (typed FeaturePython)
  n = 0.710028
FEATURE [App::DocumentObjectGroupPython] G4_VITON  # scripted group (container) (typed FeaturePython)
  Dunit = g/cm3
  Dvalue = 1.8
  Group = -> [H_element109,C_element121,F_element018]
  conduct = 2
  density = 1
  expand = 3
  formula = G4_VITON
  name = G4_VITON
  specific = 4
FEATURE [App::DocumentObjectGroupPython] H_element110  label="H_element : 059"  # scripted group (container) (typed FeaturePython)
  n = 2
  ref = H_element
FEATURE [App::DocumentObjectGroupPython] O_element103  label="O_element : 057"  # scripted group (container) (typed FeaturePython)
  n = 1
  ref = O_element
FEATURE [App::DocumentObjectGroupPython] G4_WATER  # scripted group (container) (typed FeaturePython)
  Dunit = g/cm3
  Dvalue = 1
  Group = -> [H_element110,O_element103]
  conduct = 2
  density = 1
  expand = 3
  formula = G4_WATER
  name = G4_WATER
  specific = 4
FEATURE [App::DocumentObjectGroupPython] H_element111  label="H_element : 060"  # scripted group (container) (typed FeaturePython)
  n = 2
  ref = H_element
FEATURE [App::DocumentObjectGroupPython] O_element104  label="O_element : 058"  # scripted group (container) (typed FeaturePython)
  n = 1
  ref = O_element
FEATURE [App::DocumentObjectGroupPython] G4_WATER_VAPOR  # scripted group (container) (typed FeaturePython)
  Dunit = g/cm3
  Dvalue = 0.000756182
  Group = -> [H_element111,O_element104]
  conduct = 2
  density = 1
  expand = 3
  formula = G4_WATER_VAPOR
  name = G4_WATER_VAPOR
  specific = 4
FEATURE [App::DocumentObjectGroupPython] C_element122  label="C_element : 068"  # scripted group (container) (typed FeaturePython)
  n = 8
  ref = C_element
FEATURE [App::DocumentObjectGroupPython] H_element112  label="H_element : 061"  # scripted group (container) (typed FeaturePython)
  n = 10
  ref = H_element
FEATURE [App::DocumentObjectGroupPython] G4_XYLENE  # scripted group (container) (typed FeaturePython)
  Dunit = g/cm3
  Dvalue = 0.87
  Group = -> [C_element122,H_element112]
  conduct = 2
  density = 1
  expand = 3
  formula = G4_XYLENE
  name = G4_XYLENE
  specific = 4
FEATURE [App::DocumentObjectGroupPython] C_element123  label="C_element : 069"  # scripted group (container) (typed FeaturePython)
  n = 1
  ref = C_element
FEATURE [App::DocumentObjectGroupPython] G4_GRAPHITE  # scripted group (container) (typed FeaturePython)
  Dunit = g/cm3
  Dvalue = 2.21
  Group = -> [C_element123]
  conduct = 2
  density = 1
  expand = 3
  formula = G4_GRAPHITE
  name = G4_GRAPHITE
  specific = 4
FEATURE [App::DocumentObjectGroupPython] NIST  # scripted group (container) (typed FeaturePython)
  Group = -> [G4_A_150_TISSUE,G4_ACETONE,G4_ACETYLENE,G4_ADENINE,G4_ADIPOSE_TISSUE_ICRP,G4_AIR,G4_ALANINE,G4_ALUMINUM_OXIDE,G4_AMBER,G4_AMMONIA,G4_ANILINE,G4_ANTHRACENE,G4_B_100_BONE,G4_BAKELITE,G4_BARIUM_FLUORIDE,G4_BARIUM_SULFATE,G4_BENZENE,G4_BERYLLIUM_OXIDE,G4_BGO,G4_BLOOD_ICRP,G4_BONE_COMPACT_ICRU,G4_BONE_CORTICAL_ICRP,G4_BORON_CARBIDE,G4_BORON_OXIDE,G4_BRAIN_ICRP,G4_BUTANE,G4_N_BUTYL_ALCOHOL,G4_C_552,+152 more]
FEATURE [App::DocumentObjectGroupPython] H_element113  label="H_element : 062"  # scripted group (container) (typed FeaturePython)
  n = 1
  ref = H_element
FEATURE [App::DocumentObjectGroupPython] G4_H  # scripted group (container) (typed FeaturePython)
  Dunit = g/cm3
  Dvalue = 8.3748e-05
  Group = -> [H_element113]
  conduct = 2
  density = 1
  expand = 3
  formula = H
  name = G4_H
  specific = 4
FEATURE [App::DocumentObjectGroupPython] He_element001  label="He_element : 1"  # scripted group (container) (typed FeaturePython)
  n = 1
  ref = He_element
FEATURE [App::DocumentObjectGroupPython] G4_He  # scripted group (container) (typed FeaturePython)
  Dunit = g/cm3
  Dvalue = 0.000166322
  Group = -> [He_element001]
  conduct = 2
  density = 1
  expand = 3
  formula = He
  name = G4_He
  specific = 4
FEATURE [App::DocumentObjectGroupPython] Li_element008  label="Li_element : 008"  # scripted group (container) (typed FeaturePython)
  n = 1
  ref = Li_element
FEATURE [App::DocumentObjectGroupPython] G4_Li  # scripted group (container) (typed FeaturePython)
  Dunit = g/cm3
  Dvalue = 0.534
  Group = -> [Li_element008]
  conduct = 2
  density = 1
  expand = 3
  formula = Li
  name = G4_Li
  specific = 4
FEATURE [App::DocumentObjectGroupPython] Be_element002  label="Be_element : 002"  # scripted group (container) (typed FeaturePython)
  n = 1
  ref = Be_element
FEATURE [App::DocumentObjectGroupPython] G4_Be  # scripted group (container) (typed FeaturePython)
  Dunit = g/cm3
  Dvalue = 1.848
  Group = -> [Be_element002]
  conduct = 2
  density = 1
  expand = 3
  formula = Be
  name = G4_Be
  specific = 4
FEATURE [App::DocumentObjectGroupPython] B_element007  label="B_element : 007"  # scripted group (container) (typed FeaturePython)
  n = 1
  ref = B_element
FEATURE [App::DocumentObjectGroupPython] G4_B  # scripted group (container) (typed FeaturePython)
  Dunit = g/cm3
  Dvalue = 2.37
  Group = -> [B_element007]
  conduct = 2
  density = 1
  expand = 3
  formula = B
  name = G4_B
  specific = 4
FEATURE [App::DocumentObjectGroupPython] C_element124  label="C_element : 070"  # scripted group (container) (typed FeaturePython)
  n = 1
  ref = C_element
FEATURE [App::DocumentObjectGroupPython] G4_C  # scripted group (container) (typed FeaturePython)
  Dunit = g/cm3
  Dvalue = 2
  Group = -> [C_element124]
  conduct = 2
  density = 1
  expand = 3
  formula = C
  name = G4_C
  specific = 4
FEATURE [App::DocumentObjectGroupPython] N_element048  label="N_element : 021"  # scripted group (container) (typed FeaturePython)
  n = 1
  ref = N_element
FEATURE [App::DocumentObjectGroupPython] G4_N  # scripted group (container) (typed FeaturePython)
  Dunit = g/cm3
  Dvalue = 0.0011652
  Group = -> [N_element048]
  conduct = 2
  density = 1
  expand = 3
  formula = N
  name = G4_N
  specific = 4
FEATURE [App::DocumentObjectGroupPython] O_element105  label="O_element : 059"  # scripted group (container) (typed FeaturePython)
  n = 1
  ref = O_element
FEATURE [App::DocumentObjectGroupPython] G4_O  # scripted group (container) (typed FeaturePython)
  Dunit = g/cm3
  Dvalue = 0.00133151
  Group = -> [O_element105]
  conduct = 2
  density = 1
  expand = 3
  formula = O
  name = G4_O
  specific = 4
FEATURE [App::DocumentObjectGroupPython] F_element019  label="F_element : 008"  # scripted group (container) (typed FeaturePython)
  n = 1
  ref = F_element
FEATURE [App::DocumentObjectGroupPython] G4_F  # scripted group (container) (typed FeaturePython)
  Dunit = g/cm3
  Dvalue = 0.00158029
  Group = -> [F_element019]
  conduct = 2
  density = 1
  expand = 3
  formula = F
  name = G4_F
  specific = 4
FEATURE [App::DocumentObjectGroupPython] Ne_element001  label="Ne_element : 1"  # scripted group (container) (typed FeaturePython)
  n = 1
  ref = Ne_element
FEATURE [App::DocumentObjectGroupPython] G4_Ne  # scripted group (container) (typed FeaturePython)
  Dunit = g/cm3
  Dvalue = 0.000838505
  Group = -> [Ne_element001]
  conduct = 2
  density = 1
  expand = 3
  formula = Ne
  name = G4_Ne
  specific = 4
FEATURE [App::DocumentObjectGroupPython] Na_element020  label="Na_element : 005"  # scripted group (container) (typed FeaturePython)
  n = 1
  ref = Na_element
FEATURE [App::DocumentObjectGroupPython] G4_Na  # scripted group (container) (typed FeaturePython)
  Dunit = g/cm3
  Dvalue = 0.971
  Group = -> [Na_element020]
  conduct = 2
  density = 1
  expand = 3
  formula = Na
  name = G4_Na
  specific = 4
FEATURE [App::DocumentObjectGroupPython] Mg_element011  label="Mg_element : 005"  # scripted group (container) (typed FeaturePython)
  n = 1
  ref = Mg_element
FEATURE [App::DocumentObjectGroupPython] G4_Mg  # scripted group (container) (typed FeaturePython)
  Dunit = g/cm3
  Dvalue = 1.74
  Group = -> [Mg_element011]
  conduct = 2
  density = 1
  expand = 3
  formula = Mg
  name = G4_Mg
  specific = 4
FEATURE [App::DocumentObjectGroupPython] Al_element004  label="Al_element : 1"  # scripted group (container) (typed FeaturePython)
  n = 1
  ref = Al_element
FEATURE [App::DocumentObjectGroupPython] G4_Al  # scripted group (container) (typed FeaturePython)
  Dunit = g/cm3
  Dvalue = 2.699
  Group = -> [Al_element004]
  conduct = 2
  density = 1
  expand = 3
  formula = Al
  name = G4_Al
  specific = 4
FEATURE [App::DocumentObjectGroupPython] Si_element007  label="Si_element : 002"  # scripted group (container) (typed FeaturePython)
  n = 1
  ref = Si_element
FEATURE [App::DocumentObjectGroupPython] G4_Si  # scripted group (container) (typed FeaturePython)
  Dunit = g/cm3
  Dvalue = 2.33
  Group = -> [Si_element007]
  conduct = 2
  density = 1
  expand = 3
  formula = Si
  name = G4_Si
  specific = 4
FEATURE [App::DocumentObjectGroupPython] P_element013  label="P_element : 002"  # scripted group (container) (typed FeaturePython)
  n = 1
  ref = P_element
FEATURE [App::DocumentObjectGroupPython] G4_P  # scripted group (container) (typed FeaturePython)
  Dunit = g/cm3
  Dvalue = 2.2
  Group = -> [P_element013]
  conduct = 2
  density = 1
  expand = 3
  formula = P
  name = G4_P
  specific = 4
FEATURE [App::DocumentObjectGroupPython] S_element023  label="S_element : 007"  # scripted group (container) (typed FeaturePython)
  n = 1
  ref = S_element
FEATURE [App::DocumentObjectGroupPython] G4_S  # scripted group (container) (typed FeaturePython)
  Dunit = g/cm3
  Dvalue = 2
  Group = -> [S_element023]
  conduct = 2
  density = 1
  expand = 3
  formula = S
  name = G4_S
  specific = 4
FEATURE [App::DocumentObjectGroupPython] Cl_element029  label="Cl_element : 015"  # scripted group (container) (typed FeaturePython)
  n = 1
  ref = Cl_element
FEATURE [App::DocumentObjectGroupPython] G4_Cl  # scripted group (container) (typed FeaturePython)
  Dunit = g/cm3
  Dvalue = 0.00299473
  Group = -> [Cl_element029]
  conduct = 2
  density = 1
  expand = 3
  formula = Cl
  name = G4_Cl
  specific = 4
FEATURE [App::DocumentObjectGroupPython] Ar_element002  label="Ar_element : 1"  # scripted group (container) (typed FeaturePython)
  n = 1
  ref = Ar_element
FEATURE [App::DocumentObjectGroupPython] G4_Ar  # scripted group (container) (typed FeaturePython)
  Dunit = g/cm3
  Dvalue = 0.00166201
  Group = -> [Ar_element002]
  conduct = 2
  density = 1
  expand = 3
  formula = Ar
  name = G4_Ar
  specific = 4
FEATURE [App::DocumentObjectGroupPython] K_element013  label="K_element : 003"  # scripted group (container) (typed FeaturePython)
  n = 1
  ref = K_element
FEATURE [App::DocumentObjectGroupPython] G4_K  # scripted group (container) (typed FeaturePython)
  Dunit = g/cm3
  Dvalue = 0.862
  Group = -> [K_element013]
  conduct = 2
  density = 1
  expand = 3
  formula = K
  name = G4_K
  specific = 4
FEATURE [App::DocumentObjectGroupPython] Ca_element014  label="Ca_element : 007"  # scripted group (container) (typed FeaturePython)
  n = 1
  ref = Ca_element
FEATURE [App::DocumentObjectGroupPython] G4_Ca  # scripted group (container) (typed FeaturePython)
  Dunit = g/cm3
  Dvalue = 1.55
  Group = -> [Ca_element014]
  conduct = 2
  density = 1
  expand = 3
  formula = Ca
  name = G4_Ca
  specific = 4
FEATURE [App::DocumentObjectGroupPython] Sc_element001  label="Sc_element : 1"  # scripted group (container) (typed FeaturePython)
  n = 1
  ref = Sc_element
FEATURE [App::DocumentObjectGroupPython] G4_Sc  # scripted group (container) (typed FeaturePython)
  Dunit = g/cm3
  Dvalue = 2.989
  Group = -> [Sc_element001]
  conduct = 2
  density = 1
  expand = 3
  formula = Sc
  name = G4_Sc
  specific = 4
FEATURE [App::DocumentObjectGroupPython] Ti_element004  label="Ti_element : 002"  # scripted group (container) (typed FeaturePython)
  n = 1
  ref = Ti_element
FEATURE [App::DocumentObjectGroupPython] G4_Ti  # scripted group (container) (typed FeaturePython)
  Dunit = g/cm3
  Dvalue = 4.54
  Group = -> [Ti_element004]
  conduct = 2
  density = 1
  expand = 3
  formula = Ti
  name = G4_Ti
  specific = 4
FEATURE [App::DocumentObjectGroupPython] V_element001  label="V_element : 1"  # scripted group (container) (typed FeaturePython)
  n = 1
  ref = V_element
FEATURE [App::DocumentObjectGroupPython] G4_V  # scripted group (container) (typed FeaturePython)
  Dunit = g/cm3
  Dvalue = 6.11
  Group = -> [V_element001]
  conduct = 2
  density = 1
  expand = 3
  formula = V
  name = G4_V
  specific = 4
FEATURE [App::DocumentObjectGroupPython] Cr_element001  label="Cr_element : 1"  # scripted group (container) (typed FeaturePython)
  n = 1
  ref = Cr_element
FEATURE [App::DocumentObjectGroupPython] G4_Cr  # scripted group (container) (typed FeaturePython)
  Dunit = g/cm3
  Dvalue = 7.18
  Group = -> [Cr_element001]
  conduct = 2
  density = 1
  expand = 3
  formula = Cr
  name = G4_Cr
  specific = 4
FEATURE [App::DocumentObjectGroupPython] Mn_element001  label="Mn_element : 1"  # scripted group (container) (typed FeaturePython)
  n = 1
  ref = Mn_element
FEATURE [App::DocumentObjectGroupPython] G4_Mn  # scripted group (container) (typed FeaturePython)
  Dunit = g/cm3
  Dvalue = 7.44
  Group = -> [Mn_element001]
  conduct = 2
  density = 1
  expand = 3
  formula = Mn
  name = G4_Mn
  specific = 4
FEATURE [App::DocumentObjectGroupPython] Fe_element007  label="Fe_element : 004"  # scripted group (container) (typed FeaturePython)
  n = 1
  ref = Fe_element
FEATURE [App::DocumentObjectGroupPython] G4_Fe  # scripted group (container) (typed FeaturePython)
  Dunit = g/cm3
  Dvalue = 7.874
  Group = -> [Fe_element007]
  conduct = 2
  density = 1
  expand = 3
  formula = Fe
  name = G4_Fe
  specific = 4
FEATURE [App::DocumentObjectGroupPython] Co_element001  label="Co_element : 1"  # scripted group (container) (typed FeaturePython)
  n = 1
  ref = Co_element
FEATURE [App::DocumentObjectGroupPython] G4_Co  # scripted group (container) (typed FeaturePython)
  Dunit = g/cm3
  Dvalue = 8.9
  Group = -> [Co_element001]
  conduct = 2
  density = 1
  expand = 3
  formula = Co
  name = G4_Co
  specific = 4
FEATURE [App::DocumentObjectGroupPython] Ni_element001  label="Ni_element : 1"  # scripted group (container) (typed FeaturePython)
  n = 1
  ref = Ni_element
FEATURE [App::DocumentObjectGroupPython] G4_Ni  # scripted group (container) (typed FeaturePython)
  Dunit = g/cm3
  Dvalue = 8.902
  Group = -> [Ni_element001]
  conduct = 2
  density = 1
  expand = 3
  formula = Ni
  name = G4_Ni
  specific = 4
FEATURE [App::DocumentObjectGroupPython] Cu_element001  label="Cu_element : 1"  # scripted group (container) (typed FeaturePython)
  n = 1
  ref = Cu_element
FEATURE [App::DocumentObjectGroupPython] G4_Cu  # scripted group (container) (typed FeaturePython)
  Dunit = g/cm3
  Dvalue = 8.96
  Group = -> [Cu_element001]
  conduct = 2
  density = 1
  expand = 3
  formula = Cu
  name = G4_Cu
  specific = 4
FEATURE [App::DocumentObjectGroupPython] Zn_element001  label="Zn_element : 1"  # scripted group (container) (typed FeaturePython)
  n = 1
  ref = Zn_element
FEATURE [App::DocumentObjectGroupPython] G4_Zn  # scripted group (container) (typed FeaturePython)
  Dunit = g/cm3
  Dvalue = 7.133
  Group = -> [Zn_element001]
  conduct = 2
  density = 1
  expand = 3
  formula = Zn
  name = G4_Zn
  specific = 4
FEATURE [App::DocumentObjectGroupPython] Ga_element002  label="Ga_element : 002"  # scripted group (container) (typed FeaturePython)
  n = 1
  ref = Ga_element
FEATURE [App::DocumentObjectGroupPython] G4_Ga  # scripted group (container) (typed FeaturePython)
  Dunit = g/cm3
  Dvalue = 5.904
  Group = -> [Ga_element002]
  conduct = 2
  density = 1
  expand = 3
  formula = Ga
  name = G4_Ga
  specific = 4
FEATURE [App::DocumentObjectGroupPython] Ge_element002  label="Ge_element : 1"  # scripted group (container) (typed FeaturePython)
  n = 1
  ref = Ge_element
FEATURE [App::DocumentObjectGroupPython] G4_Ge  # scripted group (container) (typed FeaturePython)
  Dunit = g/cm3
  Dvalue = 5.323
  Group = -> [Ge_element002]
  conduct = 2
  density = 1
  expand = 3
  formula = Ge
  name = G4_Ge
  specific = 4
FEATURE [App::DocumentObjectGroupPython] As_element003  label="As_element : 002"  # scripted group (container) (typed FeaturePython)
  n = 1
  ref = As_element
FEATURE [App::DocumentObjectGroupPython] G4_As  # scripted group (container) (typed FeaturePython)
  Dunit = g/cm3
  Dvalue = 5.73
  Group = -> [As_element003]
  conduct = 2
  density = 1
  expand = 3
  formula = As
  name = G4_As
  specific = 4
FEATURE [App::DocumentObjectGroupPython] Se_element001  label="Se_element : 1"  # scripted group (container) (typed FeaturePython)
  n = 1
  ref = Se_element
FEATURE [App::DocumentObjectGroupPython] G4_Se  # scripted group (container) (typed FeaturePython)
  Dunit = g/cm3
  Dvalue = 4.5
  Group = -> [Se_element001]
  conduct = 2
  density = 1
  expand = 3
  formula = Se
  name = G4_Se
  specific = 4
FEATURE [App::DocumentObjectGroupPython] Br_element007  label="Br_element : 004"  # scripted group (container) (typed FeaturePython)
  n = 1
  ref = Br_element
FEATURE [App::DocumentObjectGroupPython] G4_Br  # scripted group (container) (typed FeaturePython)
  Dunit = g/cm3
  Dvalue = 0.0070721
  Group = -> [Br_element007]
  conduct = 2
  density = 1
  expand = 3
  formula = Br
  name = G4_Br
  specific = 4
FEATURE [App::DocumentObjectGroupPython] Kr_element001  label="Kr_element : 1"  # scripted group (container) (typed FeaturePython)
  n = 1
  ref = Kr_element
FEATURE [App::DocumentObjectGroupPython] G4_Kr  # scripted group (container) (typed FeaturePython)
  Dunit = g/cm3
  Dvalue = 0.00347832
  Group = -> [Kr_element001]
  conduct = 2
  density = 1
  expand = 3
  formula = Kr
  name = G4_Kr
  specific = 4
FEATURE [App::DocumentObjectGroupPython] Rb_element001  label="Rb_element : 1"  # scripted group (container) (typed FeaturePython)
  n = 1
  ref = Rb_element
FEATURE [App::DocumentObjectGroupPython] G4_Rb  # scripted group (container) (typed FeaturePython)
  Dunit = g/cm3
  Dvalue = 1.532
  Group = -> [Rb_element001]
  conduct = 2
  density = 1
  expand = 3
  formula = Rb
  name = G4_Rb
  specific = 4
FEATURE [App::DocumentObjectGroupPython] Sr_element001  label="Sr_element : 1"  # scripted group (container) (typed FeaturePython)
  n = 1
  ref = Sr_element
FEATURE [App::DocumentObjectGroupPython] G4_Sr  # scripted group (container) (typed FeaturePython)
  Dunit = g/cm3
  Dvalue = 2.54
  Group = -> [Sr_element001]
  conduct = 2
  density = 1
  expand = 3
  formula = Sr
  name = G4_Sr
  specific = 4
FEATURE [App::DocumentObjectGroupPython] Y_element001  label="Y_element : 1"  # scripted group (container) (typed FeaturePython)
  n = 1
  ref = Y_element
FEATURE [App::DocumentObjectGroupPython] G4_Y  # scripted group (container) (typed FeaturePython)
  Dunit = g/cm3
  Dvalue = 4.469
  Group = -> [Y_element001]
  conduct = 2
  density = 1
  expand = 3
  formula = Y
  name = G4_Y
  specific = 4
FEATURE [App::DocumentObjectGroupPython] Zr_element001  label="Zr_element : 1"  # scripted group (container) (typed FeaturePython)
  n = 1
  ref = Zr_element
FEATURE [App::DocumentObjectGroupPython] G4_Zr  # scripted group (container) (typed FeaturePython)
  Dunit = g/cm3
  Dvalue = 6.506
  Group = -> [Zr_element001]
  conduct = 2
  density = 1
  expand = 3
  formula = Zr
  name = G4_Zr
  specific = 4
FEATURE [App::DocumentObjectGroupPython] Nb_element001  label="Nb_element : 1"  # scripted group (container) (typed FeaturePython)
  n = 1
  ref = Nb_element
FEATURE [App::DocumentObjectGroupPython] G4_Nb  # scripted group (container) (typed FeaturePython)
  Dunit = g/cm3
  Dvalue = 8.57
  Group = -> [Nb_element001]
  conduct = 2
  density = 1
  expand = 3
  formula = Nb
  name = G4_Nb
  specific = 4
FEATURE [App::DocumentObjectGroupPython] Mo_element001  label="Mo_element : 1"  # scripted group (container) (typed FeaturePython)
  n = 1
  ref = Mo_element
FEATURE [App::DocumentObjectGroupPython] G4_Mo  # scripted group (container) (typed FeaturePython)
  Dunit = g/cm3
  Dvalue = 10.22
  Group = -> [Mo_element001]
  conduct = 2
  density = 1
  expand = 3
  formula = Mo
  name = G4_Mo
  specific = 4
FEATURE [App::DocumentObjectGroupPython] Tc_element001  label="Tc_element : 1"  # scripted group (container) (typed FeaturePython)
  n = 1
  ref = Tc_element
FEATURE [App::DocumentObjectGroupPython] G4_Tc  # scripted group (container) (typed FeaturePython)
  Dunit = g/cm3
  Dvalue = 11.5
  Group = -> [Tc_element001]
  conduct = 2
  density = 1
  expand = 3
  formula = Tc
  name = G4_Tc
  specific = 4
FEATURE [App::DocumentObjectGroupPython] Ru_element001  label="Ru_element : 1"  # scripted group (container) (typed FeaturePython)
  n = 1
  ref = Ru_element
FEATURE [App::DocumentObjectGroupPython] G4_Ru  # scripted group (container) (typed FeaturePython)
  Dunit = g/cm3
  Dvalue = 12.41
  Group = -> [Ru_element001]
  conduct = 2
  density = 1
  expand = 3
  formula = Ru
  name = G4_Ru
  specific = 4
FEATURE [App::DocumentObjectGroupPython] Rh_element001  label="Rh_element : 1"  # scripted group (container) (typed FeaturePython)
  n = 1
  ref = Rh_element
FEATURE [App::DocumentObjectGroupPython] G4_Rh  # scripted group (container) (typed FeaturePython)
  Dunit = g/cm3
  Dvalue = 12.41
  Group = -> [Rh_element001]
  conduct = 2
  density = 1
  expand = 3
  formula = Rh
  name = G4_Rh
  specific = 4
FEATURE [App::DocumentObjectGroupPython] Pd_element001  label="Pd_element : 1"  # scripted group (container) (typed FeaturePython)
  n = 1
  ref = Pd_element
FEATURE [App::DocumentObjectGroupPython] G4_Pd  # scripted group (container) (typed FeaturePython)
  Dunit = g/cm3
  Dvalue = 12.02
  Group = -> [Pd_element001]
  conduct = 2
  density = 1
  expand = 3
  formula = Pd
  name = G4_Pd
  specific = 4
FEATURE [App::DocumentObjectGroupPython] Ag_element006  label="Ag_element : 004"  # scripted group (container) (typed FeaturePython)
  n = 1
  ref = Ag_element
FEATURE [App::DocumentObjectGroupPython] G4_Ag  # scripted group (container) (typed FeaturePython)
  Dunit = g/cm3
  Dvalue = 10.5
  Group = -> [Ag_element006]
  conduct = 2
  density = 1
  expand = 3
  formula = Ag
  name = G4_Ag
  specific = 4
FEATURE [App::DocumentObjectGroupPython] Cd_element003  label="Cd_element : 003"  # scripted group (container) (typed FeaturePython)
  n = 1
  ref = Cd_element
FEATURE [App::DocumentObjectGroupPython] G4_Cd  # scripted group (container) (typed FeaturePython)
  Dunit = g/cm3
  Dvalue = 8.65
  Group = -> [Cd_element003]
  conduct = 2
  density = 1
  expand = 3
  formula = Cd
  name = G4_Cd
  specific = 4
FEATURE [App::DocumentObjectGroupPython] In_element001  label="In_element : 1"  # scripted group (container) (typed FeaturePython)
  n = 1
  ref = In_element
FEATURE [App::DocumentObjectGroupPython] G4_In  # scripted group (container) (typed FeaturePython)
  Dunit = g/cm3
  Dvalue = 7.31
  Group = -> [In_element001]
  conduct = 2
  density = 1
  expand = 3
  formula = In
  name = G4_In
  specific = 4
FEATURE [App::DocumentObjectGroupPython] Sn_element001  label="Sn_element : 1"  # scripted group (container) (typed FeaturePython)
  n = 1
  ref = Sn_element
FEATURE [App::DocumentObjectGroupPython] G4_Sn  # scripted group (container) (typed FeaturePython)
  Dunit = g/cm3
  Dvalue = 7.31
  Group = -> [Sn_element001]
  conduct = 2
  density = 1
  expand = 3
  formula = Sn
  name = G4_Sn
  specific = 4
FEATURE [App::DocumentObjectGroupPython] Sb_element001  label="Sb_element : 1"  # scripted group (container) (typed FeaturePython)
  n = 1
  ref = Sb_element
FEATURE [App::DocumentObjectGroupPython] G4_Sb  # scripted group (container) (typed FeaturePython)
  Dunit = g/cm3
  Dvalue = 6.691
  Group = -> [Sb_element001]
  conduct = 2
  density = 1
  expand = 3
  formula = Sb
  name = G4_Sb
  specific = 4
FEATURE [App::DocumentObjectGroupPython] Te_element002  label="Te_element : 002"  # scripted group (container) (typed FeaturePython)
  n = 1
  ref = Te_element
FEATURE [App::DocumentObjectGroupPython] G4_Te  # scripted group (container) (typed FeaturePython)
  Dunit = g/cm3
  Dvalue = 6.24
  Group = -> [Te_element002]
  conduct = 2
  density = 1
  expand = 3
  formula = Te
  name = G4_Te
  specific = 4
FEATURE [App::DocumentObjectGroupPython] I_element010  label="I_element : 006"  # scripted group (container) (typed FeaturePython)
  n = 1
  ref = I_element
FEATURE [App::DocumentObjectGroupPython] G4_I  # scripted group (container) (typed FeaturePython)
  Dunit = g/cm3
  Dvalue = 4.93
  Group = -> [I_element010]
  conduct = 2
  density = 1
  expand = 3
  formula = I
  name = G4_I
  specific = 4
FEATURE [App::DocumentObjectGroupPython] Xe_element001  label="Xe_element : 1"  # scripted group (container) (typed FeaturePython)
  n = 1
  ref = Xe_element
FEATURE [App::DocumentObjectGroupPython] G4_Xe  # scripted group (container) (typed FeaturePython)
  Dunit = g/cm3
  Dvalue = 0.00548536
  Group = -> [Xe_element001]
  conduct = 2
  density = 1
  expand = 3
  formula = Xe
  name = G4_Xe
  specific = 4
FEATURE [App::DocumentObjectGroupPython] Cs_element003  label="Cs_element : 003"  # scripted group (container) (typed FeaturePython)
  n = 1
  ref = Cs_element
FEATURE [App::DocumentObjectGroupPython] G4_Cs  # scripted group (container) (typed FeaturePython)
  Dunit = g/cm3
  Dvalue = 1.873
  Group = -> [Cs_element003]
  conduct = 2
  density = 1
  expand = 3
  formula = Cs
  name = G4_Cs
  specific = 4
FEATURE [App::DocumentObjectGroupPython] Ba_element003  label="Ba_element : 003"  # scripted group (container) (typed FeaturePython)
  n = 1
  ref = Ba_element
FEATURE [App::DocumentObjectGroupPython] G4_Ba  # scripted group (container) (typed FeaturePython)
  Dunit = g/cm3
  Dvalue = 3.5
  Group = -> [Ba_element003]
  conduct = 2
  density = 1
  expand = 3
  formula = Ba
  name = G4_Ba
  specific = 4
FEATURE [App::DocumentObjectGroupPython] La_element003  label="La_element : 003"  # scripted group (container) (typed FeaturePython)
  n = 1
  ref = La_element
FEATURE [App::DocumentObjectGroupPython] G4_La  # scripted group (container) (typed FeaturePython)
  Dunit = g/cm3
  Dvalue = 6.154
  Group = -> [La_element003]
  conduct = 2
  density = 1
  expand = 3
  formula = La
  name = G4_La
  specific = 4
FEATURE [App::DocumentObjectGroupPython] Ce_element002  label="Ce_element : 1"  # scripted group (container) (typed FeaturePython)
  n = 1
  ref = Ce_element
FEATURE [App::DocumentObjectGroupPython] G4_Ce  # scripted group (container) (typed FeaturePython)
  Dunit = g/cm3
  Dvalue = 6.657
  Group = -> [Ce_element002]
  conduct = 2
  density = 1
  expand = 3
  formula = Ce
  name = G4_Ce
  specific = 4
FEATURE [App::DocumentObjectGroupPython] Pr_element001  label="Pr_element : 1"  # scripted group (container) (typed FeaturePython)
  n = 1
  ref = Pr_element
FEATURE [App::DocumentObjectGroupPython] G4_Pr  # scripted group (container) (typed FeaturePython)
  Dunit = g/cm3
  Dvalue = 6.71
  Group = -> [Pr_element001]
  conduct = 2
  density = 1
  expand = 3
  formula = Pr
  name = G4_Pr
  specific = 4
FEATURE [App::DocumentObjectGroupPython] Nd_element001  label="Nd_element : 1"  # scripted group (container) (typed FeaturePython)
  n = 1
  ref = Nd_element
FEATURE [App::DocumentObjectGroupPython] G4_Nd  # scripted group (container) (typed FeaturePython)
  Dunit = g/cm3
  Dvalue = 6.9
  Group = -> [Nd_element001]
  conduct = 2
  density = 1
  expand = 3
  formula = Nd
  name = G4_Nd
  specific = 4
FEATURE [App::DocumentObjectGroupPython] Pm_element001  label="Pm_element : 1"  # scripted group (container) (typed FeaturePython)
  n = 1
  ref = Pm_element
FEATURE [App::DocumentObjectGroupPython] G4_Pm  # scripted group (container) (typed FeaturePython)
  Dunit = g/cm3
  Dvalue = 7.22
  Group = -> [Pm_element001]
  conduct = 2
  density = 1
  expand = 3
  formula = Pm
  name = G4_Pm
  specific = 4
FEATURE [App::DocumentObjectGroupPython] Sm_element001  label="Sm_element : 1"  # scripted group (container) (typed FeaturePython)
  n = 1
  ref = Sm_element
FEATURE [App::DocumentObjectGroupPython] G4_Sm  # scripted group (container) (typed FeaturePython)
  Dunit = g/cm3
  Dvalue = 7.46
  Group = -> [Sm_element001]
  conduct = 2
  density = 1
  expand = 3
  formula = Sm
  name = G4_Sm
  specific = 4
FEATURE [App::DocumentObjectGroupPython] Eu_element001  label="Eu_element : 1"  # scripted group (container) (typed FeaturePython)
  n = 1
  ref = Eu_element
FEATURE [App::DocumentObjectGroupPython] G4_Eu  # scripted group (container) (typed FeaturePython)
  Dunit = g/cm3
  Dvalue = 5.243
  Group = -> [Eu_element001]
  conduct = 2
  density = 1
  expand = 3
  formula = Eu
  name = G4_Eu
  specific = 4
FEATURE [App::DocumentObjectGroupPython] Gd_element002  label="Gd_element : 1"  # scripted group (container) (typed FeaturePython)
  n = 1
  ref = Gd_element
FEATURE [App::DocumentObjectGroupPython] G4_Gd  # scripted group (container) (typed FeaturePython)
  Dunit = g/cm3
  Dvalue = 7.9004
  Group = -> [Gd_element002]
  conduct = 2
  density = 1
  expand = 3
  formula = Gd
  name = G4_Gd
  specific = 4
FEATURE [App::DocumentObjectGroupPython] Tb_element001  label="Tb_element : 1"  # scripted group (container) (typed FeaturePython)
  n = 1
  ref = Tb_element
FEATURE [App::DocumentObjectGroupPython] G4_Tb  # scripted group (container) (typed FeaturePython)
  Dunit = g/cm3
  Dvalue = 8.229
  Group = -> [Tb_element001]
  conduct = 2
  density = 1
  expand = 3
  formula = Tb
  name = G4_Tb
  specific = 4
FEATURE [App::DocumentObjectGroupPython] Dy_element001  label="Dy_element : 1"  # scripted group (container) (typed FeaturePython)
  n = 1
  ref = Dy_element
FEATURE [App::DocumentObjectGroupPython] G4_Dy  # scripted group (container) (typed FeaturePython)
  Dunit = g/cm3
  Dvalue = 8.55
  Group = -> [Dy_element001]
  conduct = 2
  density = 1
  expand = 3
  formula = Dy
  name = G4_Dy
  specific = 4
FEATURE [App::DocumentObjectGroupPython] Ho_element001  label="Ho_element : 1"  # scripted group (container) (typed FeaturePython)
  n = 1
  ref = Ho_element
FEATURE [App::DocumentObjectGroupPython] G4_Ho  # scripted group (container) (typed FeaturePython)
  Dunit = g/cm3
  Dvalue = 8.795
  Group = -> [Ho_element001]
  conduct = 2
  density = 1
  expand = 3
  formula = Ho
  name = G4_Ho
  specific = 4
FEATURE [App::DocumentObjectGroupPython] Er_element001  label="Er_element : 1"  # scripted group (container) (typed FeaturePython)
  n = 1
  ref = Er_element
FEATURE [App::DocumentObjectGroupPython] G4_Er  # scripted group (container) (typed FeaturePython)
  Dunit = g/cm3
  Dvalue = 9.066
  Group = -> [Er_element001]
  conduct = 2
  density = 1
  expand = 3
  formula = Er
  name = G4_Er
  specific = 4
FEATURE [App::DocumentObjectGroupPython] Tm_element001  label="Tm_element : 1"  # scripted group (container) (typed FeaturePython)
  n = 1
  ref = Tm_element
FEATURE [App::DocumentObjectGroupPython] G4_Tm  # scripted group (container) (typed FeaturePython)
  Dunit = g/cm3
  Dvalue = 9.321
  Group = -> [Tm_element001]
  conduct = 2
  density = 1
  expand = 3
  formula = Tm
  name = G4_Tm
  specific = 4
FEATURE [App::DocumentObjectGroupPython] Yb_element001  label="Yb_element : 1"  # scripted group (container) (typed FeaturePython)
  n = 1
  ref = Yb_element
FEATURE [App::DocumentObjectGroupPython] G4_Yb  # scripted group (container) (typed FeaturePython)
  Dunit = g/cm3
  Dvalue = 6.73
  Group = -> [Yb_element001]
  conduct = 2
  density = 1
  expand = 3
  formula = Yb
  name = G4_Yb
  specific = 4
FEATURE [App::DocumentObjectGroupPython] Lu_element001  label="Lu_element : 1"  # scripted group (container) (typed FeaturePython)
  n = 1
  ref = Lu_element
FEATURE [App::DocumentObjectGroupPython] G4_Lu  # scripted group (container) (typed FeaturePython)
  Dunit = g/cm3
  Dvalue = 9.84
  Group = -> [Lu_element001]
  conduct = 2
  density = 1
  expand = 3
  formula = Lu
  name = G4_Lu
  specific = 4
FEATURE [App::DocumentObjectGroupPython] Hf_element001  label="Hf_element : 1"  # scripted group (container) (typed FeaturePython)
  n = 1
  ref = Hf_element
FEATURE [App::DocumentObjectGroupPython] G4_Hf  # scripted group (container) (typed FeaturePython)
  Dunit = g/cm3
  Dvalue = 13.31
  Group = -> [Hf_element001]
  conduct = 2
  density = 1
  expand = 3
  formula = Hf
  name = G4_Hf
  specific = 4
FEATURE [App::DocumentObjectGroupPython] Ta_element001  label="Ta_element : 1"  # scripted group (container) (typed FeaturePython)
  n = 1
  ref = Ta_element
FEATURE [App::DocumentObjectGroupPython] G4_Ta  # scripted group (container) (typed FeaturePython)
  Dunit = g/cm3
  Dvalue = 16.654
  Group = -> [Ta_element001]
  conduct = 2
  density = 1
  expand = 3
  formula = Ta
  name = G4_Ta
  specific = 4
FEATURE [App::DocumentObjectGroupPython] W_element004  label="W_element : 004"  # scripted group (container) (typed FeaturePython)
  n = 1
  ref = W_element
FEATURE [App::DocumentObjectGroupPython] G4_W  # scripted group (container) (typed FeaturePython)
  Dunit = g/cm3
  Dvalue = 19.3
  Group = -> [W_element004]
  conduct = 2
  density = 1
  expand = 3
  formula = W
  name = G4_W
  specific = 4
FEATURE [App::DocumentObjectGroupPython] Re_element001  label="Re_element : 1"  # scripted group (container) (typed FeaturePython)
  n = 1
  ref = Re_element
FEATURE [App::DocumentObjectGroupPython] G4_Re  # scripted group (container) (typed FeaturePython)
  Dunit = g/cm3
  Dvalue = 21.02
  Group = -> [Re_element001]
  conduct = 2
  density = 1
  expand = 3
  formula = Re
  name = G4_Re
  specific = 4
FEATURE [App::DocumentObjectGroupPython] Os_element001  label="Os_element : 1"  # scripted group (container) (typed FeaturePython)
  n = 1
  ref = Os_element
FEATURE [App::DocumentObjectGroupPython] G4_Os  # scripted group (container) (typed FeaturePython)
  Dunit = g/cm3
  Dvalue = 22.57
  Group = -> [Os_element001]
  conduct = 2
  density = 1
  expand = 3
  formula = Os
  name = G4_Os
  specific = 4
FEATURE [App::DocumentObjectGroupPython] Ir_element001  label="Ir_element : 1"  # scripted group (container) (typed FeaturePython)
  n = 1
  ref = Ir_element
FEATURE [App::DocumentObjectGroupPython] G4_Ir  # scripted group (container) (typed FeaturePython)
  Dunit = g/cm3
  Dvalue = 22.42
  Group = -> [Ir_element001]
  conduct = 2
  density = 1
  expand = 3
  formula = Ir
  name = G4_Ir
  specific = 4
FEATURE [App::DocumentObjectGroupPython] Pt_element001  label="Pt_element : 1"  # scripted group (container) (typed FeaturePython)
  n = 1
  ref = Pt_element
FEATURE [App::DocumentObjectGroupPython] G4_Pt  # scripted group (container) (typed FeaturePython)
  Dunit = g/cm3
  Dvalue = 21.45
  Group = -> [Pt_element001]
  conduct = 2
  density = 1
  expand = 3
  formula = Pt
  name = G4_Pt
  specific = 4
FEATURE [App::DocumentObjectGroupPython] Au_element001  label="Au_element : 1"  # scripted group (container) (typed FeaturePython)
  n = 1
  ref = Au_element
FEATURE [App::DocumentObjectGroupPython] G4_Au  # scripted group (container) (typed FeaturePython)
  Dunit = g/cm3
  Dvalue = 19.32
  Group = -> [Au_element001]
  conduct = 2
  density = 1
  expand = 3
  formula = Au
  name = G4_Au
  specific = 4
FEATURE [App::DocumentObjectGroupPython] Hg_element002  label="Hg_element : 002"  # scripted group (container) (typed FeaturePython)
  n = 1
  ref = Hg_element
FEATURE [App::DocumentObjectGroupPython] G4_Hg  # scripted group (container) (typed FeaturePython)
  Dunit = g/cm3
  Dvalue = 13.546
  Group = -> [Hg_element002]
  conduct = 2
  density = 1
  expand = 3
  formula = Hg
  name = G4_Hg
  specific = 4
FEATURE [App::DocumentObjectGroupPython] Tl_element002  label="Tl_element : 002"  # scripted group (container) (typed FeaturePython)
  n = 1
  ref = Tl_element
FEATURE [App::DocumentObjectGroupPython] G4_Tl  # scripted group (container) (typed FeaturePython)
  Dunit = g/cm3
  Dvalue = 11.72
  Group = -> [Tl_element002]
  conduct = 2
  density = 1
  expand = 3
  formula = Tl
  name = G4_Tl
  specific = 4
FEATURE [App::DocumentObjectGroupPython] Pb_element003  label="Pb_element : 1"  # scripted group (container) (typed FeaturePython)
  n = 1
  ref = Pb_element
FEATURE [App::DocumentObjectGroupPython] G4_Pb  # scripted group (container) (typed FeaturePython)
  Dunit = g/cm3
  Dvalue = 11.35
  Group = -> [Pb_element003]
  conduct = 2
  density = 1
  expand = 3
  formula = Pb
  name = G4_Pb
  specific = 4
FEATURE [App::DocumentObjectGroupPython] Bi_element002  label="Bi_element : 1"  # scripted group (container) (typed FeaturePython)
  n = 1
  ref = Bi_element
FEATURE [App::DocumentObjectGroupPython] G4_Bi  # scripted group (container) (typed FeaturePython)
  Dunit = g/cm3
  Dvalue = 9.747
  Group = -> [Bi_element002]
  conduct = 2
  density = 1
  expand = 3
  formula = Bi
  name = G4_Bi
  specific = 4
FEATURE [App::DocumentObjectGroupPython] Po_element001  label="Po_element : 1"  # scripted group (container) (typed FeaturePython)
  n = 1
  ref = Po_element
FEATURE [App::DocumentObjectGroupPython] G4_Po  # scripted group (container) (typed FeaturePython)
  Dunit = g/cm3
  Dvalue = 9.32
  Group = -> [Po_element001]
  conduct = 2
  density = 1
  expand = 3
  formula = Po
  name = G4_Po
  specific = 4
FEATURE [App::DocumentObjectGroupPython] At_element001  label="At_element : 1"  # scripted group (container) (typed FeaturePython)
  n = 1
  ref = At_element
FEATURE [App::DocumentObjectGroupPython] G4_At  # scripted group (container) (typed FeaturePython)
  Dunit = g/cm3
  Dvalue = 9.32
  Group = -> [At_element001]
  conduct = 2
  density = 1
  expand = 3
  formula = At
  name = G4_At
  specific = 4
FEATURE [App::DocumentObjectGroupPython] Rn_element001  label="Rn_element : 1"  # scripted group (container) (typed FeaturePython)
  n = 1
  ref = Rn_element
FEATURE [App::DocumentObjectGroupPython] G4_Rn  # scripted group (container) (typed FeaturePython)
  Dunit = g/cm3
  Dvalue = 0.00900662
  Group = -> [Rn_element001]
  conduct = 2
  density = 1
  expand = 3
  formula = Rn
  name = G4_Rn
  specific = 4
FEATURE [App::DocumentObjectGroupPython] Fr_element001  label="Fr_element : 1"  # scripted group (container) (typed FeaturePython)
  n = 1
  ref = Fr_element
FEATURE [App::DocumentObjectGroupPython] G4_Fr  # scripted group (container) (typed FeaturePython)
  Dunit = g/cm3
  Dvalue = 1
  Group = -> [Fr_element001]
  conduct = 2
  density = 1
  expand = 3
  formula = Fr
  name = G4_Fr
  specific = 4
FEATURE [App::DocumentObjectGroupPython] Ra_element001  label="Ra_element : 1"  # scripted group (container) (typed FeaturePython)
  n = 1
  ref = Ra_element
FEATURE [App::DocumentObjectGroupPython] G4_Ra  # scripted group (container) (typed FeaturePython)
  Dunit = g/cm3
  Dvalue = 5
  Group = -> [Ra_element001]
  conduct = 2
  density = 1
  expand = 3
  formula = Ra
  name = G4_Ra
  specific = 4
FEATURE [App::DocumentObjectGroupPython] Ac_element001  label="Ac_element : 1"  # scripted group (container) (typed FeaturePython)
  n = 1
  ref = Ac_element
FEATURE [App::DocumentObjectGroupPython] G4_Ac  # scripted group (container) (typed FeaturePython)
  Dunit = g/cm3
  Dvalue = 10.07
  Group = -> [Ac_element001]
  conduct = 2
  density = 1
  expand = 3
  formula = Ac
  name = G4_Ac
  specific = 4
FEATURE [App::DocumentObjectGroupPython] Th_element001  label="Th_element : 1"  # scripted group (container) (typed FeaturePython)
  n = 1
  ref = Th_element
FEATURE [App::DocumentObjectGroupPython] G4_Th  # scripted group (container) (typed FeaturePython)
  Dunit = g/cm3
  Dvalue = 11.72
  Group = -> [Th_element001]
  conduct = 2
  density = 1
  expand = 3
  formula = Th
  name = G4_Th
  specific = 4
FEATURE [App::DocumentObjectGroupPython] Pa_element001  label="Pa_element : 1"  # scripted group (container) (typed FeaturePython)
  n = 1
  ref = Pa_element
FEATURE [App::DocumentObjectGroupPython] G4_Pa  # scripted group (container) (typed FeaturePython)
  Dunit = g/cm3
  Dvalue = 15.37
  Group = -> [Pa_element001]
  conduct = 2
  density = 1
  expand = 3
  formula = Pa
  name = G4_Pa
  specific = 4
FEATURE [App::DocumentObjectGroupPython] U_element004  label="U_element : 004"  # scripted group (container) (typed FeaturePython)
  n = 1
  ref = U_element
FEATURE [App::DocumentObjectGroupPython] G4_U  # scripted group (container) (typed FeaturePython)
  Dunit = g/cm3
  Dvalue = 18.95
  Group = -> [U_element004]
  conduct = 2
  density = 1
  expand = 3
  formula = U
  name = G4_U
  specific = 4
FEATURE [App::DocumentObjectGroupPython] Np_element001  label="Np_element : 1"  # scripted group (container) (typed FeaturePython)
  n = 1
  ref = Np_element
FEATURE [App::DocumentObjectGroupPython] G4_Np  # scripted group (container) (typed FeaturePython)
  Dunit = g/cm3
  Dvalue = 20.25
  Group = -> [Np_element001]
  conduct = 2
  density = 1
  expand = 3
  formula = Np
  name = G4_Np
  specific = 4
FEATURE [App::DocumentObjectGroupPython] Pu_element002  label="Pu_element : 002"  # scripted group (container) (typed FeaturePython)
  n = 1
  ref = Pu_element
FEATURE [App::DocumentObjectGroupPython] G4_Pu  # scripted group (container) (typed FeaturePython)
  Dunit = g/cm3
  Dvalue = 19.84
  Group = -> [Pu_element002]
  conduct = 2
  density = 1
  expand = 3
  formula = Pu
  name = G4_Pu
  specific = 4
FEATURE [App::DocumentObjectGroupPython] Am_element001  label="Am_element : 1"  # scripted group (container) (typed FeaturePython)
  n = 1
  ref = Am_element
FEATURE [App::DocumentObjectGroupPython] G4_Am  # scripted group (container) (typed FeaturePython)
  Dunit = g/cm3
  Dvalue = 13.67
  Group = -> [Am_element001]
  conduct = 2
  density = 1
  expand = 3
  formula = Am
  name = G4_Am
  specific = 4
FEATURE [App::DocumentObjectGroupPython] Cm_element001  label="Cm_element : 1"  # scripted group (container) (typed FeaturePython)
  n = 1
  ref = Cm_element
FEATURE [App::DocumentObjectGroupPython] G4_Cm  # scripted group (container) (typed FeaturePython)
  Dunit = g/cm3
  Dvalue = 13.51
  Group = -> [Cm_element001]
  conduct = 2
  density = 1
  expand = 3
  formula = Cm
  name = G4_Cm
  specific = 4
FEATURE [App::DocumentObjectGroupPython] Bk_element001  label="Bk_element : 1"  # scripted group (container) (typed FeaturePython)
  n = 1
  ref = Bk_element
FEATURE [App::DocumentObjectGroupPython] G4_Bk  # scripted group (container) (typed FeaturePython)
  Dunit = g/cm3
  Dvalue = 14
  Group = -> [Bk_element001]
  conduct = 2
  density = 1
  expand = 3
  formula = Bk
  name = G4_Bk
  specific = 4
FEATURE [App::DocumentObjectGroupPython] Cf_element001  label="Cf_element : 1"  # scripted group (container) (typed FeaturePython)
  n = 1
  ref = Cf_element
FEATURE [App::DocumentObjectGroupPython] G4_Cf  # scripted group (container) (typed FeaturePython)
  Dunit = g/cm3
  Dvalue = 10
  Group = -> [Cf_element001]
  conduct = 2
  density = 1
  expand = 3
  formula = Cf
  name = G4_Cf
  specific = 4
FEATURE [App::DocumentObjectGroupPython] Element  # scripted group (container) (typed FeaturePython)
  Group = -> [G4_H,G4_He,G4_Li,G4_Be,G4_B,G4_C,G4_N,G4_O,G4_F,G4_Ne,G4_Na,G4_Mg,G4_Al,G4_Si,G4_P,G4_S,G4_Cl,G4_Ar,G4_K,G4_Ca,G4_Sc,G4_Ti,G4_V,G4_Cr,G4_Mn,G4_Fe,G4_Co,G4_Ni,G4_Cu,G4_Zn,G4_Ga,G4_Ge,G4_As,G4_Se,G4_Br,G4_Kr,G4_Rb,G4_Sr,G4_Y,G4_Zr,G4_Nb,G4_Mo,G4_Tc,G4_Ru,G4_Rh,G4_Pd,G4_Ag,G4_Cd,G4_In,G4_Sn,G4_Sb,G4_Te,G4_I,G4_Xe,G4_Cs,G4_Ba,G4_La,G4_Ce,G4_Pr,G4_Nd,G4_Pm,G4_Sm,G4_Eu,G4_Gd,G4_Tb,G4_Dy,G4_Ho,G4_Er,+30 more]
FEATURE [App::DocumentObjectGroupPython] H_element114  label="H_element : 063"  # scripted group (container) (typed FeaturePython)
  n = 2
  ref = H_element
FEATURE [App::DocumentObjectGroupPython] G4_lH2  # scripted group (container) (typed FeaturePython)
  Dunit = g/cm3
  Dvalue = 0.0708
  Group = -> [H_element114]
  conduct = 2
  density = 1
  expand = 3
  formula = G4_lH2
  name = G4_lH2
  specific = 4
FEATURE [App::DocumentObjectGroupPython] N_element049  label="N_element : 022"  # scripted group (container) (typed FeaturePython)
  n = 2
  ref = N_element
FEATURE [App::DocumentObjectGroupPython] G4_lN2  # scripted group (container) (typed FeaturePython)
  Dunit = g/cm3
  Dvalue = 0.807
  Group = -> [N_element049]
  conduct = 2
  density = 1
  expand = 3
  formula = G4_lN2
  name = G4_lN2
  specific = 4
FEATURE [App::DocumentObjectGroupPython] O_element106  label="O_element : 060"  # scripted group (container) (typed FeaturePython)
  n = 2
  ref = O_element
FEATURE [App::DocumentObjectGroupPython] G4_lO2  # scripted group (container) (typed FeaturePython)
  Dunit = g/cm3
  Dvalue = 1.141
  Group = -> [O_element106]
  conduct = 2
  density = 1
  expand = 3
  formula = G4_lO2
  name = G4_lO2
  specific = 4
FEATURE [App::DocumentObjectGroupPython] Ar  label="Ar : 1"  # scripted group (container) (typed FeaturePython)
  n = 1
  ref = Ar
FEATURE [App::DocumentObjectGroupPython] G4_lAr  # scripted group (container) (typed FeaturePython)
  Dunit = g/cm3
  Dvalue = 1.396
  Group = -> [Ar]
  conduct = 2
  density = 1
  expand = 3
  formula = G4_lAr
  name = G4_lAr
  specific = 4
FEATURE [App::DocumentObjectGroupPython] Br  label="Br : 1"  # scripted group (container) (typed FeaturePython)
  n = 1
  ref = Br
FEATURE [App::DocumentObjectGroupPython] G4_lBr  # scripted group (container) (typed FeaturePython)
  Dunit = g/cm3
  Dvalue = 3.1028
  Group = -> [Br]
  conduct = 2
  density = 1
  expand = 3
  formula = G4_lBr
  name = G4_lBr
  specific = 4
FEATURE [App::DocumentObjectGroupPython] Kr  label="Kr : 1"  # scripted group (container) (typed FeaturePython)
  n = 1
  ref = Kr
FEATURE [App::DocumentObjectGroupPython] G4_lKr  # scripted group (container) (typed FeaturePython)
  Dunit = g/cm3
  Dvalue = 2.418
  Group = -> [Kr]
  conduct = 2
  density = 1
  expand = 3
  formula = G4_lKr
  name = G4_lKr
  specific = 4
FEATURE [App::DocumentObjectGroupPython] Xe  label="Xe : 1"  # scripted group (container) (typed FeaturePython)
  n = 1
  ref = Xe
FEATURE [App::DocumentObjectGroupPython] G4_lXe  # scripted group (container) (typed FeaturePython)
  Dunit = g/cm3
  Dvalue = 2.953
  Group = -> [Xe]
  conduct = 2
  density = 1
  expand = 3
  formula = G4_lXe
  name = G4_lXe
  specific = 4
FEATURE [App::DocumentObjectGroupPython] O_element107  label="O_element : 061"  # scripted group (container) (typed FeaturePython)
  n = 4
  ref = O_element
FEATURE [App::DocumentObjectGroupPython] Pb_element004  label="Pb_element : 002"  # scripted group (container) (typed FeaturePython)
  n = 1
  ref = Pb_element
FEATURE [App::DocumentObjectGroupPython] W_element005  label="W_element : 005"  # scripted group (container) (typed FeaturePython)
  n = 1
  ref = W_element
FEATURE [App::DocumentObjectGroupPython] G4_PbWO4  # scripted group (container) (typed FeaturePython)
  Dunit = g/cm3
  Dvalue = 8.28
  Group = -> [O_element107,Pb_element004,W_element005]
  conduct = 2
  density = 1
  expand = 3
  formula = G4_PbWO4
  name = G4_PbWO4
  specific = 4
FEATURE [App::DocumentObjectGroupPython] alactic  label="alactic : 1"  # scripted group (container) (typed FeaturePython)
  n = 1
  ref = alactic
FEATURE [App::DocumentObjectGroupPython] G4_Galactic  # scripted group (container) (typed FeaturePython)
  Dunit = g/cm3
  Dvalue = 0
  Group = -> [alactic]
  conduct = 2
  density = 1
  expand = 3
  formula = G4_Galactic
  name = G4_Galactic
  specific = 4
FEATURE [App::DocumentObjectGroupPython] RAPHITE_POROUS  label="RAPHITE_POROUS : 1"  # scripted group (container) (typed FeaturePython)
  n = 1
  ref = RAPHITE_POROUS
FEATURE [App::DocumentObjectGroupPython] G4_GRAPHITE_POROUS  # scripted group (container) (typed FeaturePython)
  Dunit = g/cm3
  Dvalue = 1.7
  Group = -> [RAPHITE_POROUS]
  conduct = 2
  density = 1
  expand = 3
  formula = G4_GRAPHITE_POROUS
  name = G4_GRAPHITE_POROUS
  specific = 4
FEATURE [App::DocumentObjectGroupPython] H_element115  label="H_element : 0.150"  # scripted group (container) (typed FeaturePython)
  n = 0.080538
FEATURE [App::DocumentObjectGroupPython] C_element125  label="C_element : 0.600"  # scripted group (container) (typed FeaturePython)
  n = 0.599848
FEATURE [App::DocumentObjectGroupPython] O_element108  label="O_element : 0.320"  # scripted group (container) (typed FeaturePython)
  n = 0.319614
FEATURE [App::DocumentObjectGroupPython] G4_LUCITE  # scripted group (container) (typed FeaturePython)
  Dunit = g/cm3
  Dvalue = 1.19
  Group = -> [H_element115,C_element125,O_element108]
  conduct = 2
  density = 1
  expand = 3
  formula = G4_LUCITE
  name = G4_LUCITE
  specific = 4
FEATURE [App::DocumentObjectGroupPython] Cu_element002  label="Cu_element : 62"  # scripted group (container) (typed FeaturePython)
  n = 62
  ref = Cu_element
FEATURE [App::DocumentObjectGroupPython] Zn_element002  label="Zn_element : 35"  # scripted group (container) (typed FeaturePython)
  n = 35
  ref = Zn_element
FEATURE [App::DocumentObjectGroupPython] Pb_element005  label="Pb_element : 3"  # scripted group (container) (typed FeaturePython)
  n = 3
  ref = Pb_element
FEATURE [App::DocumentObjectGroupPython] G4_BRASS  # scripted group (container) (typed FeaturePython)
  Dunit = g/cm3
  Dvalue = 8.52
  Group = -> [Cu_element002,Zn_element002,Pb_element005]
  conduct = 2
  density = 1
  expand = 3
  formula = G4_BRASS
  name = G4_BRASS
  specific = 4
FEATURE [App::DocumentObjectGroupPython] Cu_element003  label="Cu_element : 89"  # scripted group (container) (typed FeaturePython)
  n = 89
  ref = Cu_element
FEATURE [App::DocumentObjectGroupPython] Zn_element003  label="Zn_element : 9"  # scripted group (container) (typed FeaturePython)
  n = 9
  ref = Zn_element
FEATURE [App::DocumentObjectGroupPython] Pb_element006  label="Pb_element : 2"  # scripted group (container) (typed FeaturePython)
  n = 2
  ref = Pb_element
FEATURE [App::DocumentObjectGroupPython] G4_BRONZE  # scripted group (container) (typed FeaturePython)
  Dunit = g/cm3
  Dvalue = 8.82
  Group = -> [Cu_element003,Zn_element003,Pb_element006]
  conduct = 2
  density = 1
  expand = 3
  formula = G4_BRONZE
  name = G4_BRONZE
  specific = 4
FEATURE [App::DocumentObjectGroupPython] Fe_element008  label="Fe_element : 74"  # scripted group (container) (typed FeaturePython)
  n = 74
  ref = Fe_element
FEATURE [App::DocumentObjectGroupPython] Cr_element002  label="Cr_element : 18"  # scripted group (container) (typed FeaturePython)
  n = 18
  ref = Cr_element
FEATURE [App::DocumentObjectGroupPython] Ni_element002  label="Ni_element : 8"  # scripted group (container) (typed FeaturePython)
  n = 8
  ref = Ni_element
FEATURE [App::DocumentObjectGroupPython] G4_STAINLESS_STEEL  label="G4_STAINLESS-STEEL"  # scripted group (container) (typed FeaturePython)
  Dunit = g/cm3
  Dvalue = 8
  Group = -> [Fe_element008,Cr_element002,Ni_element002]
  conduct = 2
  density = 1
  expand = 3
  formula = G4_STAINLESS-STEEL
  name = G4_STAINLESS-STEEL
  specific = 4
FEATURE [App::DocumentObjectGroupPython] H_element116  label="H_element : 064"  # scripted group (container) (typed FeaturePython)
  n = 18
  ref = H_element
FEATURE [App::DocumentObjectGroupPython] C_element126  label="C_element : 071"  # scripted group (container) (typed FeaturePython)
  n = 12
  ref = C_element
FEATURE [App::DocumentObjectGroupPython] O_element109  label="O_element : 062"  # scripted group (container) (typed FeaturePython)
  n = 7
  ref = O_element
FEATURE [App::DocumentObjectGroupPython] G4_CR39  # scripted group (container) (typed FeaturePython)
  Dunit = g/cm3
  Dvalue = 1.32
  Group = -> [H_element116,C_element126,O_element109]
  conduct = 2
  density = 1
  expand = 3
  formula = G4_CR39
  name = G4_CR39
  specific = 4
FEATURE [App::DocumentObjectGroupPython] H_element117  label="H_element : 38"  # scripted group (container) (typed FeaturePython)
  n = 38
  ref = H_element
FEATURE [App::DocumentObjectGroupPython] C_element127  label="C_element : 072"  # scripted group (container) (typed FeaturePython)
  n = 18
  ref = C_element
FEATURE [App::DocumentObjectGroupPython] O_element110  label="O_element : 063"  # scripted group (container) (typed FeaturePython)
  n = 1
  ref = O_element
FEATURE [App::DocumentObjectGroupPython] G4_OCTADECANOL  # scripted group (container) (typed FeaturePython)
  Dunit = g/cm3
  Dvalue = 0.812
  Group = -> [H_element117,C_element127,O_element110]
  conduct = 2
  density = 1
  expand = 3
  formula = G4_OCTADECANOL
  name = G4_OCTADECANOL
  specific = 4
FEATURE [App::DocumentObjectGroupPython] HEP  # scripted group (container) (typed FeaturePython)
  Group = -> [G4_lH2,G4_lN2,G4_lO2,G4_lAr,G4_lBr,G4_lKr,G4_lXe,G4_PbWO4,G4_Galactic,G4_GRAPHITE_POROUS,G4_LUCITE,G4_BRASS,G4_BRONZE,G4_STAINLESS_STEEL,G4_CR39,G4_OCTADECANOL]
FEATURE [App::DocumentObjectGroupPython] C_element128  label="C_element : 073"  # scripted group (container) (typed FeaturePython)
  n = 14
  ref = C_element
FEATURE [App::DocumentObjectGroupPython] H_element118  label="H_element : 065"  # scripted group (container) (typed FeaturePython)
  n = 10
  ref = H_element
FEATURE [App::DocumentObjectGroupPython] O_element111  label="O_element : 064"  # scripted group (container) (typed FeaturePython)
  n = 2
  ref = O_element
FEATURE [App::DocumentObjectGroupPython] N_element050  label="N_element : 023"  # scripted group (container) (typed FeaturePython)
  n = 2
  ref = N_element
FEATURE [App::DocumentObjectGroupPython] G4_KEVLAR  # scripted group (container) (typed FeaturePython)
  Dunit = g/cm3
  Dvalue = 1.44
  Group = -> [C_element128,H_element118,O_element111,N_element050]
  conduct = 2
  density = 1
  expand = 3
  formula = G4_KEVLAR
  name = G4_KEVLAR
  specific = 4
FEATURE [App::DocumentObjectGroupPython] C_element129  label="C_element : 074"  # scripted group (container) (typed FeaturePython)
  n = 10
  ref = C_element
FEATURE [App::DocumentObjectGroupPython] H_element119  label="H_element : 066"  # scripted group (container) (typed FeaturePython)
  n = 8
  ref = H_element
FEATURE [App::DocumentObjectGroupPython] O_element112  label="O_element : 065"  # scripted group (container) (typed FeaturePython)
  n = 4
  ref = O_element
FEATURE [App::DocumentObjectGroupPython] G4_DACRON  # scripted group (container) (typed FeaturePython)
  Dunit = g/cm3
  Dvalue = 1.4
  Group = -> [C_element129,H_element119,O_element112]
  conduct = 2
  density = 1
  expand = 3
  formula = G4_DACRON
  name = G4_DACRON
  specific = 4
FEATURE [App::DocumentObjectGroupPython] C_element130  label="C_element : 075"  # scripted group (container) (typed FeaturePython)
  n = 4
  ref = C_element
FEATURE [App::DocumentObjectGroupPython] H_element120  label="H_element : 067"  # scripted group (container) (typed FeaturePython)
  n = 5
  ref = H_element
FEATURE [App::DocumentObjectGroupPython] Cl_element030  label="Cl_element : 016"  # scripted group (container) (typed FeaturePython)
  n = 1
  ref = Cl_element
FEATURE [App::DocumentObjectGroupPython] G4_NEOPRENE  # scripted group (container) (typed FeaturePython)
  Dunit = g/cm3
  Dvalue = 1.23
  Group = -> [C_element130,H_element120,Cl_element030]
  conduct = 2
  density = 1
  expand = 3
  formula = G4_NEOPRENE
  name = G4_NEOPRENE
  specific = 4
FEATURE [App::DocumentObjectGroupPython] Space  # scripted group (container) (typed FeaturePython)
  Group = -> [G4_KEVLAR,G4_DACRON,G4_NEOPRENE]
FEATURE [App::DocumentObjectGroupPython] H_element121  label="H_element : 068"  # scripted group (container) (typed FeaturePython)
  n = 5
  ref = H_element
FEATURE [App::DocumentObjectGroupPython] C_element131  label="C_element : 076"  # scripted group (container) (typed FeaturePython)
  n = 4
  ref = C_element
FEATURE [App::DocumentObjectGroupPython] N_element051  label="N_element : 3"  # scripted group (container) (typed FeaturePython)
  n = 3
  ref = N_element
FEATURE [App::DocumentObjectGroupPython] O_element113  label="O_element : 066"  # scripted group (container) (typed FeaturePython)
  n = 1
  ref = O_element
FEATURE [App::DocumentObjectGroupPython] G4_CYTOSINE  # scripted group (container) (typed FeaturePython)
  Dunit = g/cm3
  Dvalue = 1.55
  Group = -> [H_element121,C_element131,N_element051,O_element113]
  conduct = 2
  density = 1
  expand = 3
  formula = G4_CYTOSINE
  name = G4_CYTOSINE
  specific = 4
FEATURE [App::DocumentObjectGroupPython] H_element122  label="H_element : 069"  # scripted group (container) (typed FeaturePython)
  n = 6
  ref = H_element
FEATURE [App::DocumentObjectGroupPython] C_element132  label="C_element : 077"  # scripted group (container) (typed FeaturePython)
  n = 5
  ref = C_element
FEATURE [App::DocumentObjectGroupPython] N_element052  label="N_element : 024"  # scripted group (container) (typed FeaturePython)
  n = 2
  ref = N_element
FEATURE [App::DocumentObjectGroupPython] O_element114  label="O_element : 067"  # scripted group (container) (typed FeaturePython)
  n = 2
  ref = O_element
FEATURE [App::DocumentObjectGroupPython] G4_THYMINE  # scripted group (container) (typed FeaturePython)
  Dunit = g/cm3
  Dvalue = 1.23
  Group = -> [H_element122,C_element132,N_element052,O_element114]
  conduct = 2
  density = 1
  expand = 3
  formula = G4_THYMINE
  name = G4_THYMINE
  specific = 4
FEATURE [App::DocumentObjectGroupPython] H_element123  label="H_element : 070"  # scripted group (container) (typed FeaturePython)
  n = 4
  ref = H_element
FEATURE [App::DocumentObjectGroupPython] C_element133  label="C_element : 078"  # scripted group (container) (typed FeaturePython)
  n = 4
  ref = C_element
FEATURE [App::DocumentObjectGroupPython] N_element053  label="N_element : 025"  # scripted group (container) (typed FeaturePython)
  n = 2
  ref = N_element
FEATURE [App::DocumentObjectGroupPython] O_element115  label="O_element : 068"  # scripted group (container) (typed FeaturePython)
  n = 2
  ref = O_element
FEATURE [App::DocumentObjectGroupPython] G4_URACIL  # scripted group (container) (typed FeaturePython)
  Dunit = g/cm3
  Dvalue = 1.32
  Group = -> [H_element123,C_element133,N_element053,O_element115]
  conduct = 2
  density = 1
  expand = 3
  formula = G4_URACIL
  name = G4_URACIL
  specific = 4
FEATURE [App::DocumentObjectGroupPython] H_element124  label="H_element : 071"  # scripted group (container) (typed FeaturePython)
  n = 4
  ref = H_element
FEATURE [App::DocumentObjectGroupPython] C_element134  label="C_element : 079"  # scripted group (container) (typed FeaturePython)
  n = 5
  ref = C_element
FEATURE [App::DocumentObjectGroupPython] N_element054  label="N_element : 026"  # scripted group (container) (typed FeaturePython)
  n = 5
  ref = N_element
FEATURE [App::DocumentObjectGroupPython] G4_DNA_ADENINE  # scripted group (container) (typed FeaturePython)
  Dunit = g/cm3
  Dvalue = 1
  Group = -> [H_element124,C_element134,N_element054]
  conduct = 2
  density = 1
  expand = 3
  formula = G4_DNA_ADENINE
  name = G4_DNA_ADENINE
  specific = 4
FEATURE [App::DocumentObjectGroupPython] H_element125  label="H_element : 072"  # scripted group (container) (typed FeaturePython)
  n = 4
  ref = H_element
FEATURE [App::DocumentObjectGroupPython] C_element135  label="C_element : 080"  # scripted group (container) (typed FeaturePython)
  n = 5
  ref = C_element
FEATURE [App::DocumentObjectGroupPython] N_element055  label="N_element : 027"  # scripted group (container) (typed FeaturePython)
  n = 5
  ref = N_element
FEATURE [App::DocumentObjectGroupPython] O_element116  label="O_element : 069"  # scripted group (container) (typed FeaturePython)
  n = 1
  ref = O_element
FEATURE [App::DocumentObjectGroupPython] G4_DNA_GUANINE  # scripted group (container) (typed FeaturePython)
  Dunit = g/cm3
  Dvalue = 1
  Group = -> [H_element125,C_element135,N_element055,O_element116]
  conduct = 2
  density = 1
  expand = 3
  formula = G4_DNA_GUANINE
  name = G4_DNA_GUANINE
  specific = 4
FEATURE [App::DocumentObjectGroupPython] H_element126  label="H_element : 073"  # scripted group (container) (typed FeaturePython)
  n = 4
  ref = H_element
FEATURE [App::DocumentObjectGroupPython] C_element136  label="C_element : 081"  # scripted group (container) (typed FeaturePython)
  n = 4
  ref = C_element
FEATURE [App::DocumentObjectGroupPython] N_element056  label="N_element : 028"  # scripted group (container) (typed FeaturePython)
  n = 3
  ref = N_element
FEATURE [App::DocumentObjectGroupPython] O_element117  label="O_element : 070"  # scripted group (container) (typed FeaturePython)
  n = 1
  ref = O_element
FEATURE [App::DocumentObjectGroupPython] G4_DNA_CYTOSINE  # scripted group (container) (typed FeaturePython)
  Dunit = g/cm3
  Dvalue = 1
  Group = -> [H_element126,C_element136,N_element056,O_element117]
  conduct = 2
  density = 1
  expand = 3
  formula = G4_DNA_CYTOSINE
  name = G4_DNA_CYTOSINE
  specific = 4
FEATURE [App::DocumentObjectGroupPython] H_element127  label="H_element : 074"  # scripted group (container) (typed FeaturePython)
  n = 5
  ref = H_element
FEATURE [App::DocumentObjectGroupPython] C_element137  label="C_element : 082"  # scripted group (container) (typed FeaturePython)
  n = 5
  ref = C_element
FEATURE [App::DocumentObjectGroupPython] N_element057  label="N_element : 029"  # scripted group (container) (typed FeaturePython)
  n = 2
  ref = N_element
FEATURE [App::DocumentObjectGroupPython] O_element118  label="O_element : 071"  # scripted group (container) (typed FeaturePython)
  n = 2
  ref = O_element
FEATURE [App::DocumentObjectGroupPython] G4_DNA_THYMINE  # scripted group (container) (typed FeaturePython)
  Dunit = g/cm3
  Dvalue = 1
  Group = -> [H_element127,C_element137,N_element057,O_element118]
  conduct = 2
  density = 1
  expand = 3
  formula = G4_DNA_THYMINE
  name = G4_DNA_THYMINE
  specific = 4
FEATURE [App::DocumentObjectGroupPython] H_element128  label="H_element : 075"  # scripted group (container) (typed FeaturePython)
  n = 3
  ref = H_element
FEATURE [App::DocumentObjectGroupPython] C_element138  label="C_element : 083"  # scripted group (container) (typed FeaturePython)
  n = 4
  ref = C_element
FEATURE [App::DocumentObjectGroupPython] N_element058  label="N_element : 030"  # scripted group (container) (typed FeaturePython)
  n = 2
  ref = N_element
FEATURE [App::DocumentObjectGroupPython] O_element119  label="O_element : 072"  # scripted group (container) (typed FeaturePython)
  n = 2
  ref = O_element
FEATURE [App::DocumentObjectGroupPython] G4_DNA_URACIL  # scripted group (container) (typed FeaturePython)
  Dunit = g/cm3
  Dvalue = 1
  Group = -> [H_element128,C_element138,N_element058,O_element119]
  conduct = 2
  density = 1
  expand = 3
  formula = G4_DNA_URACIL
  name = G4_DNA_URACIL
  specific = 4
FEATURE [App::DocumentObjectGroupPython] H_element129  label="H_element : 076"  # scripted group (container) (typed FeaturePython)
  n = 10
  ref = H_element
FEATURE [App::DocumentObjectGroupPython] C_element139  label="C_element : 084"  # scripted group (container) (typed FeaturePython)
  n = 10
  ref = C_element
FEATURE [App::DocumentObjectGroupPython] N_element059  label="N_element : 031"  # scripted group (container) (typed FeaturePython)
  n = 5
  ref = N_element
FEATURE [App::DocumentObjectGroupPython] O_element120  label="O_element : 073"  # scripted group (container) (typed FeaturePython)
  n = 4
  ref = O_element
FEATURE [App::DocumentObjectGroupPython] G4_DNA_ADENOSINE  # scripted group (container) (typed FeaturePython)
  Dunit = g/cm3
  Dvalue = 1
  Group = -> [H_element129,C_element139,N_element059,O_element120]
  conduct = 2
  density = 1
  expand = 3
  formula = G4_DNA_ADENOSINE
  name = G4_DNA_ADENOSINE
  specific = 4
FEATURE [App::DocumentObjectGroupPython] H_element130  label="H_element : 077"  # scripted group (container) (typed FeaturePython)
  n = 10
  ref = H_element
FEATURE [App::DocumentObjectGroupPython] C_element140  label="C_element : 085"  # scripted group (container) (typed FeaturePython)
  n = 10
  ref = C_element
FEATURE [App::DocumentObjectGroupPython] N_element060  label="N_element : 032"  # scripted group (container) (typed FeaturePython)
  n = 5
  ref = N_element
FEATURE [App::DocumentObjectGroupPython] O_element121  label="O_element : 074"  # scripted group (container) (typed FeaturePython)
  n = 5
  ref = O_element
FEATURE [App::DocumentObjectGroupPython] G4_DNA_GUANOSINE  # scripted group (container) (typed FeaturePython)
  Dunit = g/cm3
  Dvalue = 1
  Group = -> [H_element130,C_element140,N_element060,O_element121]
  conduct = 2
  density = 1
  expand = 3
  formula = G4_DNA_GUANOSINE
  name = G4_DNA_GUANOSINE
  specific = 4
FEATURE [App::DocumentObjectGroupPython] H_element131  label="H_element : 078"  # scripted group (container) (typed FeaturePython)
  n = 10
  ref = H_element
FEATURE [App::DocumentObjectGroupPython] C_element141  label="C_element : 086"  # scripted group (container) (typed FeaturePython)
  n = 9
  ref = C_element
FEATURE [App::DocumentObjectGroupPython] N_element061  label="N_element : 033"  # scripted group (container) (typed FeaturePython)
  n = 3
  ref = N_element
FEATURE [App::DocumentObjectGroupPython] O_element122  label="O_element : 075"  # scripted group (container) (typed FeaturePython)
  n = 5
  ref = O_element
FEATURE [App::DocumentObjectGroupPython] G4_DNA_CYTIDINE  # scripted group (container) (typed FeaturePython)
  Dunit = g/cm3
  Dvalue = 1
  Group = -> [H_element131,C_element141,N_element061,O_element122]
  conduct = 2
  density = 1
  expand = 3
  formula = G4_DNA_CYTIDINE
  name = G4_DNA_CYTIDINE
  specific = 4
FEATURE [App::DocumentObjectGroupPython] H_element132  label="H_element : 079"  # scripted group (container) (typed FeaturePython)
  n = 9
  ref = H_element
FEATURE [App::DocumentObjectGroupPython] C_element142  label="C_element : 087"  # scripted group (container) (typed FeaturePython)
  n = 9
  ref = C_element
FEATURE [App::DocumentObjectGroupPython] N_element062  label="N_element : 034"  # scripted group (container) (typed FeaturePython)
  n = 2
  ref = N_element
FEATURE [App::DocumentObjectGroupPython] O_element123  label="O_element : 076"  # scripted group (container) (typed FeaturePython)
  n = 6
  ref = O_element
FEATURE [App::DocumentObjectGroupPython] G4_DNA_URIDINE  # scripted group (container) (typed FeaturePython)
  Dunit = g/cm3
  Dvalue = 1
  Group = -> [H_element132,C_element142,N_element062,O_element123]
  conduct = 2
  density = 1
  expand = 3
  formula = G4_DNA_URIDINE
  name = G4_DNA_URIDINE
  specific = 4
FEATURE [App::DocumentObjectGroupPython] H_element133  label="H_element : 080"  # scripted group (container) (typed FeaturePython)
  n = 11
  ref = H_element
FEATURE [App::DocumentObjectGroupPython] C_element143  label="C_element : 088"  # scripted group (container) (typed FeaturePython)
  n = 10
  ref = C_element
FEATURE [App::DocumentObjectGroupPython] N_element063  label="N_element : 035"  # scripted group (container) (typed FeaturePython)
  n = 2
  ref = N_element
FEATURE [App::DocumentObjectGroupPython] O_element124  label="O_element : 077"  # scripted group (container) (typed FeaturePython)
  n = 6
  ref = O_element
FEATURE [App::DocumentObjectGroupPython] G4_DNA_METHYLURIDINE  # scripted group (container) (typed FeaturePython)
  Dunit = g/cm3
  Dvalue = 1
  Group = -> [H_element133,C_element143,N_element063,O_element124]
  conduct = 2
  density = 1
  expand = 3
  formula = G4_DNA_METHYLURIDINE
  name = G4_DNA_METHYLURIDINE
  specific = 4
FEATURE [App::DocumentObjectGroupPython] P_element014  label="P_element : 003"  # scripted group (container) (typed FeaturePython)
  n = 1
  ref = P_element
FEATURE [App::DocumentObjectGroupPython] O_element125  label="O_element : 078"  # scripted group (container) (typed FeaturePython)
  n = 3
  ref = O_element
FEATURE [App::DocumentObjectGroupPython] G4_DNA_MONOPHOSPHATE  # scripted group (container) (typed FeaturePython)
  Dunit = g/cm3
  Dvalue = 1
  Group = -> [P_element014,O_element125]
  conduct = 2
  density = 1
  expand = 3
  formula = G4_DNA_MONOPHOSPHATE
  name = G4_DNA_MONOPHOSPHATE
  specific = 4
FEATURE [App::DocumentObjectGroupPython] H_element134  label="H_element : 081"  # scripted group (container) (typed FeaturePython)
  n = 10
  ref = H_element
FEATURE [App::DocumentObjectGroupPython] C_element144  label="C_element : 089"  # scripted group (container) (typed FeaturePython)
  n = 10
  ref = C_element
FEATURE [App::DocumentObjectGroupPython] N_element064  label="N_element : 036"  # scripted group (container) (typed FeaturePython)
  n = 5
  ref = N_element
FEATURE [App::DocumentObjectGroupPython] O_element126  label="O_element : 079"  # scripted group (container) (typed FeaturePython)
  n = 7
  ref = O_element
FEATURE [App::DocumentObjectGroupPython] P_element015  label="P_element : 004"  # scripted group (container) (typed FeaturePython)
  n = 1
  ref = P_element
FEATURE [App::DocumentObjectGroupPython] G4_DNA_A  # scripted group (container) (typed FeaturePython)
  Dunit = g/cm3
  Dvalue = 1
  Group = -> [H_element134,C_element144,N_element064,O_element126,P_element015]
  conduct = 2
  density = 1
  expand = 3
  formula = G4_DNA_A
  name = G4_DNA_A
  specific = 4
FEATURE [App::DocumentObjectGroupPython] H_element135  label="H_element : 082"  # scripted group (container) (typed FeaturePython)
  n = 10
  ref = H_element
FEATURE [App::DocumentObjectGroupPython] C_element145  label="C_element : 090"  # scripted group (container) (typed FeaturePython)
  n = 10
  ref = C_element
FEATURE [App::DocumentObjectGroupPython] N_element065  label="N_element : 037"  # scripted group (container) (typed FeaturePython)
  n = 5
  ref = N_element
FEATURE [App::DocumentObjectGroupPython] O_element127  label="O_element : 8"  # scripted group (container) (typed FeaturePython)
  n = 8
  ref = O_element
FEATURE [App::DocumentObjectGroupPython] P_element016  label="P_element : 005"  # scripted group (container) (typed FeaturePython)
  n = 1
  ref = P_element
FEATURE [App::DocumentObjectGroupPython] G4_DNA_G  # scripted group (container) (typed FeaturePython)
  Dunit = g/cm3
  Dvalue = 1
  Group = -> [H_element135,C_element145,N_element065,O_element127,P_element016]
  conduct = 2
  density = 1
  expand = 3
  formula = G4_DNA_G
  name = G4_DNA_G
  specific = 4
FEATURE [App::DocumentObjectGroupPython] H_element136  label="H_element : 083"  # scripted group (container) (typed FeaturePython)
  n = 10
  ref = H_element
FEATURE [App::DocumentObjectGroupPython] C_element146  label="C_element : 091"  # scripted group (container) (typed FeaturePython)
  n = 9
  ref = C_element
FEATURE [App::DocumentObjectGroupPython] N_element066  label="N_element : 038"  # scripted group (container) (typed FeaturePython)
  n = 3
  ref = N_element
FEATURE [App::DocumentObjectGroupPython] O_element128  label="O_element : 080"  # scripted group (container) (typed FeaturePython)
  n = 8
  ref = O_element
FEATURE [App::DocumentObjectGroupPython] P_element017  label="P_element : 006"  # scripted group (container) (typed FeaturePython)
  n = 1
  ref = P_element
FEATURE [App::DocumentObjectGroupPython] G4_DNA_C  # scripted group (container) (typed FeaturePython)
  Dunit = g/cm3
  Dvalue = 1
  Group = -> [H_element136,C_element146,N_element066,O_element128,P_element017]
  conduct = 2
  density = 1
  expand = 3
  formula = G4_DNA_C
  name = G4_DNA_C
  specific = 4
FEATURE [App::DocumentObjectGroupPython] H_element137  label="H_element : 084"  # scripted group (container) (typed FeaturePython)
  n = 9
  ref = H_element
FEATURE [App::DocumentObjectGroupPython] C_element147  label="C_element : 092"  # scripted group (container) (typed FeaturePython)
  n = 9
  ref = C_element
FEATURE [App::DocumentObjectGroupPython] N_element067  label="N_element : 039"  # scripted group (container) (typed FeaturePython)
  n = 2
  ref = N_element
FEATURE [App::DocumentObjectGroupPython] O_element129  label="O_element : 9"  # scripted group (container) (typed FeaturePython)
  n = 9
  ref = O_element
FEATURE [App::DocumentObjectGroupPython] P_element018  label="P_element : 007"  # scripted group (container) (typed FeaturePython)
  n = 1
  ref = P_element
FEATURE [App::DocumentObjectGroupPython] G4_DNA_U  # scripted group (container) (typed FeaturePython)
  Dunit = g/cm3
  Dvalue = 1
  Group = -> [H_element137,C_element147,N_element067,O_element129,P_element018]
  conduct = 2
  density = 1
  expand = 3
  formula = G4_DNA_U
  name = G4_DNA_U
  specific = 4
FEATURE [App::DocumentObjectGroupPython] H_element138  label="H_element : 085"  # scripted group (container) (typed FeaturePython)
  n = 11
  ref = H_element
FEATURE [App::DocumentObjectGroupPython] C_element148  label="C_element : 093"  # scripted group (container) (typed FeaturePython)
  n = 10
  ref = C_element
FEATURE [App::DocumentObjectGroupPython] N_element068  label="N_element : 040"  # scripted group (container) (typed FeaturePython)
  n = 2
  ref = N_element
FEATURE [App::DocumentObjectGroupPython] O_element130  label="O_element : 081"  # scripted group (container) (typed FeaturePython)
  n = 9
  ref = O_element
FEATURE [App::DocumentObjectGroupPython] P_element019  label="P_element : 008"  # scripted group (container) (typed FeaturePython)
  n = 1
  ref = P_element
FEATURE [App::DocumentObjectGroupPython] G4_DNA_MU  # scripted group (container) (typed FeaturePython)
  Dunit = g/cm3
  Dvalue = 1
  Group = -> [H_element138,C_element148,N_element068,O_element130,P_element019]
  conduct = 2
  density = 1
  expand = 3
  formula = G4_DNA_MU
  name = G4_DNA_MU
  specific = 4
FEATURE [App::DocumentObjectGroupPython] BioChemical  # scripted group (container) (typed FeaturePython)
  Group = -> [G4_CYTOSINE,G4_THYMINE,G4_URACIL,G4_DNA_ADENINE,G4_DNA_GUANINE,G4_DNA_CYTOSINE,G4_DNA_THYMINE,G4_DNA_URACIL,G4_DNA_ADENOSINE,G4_DNA_GUANOSINE,G4_DNA_CYTIDINE,G4_DNA_URIDINE,G4_DNA_METHYLURIDINE,G4_DNA_MONOPHOSPHATE,G4_DNA_A,G4_DNA_G,G4_DNA_C,G4_DNA_U,G4_DNA_MU]
FEATURE [App::DocumentObjectGroupPython] G4Materials  # scripted group (container) (typed FeaturePython)
  Group = -> [NIST,Element,HEP,Space,BioChemical]
  version = 1
FEATURE [App::DocumentObjectGroupPython] Geant4  # scripted group (container) (typed FeaturePython)
  Group = -> [G4Isotopes,G4Elements,G4Materials]
FEATURE [App::DocumentObjectGroupPython] Materials  # scripted group (container) (typed FeaturePython)
  Group = -> [Geant4]
FEATURE [Part::FeaturePython] GDMLBox_WorldBox  # WARN: FeaturePython — macro-defined, semantics opaque (R4)
  lunit = 3
  material = 288
  x = 500
  y = 500
  z = 1200
FEATURE [Sketcher::SketchObject] Sketch001
  ArcFitTolerance = 0
  AttachmentSupport = -> [YZ_Plane001]
  FullyConstrained = false
  MakeInternals = false
  MapMode = 5
  Placement = pos=(0,0,0) rot=(0.57735,0.57735,0.57735;2.0944rad)
  sketch-geometry (36):
    g0: LineSegment StartX=345.196 StartY=1207.39 StartZ=0 EndX=345.196 EndY=4779.1 EndZ=0
    g1: LineSegment StartX=910.487 StartY=4896.42 StartZ=0 EndX=910.487 EndY=5006.42 EndZ=0
    g2: LineSegment StartX=435.196 StartY=4869.1 StartZ=0 EndX=445.196 EndY=4869.1 EndZ=0
    g3: LineSegment StartX=445.196 StartY=4869.1 StartZ=0 EndX=445.196 EndY=4896.42 EndZ=0
    g4: LineSegment StartX=445.196 StartY=4896.42 StartZ=0 EndX=910.487 EndY=4896.42 EndZ=0
    g5: LineSegment StartX=318.538 StartY=5006.42 StartZ=0 EndX=910.487 EndY=5006.42 EndZ=0
    g6: LineSegment StartX=175.531 StartY=1234.96 StartZ=0 EndX=318.538 EndY=1234.96 EndZ=0
    g7: LineSegment StartX=318.538 StartY=5006.42 StartZ=0 EndX=318.538 EndY=1234.96 EndZ=0
    g8: LineSegment StartX=0 StartY=39.215 StartZ=0 EndX=0 EndY=0 EndZ=0
    g9-g16: Circle [constr] x8 (B-spline internal-alignment scaffolding for g17; pole/knot coordinates omitted)
    g17: BSplineCurve PolesCount=8 KnotsCount=6 Degree=3 IsPeriodic=0
    g18-g23: GeomPoint [constr] x6 (B-spline internal-alignment scaffolding for g17; pole/knot coordinates omitted)
    g24: LineSegment StartX=175.531 StartY=1234.96 StartZ=0 EndX=175.531 EndY=838.896 EndZ=0
    g25-g29: Circle [constr] x5 (B-spline internal-alignment scaffolding for g30; pole/knot coordinates omitted)
    g30: BSplineCurve PolesCount=5 KnotsCount=3 Degree=3 IsPeriodic=0
    g31: GeomPoint [constr] X=175.531 Y=838.896 Z=0
    g32: GeomPoint [constr] X=165.058 Y=242.363 Z=0
    g33: GeomPoint [constr] X=0 Y=39.215 Z=0
    g34: ArcOfCircle CenterX=435.196 CenterY=4779.1 CenterZ=0 NormalX=0 NormalY=0 NormalZ=1 AngleXU=0 Radius=90 StartAngle=1.5708 EndAngle=3.14159
    g35: GeomPoint [constr] X=345.196 Y=4869.1 Z=0
  constraints (38):
    c: Vertical(g1)
    c: Horizontal(g2)
    c: Coincident(g2,g3)
    c: Vertical(g3)
    c: Coincident(g3,g4)
    c: Coincident(g4,g1)
    c: Horizontal(g4)
    c: Coincident(g5,g1)
    c: Horizontal(g5)
    c: Horizontal(g6)
    c: Coincident(g7,g5)
    c: Coincident(g7,g6)
    c: Vertical(g7)
    c: DistanceX(g35,g2) = 100
    c: Vertical(g8)
    c: Vertical(g0)
    c: Coincident(g17,g0)
    c: Weight(g9) = 1
    c: Equal(g9, g10-g16) x7
    c: Coincident(g17,g8)
    c: InternalAlignment(g9-g16 -> g17) x8
    c: InternalAlignment(g18-g23 -> g17) x6
    c: Coincident(g24,g6)
    c: Vertical(g24)
    c: Coincident(g30,g24)
    c: Weight(g25) = 1
    c: Equal(g25, g26-g29) x4
    c: Coincident(g30,g8)
    c: InternalAlignment(g25-g29 -> g30) x5
    c: InternalAlignment(g31,g30)
    c: InternalAlignment(g32,g30)
    c: InternalAlignment(g33,g30)
    c: Coincident(g8,g-1)
    c: PointOnObject(g35,g2)
    c: PointOnObject(g35,g0)
    c: Tangent(g2,g34) = 1.5708
    c: Tangent(g0,g34) = 1.5708
    c: Radius(g34) = 90
FEATURE [Part::Revolution] Revolve
  Angle = 360
  Axis = (0,0,1)
  Base = (0,0,0)
  FaceMakerClass = Part::FaceMakerBullseye
  Solid = true
  Source = -> Sketch001
  Symmetric = false
  material = 176
FEATURE [Part::Cylinder] Cylinder
  Angle = 360
  AttacherType = Attacher::AttachEngine3D
  FirstAngle = 0
  Height = 200
  Placement = pos=(474,0,4850) rot=(0,0,1;0rad)
  Radius = 60
  SecondAngle = 0
FEATURE [Part::FeaturePython] Array  # Draft array (typed FeaturePython)
  Angle = 360
  ArrayType = 1
  Axis = (0,0,1)
  Base = -> Cylinder
  Center = (0,0,0)
  Count = 6
  Fuse = false
  IntervalAxis = (0,0,0)
  IntervalX = (50,0,0)
  IntervalY = (0,50,0)
  IntervalZ = (0,0,50)
  NumberCircles = 3
  NumberPolar = 6
  NumberX = 2
  NumberY = 2
  NumberZ = 1
  RadialDistance = 50
  Symmetry = 1
  TangentialDistance = 25
FEATURE [Part::Cut] Cut
  Base = -> Revolve
  Tool = -> Array
FEATURE [App::Part] Bool_Cut
  Group = -> [Revolve,Cylinder,Sketch001,Array,Cut]
  Origin = -> Origin004
FEATURE [App::Part] worldVOL
  Group = -> [GDMLBox_WorldBox,Bool_Cut]
  Origin = -> Origin
